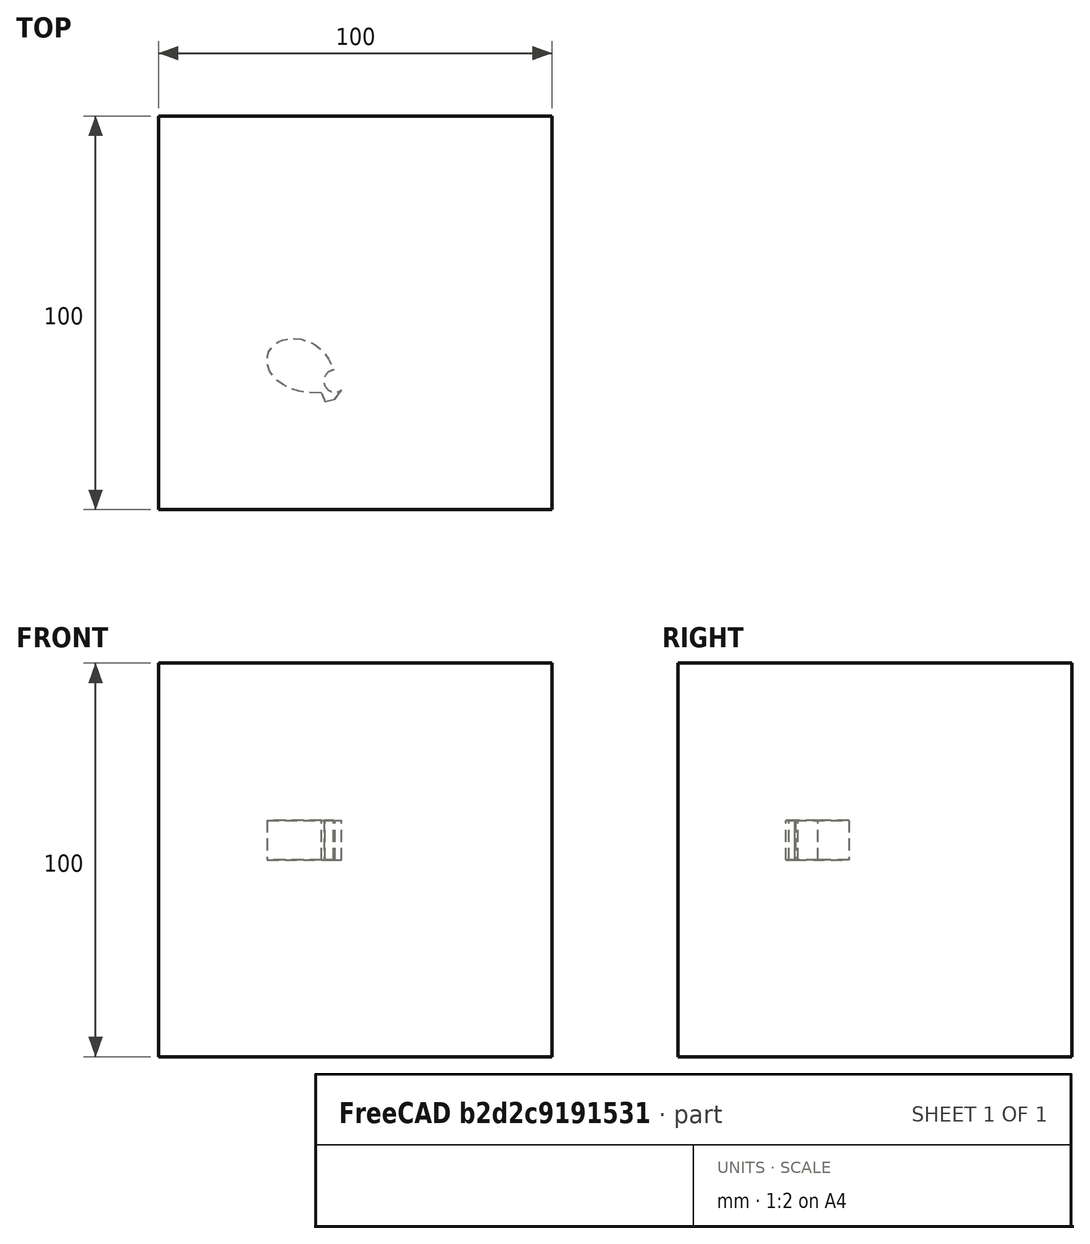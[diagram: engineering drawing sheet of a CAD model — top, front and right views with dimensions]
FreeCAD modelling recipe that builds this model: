
FCSTD DOCUMENT  (FreeCAD 0.19RUnknown)
Label: mirrorTest-2
License: All rights reserved
LicenseURL: http://en.wikipedia.org/wiki/All_rights_reserved
objects: App::DocumentObjectGroupPython×1248, Part::Mirroring×2, App::Part×2, Part::FeaturePython×1, Sketcher::SketchObject×1, Part::Extrusion×1
note: 5 computed .brp shape members not serialized (recipe doc carries the construction recipe); baked Part::Feature solids carry a one-line shape summary decoded from their .brp

FEATURE [App::DocumentObjectGroupPython] HALFPI  # scripted group (container) (typed FeaturePython)
  name = HALFPI
  value = pi/2.
FEATURE [App::DocumentObjectGroupPython] PI  # scripted group (container) (typed FeaturePython)
  name = PI
  value = 1.*pi
FEATURE [App::DocumentObjectGroupPython] TWOPI  # scripted group (container) (typed FeaturePython)
  name = TWOPI
  value = 2.*pi
FEATURE [App::DocumentObjectGroupPython] Constants  # scripted group (container) (typed FeaturePython)
  Group = -> [HALFPI,PI,TWOPI]
FEATURE [App::DocumentObjectGroupPython] Variables  # scripted group (container) (typed FeaturePython)
FEATURE [App::DocumentObjectGroupPython] Quantities  # scripted group (container) (typed FeaturePython)
FEATURE [App::DocumentObjectGroupPython] Isotopes  # scripted group (container) (typed FeaturePython)
FEATURE [App::DocumentObjectGroupPython] Elements  # scripted group (container) (typed FeaturePython)
FEATURE [App::DocumentObjectGroupPython] G4Isotopes  # scripted group (container) (typed FeaturePython)
FEATURE [App::DocumentObjectGroupPython] H_element  # scripted group (container) (typed FeaturePython)
  Z = 1
  atom_value = 1.008
  formula = H
  name = H_element
FEATURE [App::DocumentObjectGroupPython] He_element  # scripted group (container) (typed FeaturePython)
  Z = 2
  atom_value = 4.0026
  formula = He
  name = He_element
FEATURE [App::DocumentObjectGroupPython] Li_element  # scripted group (container) (typed FeaturePython)
  Z = 3
  atom_value = 6.94
  formula = Li
  name = Li_element
FEATURE [App::DocumentObjectGroupPython] Be_element  # scripted group (container) (typed FeaturePython)
  Z = 4
  atom_value = 9.01218
  formula = Be
  name = Be_element
FEATURE [App::DocumentObjectGroupPython] B_element  # scripted group (container) (typed FeaturePython)
  Z = 5
  atom_value = 10.81
  formula = B
  name = B_element
FEATURE [App::DocumentObjectGroupPython] C_element  # scripted group (container) (typed FeaturePython)
  Z = 6
  atom_value = 12.011
  formula = C
  name = C_element
FEATURE [App::DocumentObjectGroupPython] N_element  # scripted group (container) (typed FeaturePython)
  Z = 7
  atom_value = 14.007
  formula = N
  name = N_element
FEATURE [App::DocumentObjectGroupPython] O_element  # scripted group (container) (typed FeaturePython)
  Z = 8
  atom_value = 15.999
  formula = O
  name = O_element
FEATURE [App::DocumentObjectGroupPython] F_element  # scripted group (container) (typed FeaturePython)
  Z = 9
  atom_value = 18.9984
  formula = F
  name = F_element
FEATURE [App::DocumentObjectGroupPython] Ne_element  # scripted group (container) (typed FeaturePython)
  Z = 10
  atom_value = 20.1797
  formula = Ne
  name = Ne_element
FEATURE [App::DocumentObjectGroupPython] Na_element  # scripted group (container) (typed FeaturePython)
  Z = 11
  atom_value = 22.9898
  formula = Na
  name = Na_element
FEATURE [App::DocumentObjectGroupPython] Mg_element  # scripted group (container) (typed FeaturePython)
  Z = 12
  atom_value = 24.305
  formula = Mg
  name = Mg_element
FEATURE [App::DocumentObjectGroupPython] Al_element  # scripted group (container) (typed FeaturePython)
  Z = 13
  atom_value = 26.9815
  formula = Al
  name = Al_element
FEATURE [App::DocumentObjectGroupPython] Si_element  # scripted group (container) (typed FeaturePython)
  Z = 14
  atom_value = 28.085
  formula = Si
  name = Si_element
FEATURE [App::DocumentObjectGroupPython] P_element  # scripted group (container) (typed FeaturePython)
  Z = 15
  atom_value = 30.9738
  formula = P
  name = P_element
FEATURE [App::DocumentObjectGroupPython] S_element  # scripted group (container) (typed FeaturePython)
  Z = 16
  atom_value = 32.06
  formula = S
  name = S_element
FEATURE [App::DocumentObjectGroupPython] Cl_element  # scripted group (container) (typed FeaturePython)
  Z = 17
  atom_value = 35.45
  formula = Cl
  name = Cl_element
FEATURE [App::DocumentObjectGroupPython] Ar_element  # scripted group (container) (typed FeaturePython)
  Z = 18
  atom_value = 39.95
  formula = Ar
  name = Ar_element
FEATURE [App::DocumentObjectGroupPython] K_element  # scripted group (container) (typed FeaturePython)
  Z = 19
  atom_value = 39.0983
  formula = K
  name = K_element
FEATURE [App::DocumentObjectGroupPython] Ca_element  # scripted group (container) (typed FeaturePython)
  Z = 20
  atom_value = 40.078
  formula = Ca
  name = Ca_element
FEATURE [App::DocumentObjectGroupPython] Sc_element  # scripted group (container) (typed FeaturePython)
  Z = 21
  atom_value = 44.9559
  formula = Sc
  name = Sc_element
FEATURE [App::DocumentObjectGroupPython] Ti_element  # scripted group (container) (typed FeaturePython)
  Z = 22
  atom_value = 47.867
  formula = Ti
  name = Ti_element
FEATURE [App::DocumentObjectGroupPython] V_element  # scripted group (container) (typed FeaturePython)
  Z = 23
  atom_value = 50.9415
  formula = V
  name = V_element
FEATURE [App::DocumentObjectGroupPython] Cr_element  # scripted group (container) (typed FeaturePython)
  Z = 24
  atom_value = 51.9961
  formula = Cr
  name = Cr_element
FEATURE [App::DocumentObjectGroupPython] Mn_element  # scripted group (container) (typed FeaturePython)
  Z = 25
  atom_value = 54.938
  formula = Mn
  name = Mn_element
FEATURE [App::DocumentObjectGroupPython] Fe_element  # scripted group (container) (typed FeaturePython)
  Z = 26
  atom_value = 55.845
  formula = Fe
  name = Fe_element
FEATURE [App::DocumentObjectGroupPython] Co_element  # scripted group (container) (typed FeaturePython)
  Z = 27
  atom_value = 58.9332
  formula = Co
  name = Co_element
FEATURE [App::DocumentObjectGroupPython] Ni_element  # scripted group (container) (typed FeaturePython)
  Z = 28
  atom_value = 58.6934
  formula = Ni
  name = Ni_element
FEATURE [App::DocumentObjectGroupPython] Cu_element  # scripted group (container) (typed FeaturePython)
  Z = 29
  atom_value = 63.546
  formula = Cu
  name = Cu_element
FEATURE [App::DocumentObjectGroupPython] Zn_element  # scripted group (container) (typed FeaturePython)
  Z = 30
  atom_value = 65.38
  formula = Zn
  name = Zn_element
FEATURE [App::DocumentObjectGroupPython] Ga_element  # scripted group (container) (typed FeaturePython)
  Z = 31
  atom_value = 69.723
  formula = Ga
  name = Ga_element
FEATURE [App::DocumentObjectGroupPython] Ge_element  # scripted group (container) (typed FeaturePython)
  Z = 32
  atom_value = 72.63
  formula = Ge
  name = Ge_element
FEATURE [App::DocumentObjectGroupPython] As_element  # scripted group (container) (typed FeaturePython)
  Z = 33
  atom_value = 74.9216
  formula = As
  name = As_element
FEATURE [App::DocumentObjectGroupPython] Se_element  # scripted group (container) (typed FeaturePython)
  Z = 34
  atom_value = 78.971
  formula = Se
  name = Se_element
FEATURE [App::DocumentObjectGroupPython] Br_element  # scripted group (container) (typed FeaturePython)
  Z = 35
  atom_value = 79.904
  formula = Br
  name = Br_element
FEATURE [App::DocumentObjectGroupPython] Kr_element  # scripted group (container) (typed FeaturePython)
  Z = 36
  atom_value = 83.798
  formula = Kr
  name = Kr_element
FEATURE [App::DocumentObjectGroupPython] Rb_element  # scripted group (container) (typed FeaturePython)
  Z = 37
  atom_value = 85.4678
  formula = Rb
  name = Rb_element
FEATURE [App::DocumentObjectGroupPython] Sr_element  # scripted group (container) (typed FeaturePython)
  Z = 38
  atom_value = 87.62
  formula = Sr
  name = Sr_element
FEATURE [App::DocumentObjectGroupPython] Y_element  # scripted group (container) (typed FeaturePython)
  Z = 39
  atom_value = 88.9058
  formula = Y
  name = Y_element
FEATURE [App::DocumentObjectGroupPython] Zr_element  # scripted group (container) (typed FeaturePython)
  Z = 40
  atom_value = 91.224
  formula = Zr
  name = Zr_element
FEATURE [App::DocumentObjectGroupPython] Nb_element  # scripted group (container) (typed FeaturePython)
  Z = 41
  atom_value = 92.9064
  formula = Nb
  name = Nb_element
FEATURE [App::DocumentObjectGroupPython] Mo_element  # scripted group (container) (typed FeaturePython)
  Z = 42
  atom_value = 95.95
  formula = Mo
  name = Mo_element
FEATURE [App::DocumentObjectGroupPython] Tc_element  # scripted group (container) (typed FeaturePython)
  Z = 43
  atom_value = 97
  formula = Tc
  name = Tc_element
FEATURE [App::DocumentObjectGroupPython] Ru_element  # scripted group (container) (typed FeaturePython)
  Z = 44
  atom_value = 101.07
  formula = Ru
  name = Ru_element
FEATURE [App::DocumentObjectGroupPython] Rh_element  # scripted group (container) (typed FeaturePython)
  Z = 45
  atom_value = 102.905
  formula = Rh
  name = Rh_element
FEATURE [App::DocumentObjectGroupPython] Pd_element  # scripted group (container) (typed FeaturePython)
  Z = 46
  atom_value = 106.42
  formula = Pd
  name = Pd_element
FEATURE [App::DocumentObjectGroupPython] Ag_element  # scripted group (container) (typed FeaturePython)
  Z = 47
  atom_value = 107.868
  formula = Ag
  name = Ag_element
FEATURE [App::DocumentObjectGroupPython] Cd_element  # scripted group (container) (typed FeaturePython)
  Z = 48
  atom_value = 112.414
  formula = Cd
  name = Cd_element
FEATURE [App::DocumentObjectGroupPython] In_element  # scripted group (container) (typed FeaturePython)
  Z = 49
  atom_value = 114.818
  formula = In
  name = In_element
FEATURE [App::DocumentObjectGroupPython] Sn_element  # scripted group (container) (typed FeaturePython)
  Z = 50
  atom_value = 118.71
  formula = Sn
  name = Sn_element
FEATURE [App::DocumentObjectGroupPython] Sb_element  # scripted group (container) (typed FeaturePython)
  Z = 51
  atom_value = 121.76
  formula = Sb
  name = Sb_element
FEATURE [App::DocumentObjectGroupPython] Te_element  # scripted group (container) (typed FeaturePython)
  Z = 52
  atom_value = 127.6
  formula = Te
  name = Te_element
FEATURE [App::DocumentObjectGroupPython] I_element  # scripted group (container) (typed FeaturePython)
  Z = 53
  atom_value = 126.904
  formula = I
  name = I_element
FEATURE [App::DocumentObjectGroupPython] Xe_element  # scripted group (container) (typed FeaturePython)
  Z = 54
  atom_value = 131.293
  formula = Xe
  name = Xe_element
FEATURE [App::DocumentObjectGroupPython] Cs_element  # scripted group (container) (typed FeaturePython)
  Z = 55
  atom_value = 132.905
  formula = Cs
  name = Cs_element
FEATURE [App::DocumentObjectGroupPython] Ba_element  # scripted group (container) (typed FeaturePython)
  Z = 56
  atom_value = 137.327
  formula = Ba
  name = Ba_element
FEATURE [App::DocumentObjectGroupPython] La_element  # scripted group (container) (typed FeaturePython)
  Z = 57
  atom_value = 138.905
  formula = La
  name = La_element
FEATURE [App::DocumentObjectGroupPython] Ce_element  # scripted group (container) (typed FeaturePython)
  Z = 58
  atom_value = 140.116
  formula = Ce
  name = Ce_element
FEATURE [App::DocumentObjectGroupPython] Pr_element  # scripted group (container) (typed FeaturePython)
  Z = 59
  atom_value = 140.908
  formula = Pr
  name = Pr_element
FEATURE [App::DocumentObjectGroupPython] Nd_element  # scripted group (container) (typed FeaturePython)
  Z = 60
  atom_value = 144.242
  formula = Nd
  name = Nd_element
FEATURE [App::DocumentObjectGroupPython] Pm_element  # scripted group (container) (typed FeaturePython)
  Z = 61
  atom_value = 145
  formula = Pm
  name = Pm_element
FEATURE [App::DocumentObjectGroupPython] Sm_element  # scripted group (container) (typed FeaturePython)
  Z = 62
  atom_value = 150.36
  formula = Sm
  name = Sm_element
FEATURE [App::DocumentObjectGroupPython] Eu_element  # scripted group (container) (typed FeaturePython)
  Z = 63
  atom_value = 151.964
  formula = Eu
  name = Eu_element
FEATURE [App::DocumentObjectGroupPython] Gd_element  # scripted group (container) (typed FeaturePython)
  Z = 64
  atom_value = 157.25
  formula = Gd
  name = Gd_element
FEATURE [App::DocumentObjectGroupPython] Tb_element  # scripted group (container) (typed FeaturePython)
  Z = 65
  atom_value = 158.925
  formula = Tb
  name = Tb_element
FEATURE [App::DocumentObjectGroupPython] Dy_element  # scripted group (container) (typed FeaturePython)
  Z = 66
  atom_value = 162.5
  formula = Dy
  name = Dy_element
FEATURE [App::DocumentObjectGroupPython] Ho_element  # scripted group (container) (typed FeaturePython)
  Z = 67
  atom_value = 164.93
  formula = Ho
  name = Ho_element
FEATURE [App::DocumentObjectGroupPython] Er_element  # scripted group (container) (typed FeaturePython)
  Z = 68
  atom_value = 167.259
  formula = Er
  name = Er_element
FEATURE [App::DocumentObjectGroupPython] Tm_element  # scripted group (container) (typed FeaturePython)
  Z = 69
  atom_value = 168.934
  formula = Tm
  name = Tm_element
FEATURE [App::DocumentObjectGroupPython] Yb_element  # scripted group (container) (typed FeaturePython)
  Z = 70
  atom_value = 173.045
  formula = Yb
  name = Yb_element
FEATURE [App::DocumentObjectGroupPython] Lu_element  # scripted group (container) (typed FeaturePython)
  Z = 71
  atom_value = 174.967
  formula = Lu
  name = Lu_element
FEATURE [App::DocumentObjectGroupPython] Hf_element  # scripted group (container) (typed FeaturePython)
  Z = 72
  atom_value = 178.49
  formula = Hf
  name = Hf_element
FEATURE [App::DocumentObjectGroupPython] Ta_element  # scripted group (container) (typed FeaturePython)
  Z = 73
  atom_value = 180.948
  formula = Ta
  name = Ta_element
FEATURE [App::DocumentObjectGroupPython] W_element  # scripted group (container) (typed FeaturePython)
  Z = 74
  atom_value = 183.84
  formula = W
  name = W_element
FEATURE [App::DocumentObjectGroupPython] Re_element  # scripted group (container) (typed FeaturePython)
  Z = 75
  atom_value = 186.207
  formula = Re
  name = Re_element
FEATURE [App::DocumentObjectGroupPython] Os_element  # scripted group (container) (typed FeaturePython)
  Z = 76
  atom_value = 190.23
  formula = Os
  name = Os_element
FEATURE [App::DocumentObjectGroupPython] Ir_element  # scripted group (container) (typed FeaturePython)
  Z = 77
  atom_value = 192.217
  formula = Ir
  name = Ir_element
FEATURE [App::DocumentObjectGroupPython] Pt_element  # scripted group (container) (typed FeaturePython)
  Z = 78
  atom_value = 195.084
  formula = Pt
  name = Pt_element
FEATURE [App::DocumentObjectGroupPython] Au_element  # scripted group (container) (typed FeaturePython)
  Z = 79
  atom_value = 196.967
  formula = Au
  name = Au_element
FEATURE [App::DocumentObjectGroupPython] Hg_element  # scripted group (container) (typed FeaturePython)
  Z = 80
  atom_value = 200.592
  formula = Hg
  name = Hg_element
FEATURE [App::DocumentObjectGroupPython] Tl_element  # scripted group (container) (typed FeaturePython)
  Z = 81
  atom_value = 204.38
  formula = Tl
  name = Tl_element
FEATURE [App::DocumentObjectGroupPython] Pb_element  # scripted group (container) (typed FeaturePython)
  Z = 82
  atom_value = 207.2
  formula = Pb
  name = Pb_element
FEATURE [App::DocumentObjectGroupPython] Bi_element  # scripted group (container) (typed FeaturePython)
  Z = 83
  atom_value = 208.98
  formula = Bi
  name = Bi_element
FEATURE [App::DocumentObjectGroupPython] Po_element  # scripted group (container) (typed FeaturePython)
  Z = 84
  atom_value = 209
  formula = Po
  name = Po_element
FEATURE [App::DocumentObjectGroupPython] At_element  # scripted group (container) (typed FeaturePython)
  Z = 85
  atom_value = 210
  formula = At
  name = At_element
FEATURE [App::DocumentObjectGroupPython] Rn_element  # scripted group (container) (typed FeaturePython)
  Z = 86
  atom_value = 222
  formula = Rn
  name = Rn_element
FEATURE [App::DocumentObjectGroupPython] Fr_element  # scripted group (container) (typed FeaturePython)
  Z = 87
  atom_value = 223
  formula = Fr
  name = Fr_element
FEATURE [App::DocumentObjectGroupPython] Ra_element  # scripted group (container) (typed FeaturePython)
  Z = 88
  atom_value = 226
  formula = Ra
  name = Ra_element
FEATURE [App::DocumentObjectGroupPython] Ac_element  # scripted group (container) (typed FeaturePython)
  Z = 89
  atom_value = 227
  formula = Ac
  name = Ac_element
FEATURE [App::DocumentObjectGroupPython] Th_element  # scripted group (container) (typed FeaturePython)
  Z = 90
  atom_value = 232.038
  formula = Th
  name = Th_element
FEATURE [App::DocumentObjectGroupPython] Pa_element  # scripted group (container) (typed FeaturePython)
  Z = 91
  atom_value = 231.036
  formula = Pa
  name = Pa_element
FEATURE [App::DocumentObjectGroupPython] U_element  # scripted group (container) (typed FeaturePython)
  Z = 92
  atom_value = 238.029
  formula = U
  name = U_element
FEATURE [App::DocumentObjectGroupPython] Np_element  # scripted group (container) (typed FeaturePython)
  Z = 93
  atom_value = 237
  formula = Np
  name = Np_element
FEATURE [App::DocumentObjectGroupPython] Pu_element  # scripted group (container) (typed FeaturePython)
  Z = 94
  atom_value = 244
  formula = Pu
  name = Pu_element
FEATURE [App::DocumentObjectGroupPython] Am_element  # scripted group (container) (typed FeaturePython)
  Z = 95
  atom_value = 243
  formula = Am
  name = Am_element
FEATURE [App::DocumentObjectGroupPython] Cm_element  # scripted group (container) (typed FeaturePython)
  Z = 96
  atom_value = 247
  formula = Cm
  name = Cm_element
FEATURE [App::DocumentObjectGroupPython] Bk_element  # scripted group (container) (typed FeaturePython)
  Z = 97
  atom_value = 247
  formula = Bk
  name = Bk_element
FEATURE [App::DocumentObjectGroupPython] Cf_element  # scripted group (container) (typed FeaturePython)
  Z = 98
  atom_value = 251
  formula = Cf
  name = Cf_element
FEATURE [App::DocumentObjectGroupPython] G4Elements  # scripted group (container) (typed FeaturePython)
  Group = -> [H_element,He_element,Li_element,Be_element,B_element,C_element,N_element,O_element,F_element,Ne_element,Na_element,Mg_element,Al_element,Si_element,P_element,S_element,Cl_element,Ar_element,K_element,Ca_element,Sc_element,Ti_element,V_element,Cr_element,Mn_element,Fe_element,Co_element,Ni_element,Cu_element,Zn_element,Ga_element,Ge_element,As_element,Se_element,Br_element,Kr_element,Rb_element,+61 more]
FEATURE [App::DocumentObjectGroupPython] H_element001  label="H_element : 0.101"  # scripted group (container) (typed FeaturePython)
  n = 0.101327
FEATURE [App::DocumentObjectGroupPython] C_element001  label="C_element : 0.775"  # scripted group (container) (typed FeaturePython)
  n = 0.7755
FEATURE [App::DocumentObjectGroupPython] N_element001  label="N_element : 0.035"  # scripted group (container) (typed FeaturePython)
  n = 0.035057
FEATURE [App::DocumentObjectGroupPython] O_element001  label="O_element : 0.052"  # scripted group (container) (typed FeaturePython)
  n = 0.0523159
FEATURE [App::DocumentObjectGroupPython] F_element001  label="F_element : 0.017"  # scripted group (container) (typed FeaturePython)
  n = 0.017422
FEATURE [App::DocumentObjectGroupPython] Ca_element001  label="Ca_element : 0.018"  # scripted group (container) (typed FeaturePython)
  n = 0.018378
FEATURE [App::DocumentObjectGroupPython] G4_A_150_TISSUE  label="G4_A-150_TISSUE"  # scripted group (container) (typed FeaturePython)
  Dunit = g/cm3
  Dvalue = 1.127
  Group = -> [H_element001,C_element001,N_element001,O_element001,F_element001,Ca_element001]
  conduct = 2
  density = 1
  expand = 3
  formula = G4_A-150_TISSUE
  name = G4_A-150_TISSUE
  specific = 4
FEATURE [App::DocumentObjectGroupPython] C_element002  label="C_element : 3"  # scripted group (container) (typed FeaturePython)
  n = 3
  ref = C_element
FEATURE [App::DocumentObjectGroupPython] H_element002  label="H_element : 6"  # scripted group (container) (typed FeaturePython)
  n = 6
  ref = H_element
FEATURE [App::DocumentObjectGroupPython] O_element002  label="O_element : 1"  # scripted group (container) (typed FeaturePython)
  n = 1
  ref = O_element
FEATURE [App::DocumentObjectGroupPython] G4_ACETONE  # scripted group (container) (typed FeaturePython)
  Dunit = g/cm3
  Dvalue = 0.7899
  Group = -> [C_element002,H_element002,O_element002]
  conduct = 2
  density = 1
  expand = 3
  formula = G4_ACETONE
  name = G4_ACETONE
  specific = 4
FEATURE [App::DocumentObjectGroupPython] C_element003  label="C_element : 2"  # scripted group (container) (typed FeaturePython)
  n = 2
  ref = C_element
FEATURE [App::DocumentObjectGroupPython] H_element003  label="H_element : 2"  # scripted group (container) (typed FeaturePython)
  n = 2
  ref = H_element
FEATURE [App::DocumentObjectGroupPython] G4_ACETYLENE  # scripted group (container) (typed FeaturePython)
  Dunit = g/cm3
  Dvalue = 0.0010967
  Group = -> [C_element003,H_element003]
  conduct = 2
  density = 1
  expand = 3
  formula = G4_ACETYLENE
  name = G4_ACETYLENE
  specific = 4
FEATURE [App::DocumentObjectGroupPython] C_element004  label="C_element : 5"  # scripted group (container) (typed FeaturePython)
  n = 5
  ref = C_element
FEATURE [App::DocumentObjectGroupPython] H_element004  label="H_element : 5"  # scripted group (container) (typed FeaturePython)
  n = 5
  ref = H_element
FEATURE [App::DocumentObjectGroupPython] N_element002  label="N_element : 5"  # scripted group (container) (typed FeaturePython)
  n = 5
  ref = N_element
FEATURE [App::DocumentObjectGroupPython] G4_ADENINE  # scripted group (container) (typed FeaturePython)
  Dunit = g/cm3
  Dvalue = 1.6
  Group = -> [C_element004,H_element004,N_element002]
  conduct = 2
  density = 1
  expand = 3
  formula = G4_ADENINE
  name = G4_ADENINE
  specific = 4
FEATURE [App::DocumentObjectGroupPython] H_element005  label="H_element : 0.114"  # scripted group (container) (typed FeaturePython)
  n = 0.114
FEATURE [App::DocumentObjectGroupPython] C_element005  label="C_element : 0.598"  # scripted group (container) (typed FeaturePython)
  n = 0.598
FEATURE [App::DocumentObjectGroupPython] N_element003  label="N_element : 0.007"  # scripted group (container) (typed FeaturePython)
  n = 0.007
FEATURE [App::DocumentObjectGroupPython] O_element003  label="O_element : 0.278"  # scripted group (container) (typed FeaturePython)
  n = 0.278
FEATURE [App::DocumentObjectGroupPython] Na_element001  label="Na_element : 0.001"  # scripted group (container) (typed FeaturePython)
  n = 0.001
FEATURE [App::DocumentObjectGroupPython] S_element001  label="S_element : 0.001"  # scripted group (container) (typed FeaturePython)
  n = 0.001
FEATURE [App::DocumentObjectGroupPython] Cl_element001  label="Cl_element : 0.001"  # scripted group (container) (typed FeaturePython)
  n = 0.001
FEATURE [App::DocumentObjectGroupPython] G4_ADIPOSE_TISSUE_ICRP  # scripted group (container) (typed FeaturePython)
  Dunit = g/cm3
  Dvalue = 0.95
  Group = -> [H_element005,C_element005,N_element003,O_element003,Na_element001,S_element001,Cl_element001]
  conduct = 2
  density = 1
  expand = 3
  formula = G4_ADIPOSE_TISSUE_ICRP
  name = G4_ADIPOSE_TISSUE_ICRP
  specific = 4
FEATURE [App::DocumentObjectGroupPython] C_element006  label="C_element : 0.000"  # scripted group (container) (typed FeaturePython)
  n = 0.000124
FEATURE [App::DocumentObjectGroupPython] N_element004  label="N_element : 0.755"  # scripted group (container) (typed FeaturePython)
  n = 0.755268
FEATURE [App::DocumentObjectGroupPython] O_element004  label="O_element : 0.232"  # scripted group (container) (typed FeaturePython)
  n = 0.231781
FEATURE [App::DocumentObjectGroupPython] Ar_element001  label="Ar_element : 0.013"  # scripted group (container) (typed FeaturePython)
  n = 0.012827
FEATURE [App::DocumentObjectGroupPython] G4_AIR  # scripted group (container) (typed FeaturePython)
  Dunit = g/cm3
  Dvalue = 0.00120479
  Group = -> [C_element006,N_element004,O_element004,Ar_element001]
  conduct = 2
  density = 1
  expand = 3
  formula = G4_AIR
  name = G4_AIR
  specific = 4
FEATURE [App::DocumentObjectGroupPython] C_element007  label="C_element : 006"  # scripted group (container) (typed FeaturePython)
  n = 3
  ref = C_element
FEATURE [App::DocumentObjectGroupPython] H_element006  label="H_element : 7"  # scripted group (container) (typed FeaturePython)
  n = 7
  ref = H_element
FEATURE [App::DocumentObjectGroupPython] N_element005  label="N_element : 1"  # scripted group (container) (typed FeaturePython)
  n = 1
  ref = N_element
FEATURE [App::DocumentObjectGroupPython] O_element005  label="O_element : 2"  # scripted group (container) (typed FeaturePython)
  n = 2
  ref = O_element
FEATURE [App::DocumentObjectGroupPython] G4_ALANINE  # scripted group (container) (typed FeaturePython)
  Dunit = g/cm3
  Dvalue = 1.42
  Group = -> [C_element007,H_element006,N_element005,O_element005]
  conduct = 2
  density = 1
  expand = 3
  formula = G4_ALANINE
  name = G4_ALANINE
  specific = 4
FEATURE [App::DocumentObjectGroupPython] Al_element001  label="Al_element : 2"  # scripted group (container) (typed FeaturePython)
  n = 2
  ref = Al_element
FEATURE [App::DocumentObjectGroupPython] O_element006  label="O_element : 3"  # scripted group (container) (typed FeaturePython)
  n = 3
  ref = O_element
FEATURE [App::DocumentObjectGroupPython] G4_ALUMINUM_OXIDE  # scripted group (container) (typed FeaturePython)
  Dunit = g/cm3
  Dvalue = 3.97
  Group = -> [Al_element001,O_element006]
  conduct = 2
  density = 1
  expand = 3
  formula = G4_ALUMINUM_OXIDE
  name = G4_ALUMINUM_OXIDE
  specific = 4
FEATURE [App::DocumentObjectGroupPython] H_element007  label="H_element : 0.106"  # scripted group (container) (typed FeaturePython)
  n = 0.10593
FEATURE [App::DocumentObjectGroupPython] C_element008  label="C_element : 0.789"  # scripted group (container) (typed FeaturePython)
  n = 0.788974
FEATURE [App::DocumentObjectGroupPython] O_element007  label="O_element : 0.105"  # scripted group (container) (typed FeaturePython)
  n = 0.105096
FEATURE [App::DocumentObjectGroupPython] G4_AMBER  # scripted group (container) (typed FeaturePython)
  Dunit = g/cm3
  Dvalue = 1.1
  Group = -> [H_element007,C_element008,O_element007]
  conduct = 2
  density = 1
  expand = 3
  formula = G4_AMBER
  name = G4_AMBER
  specific = 4
FEATURE [App::DocumentObjectGroupPython] N_element006  label="N_element : 006"  # scripted group (container) (typed FeaturePython)
  n = 1
  ref = N_element
FEATURE [App::DocumentObjectGroupPython] H_element008  label="H_element : 3"  # scripted group (container) (typed FeaturePython)
  n = 3
  ref = H_element
FEATURE [App::DocumentObjectGroupPython] G4_AMMONIA  # scripted group (container) (typed FeaturePython)
  Dunit = g/cm3
  Dvalue = 0.000826019
  Group = -> [N_element006,H_element008]
  conduct = 2
  density = 1
  expand = 3
  formula = G4_AMMONIA
  name = G4_AMMONIA
  specific = 4
FEATURE [App::DocumentObjectGroupPython] C_element009  label="C_element : 6"  # scripted group (container) (typed FeaturePython)
  n = 6
  ref = C_element
FEATURE [App::DocumentObjectGroupPython] H_element009  label="H_element : 008"  # scripted group (container) (typed FeaturePython)
  n = 7
  ref = H_element
FEATURE [App::DocumentObjectGroupPython] N_element007  label="N_element : 007"  # scripted group (container) (typed FeaturePython)
  n = 1
  ref = N_element
FEATURE [App::DocumentObjectGroupPython] G4_ANILINE  # scripted group (container) (typed FeaturePython)
  Dunit = g/cm3
  Dvalue = 1.0235
  Group = -> [C_element009,H_element009,N_element007]
  conduct = 2
  density = 1
  expand = 3
  formula = G4_ANILINE
  name = G4_ANILINE
  specific = 4
FEATURE [App::DocumentObjectGroupPython] C_element010  label="C_element : 14"  # scripted group (container) (typed FeaturePython)
  n = 14
  ref = C_element
FEATURE [App::DocumentObjectGroupPython] H_element010  label="H_element : 10"  # scripted group (container) (typed FeaturePython)
  n = 10
  ref = H_element
FEATURE [App::DocumentObjectGroupPython] G4_ANTHRACENE  # scripted group (container) (typed FeaturePython)
  Dunit = g/cm3
  Dvalue = 1.283
  Group = -> [C_element010,H_element010]
  conduct = 2
  density = 1
  expand = 3
  formula = G4_ANTHRACENE
  name = G4_ANTHRACENE
  specific = 4
FEATURE [App::DocumentObjectGroupPython] H_element011  label="H_element : 0.065"  # scripted group (container) (typed FeaturePython)
  n = 0.0654709
FEATURE [App::DocumentObjectGroupPython] C_element011  label="C_element : 0.537"  # scripted group (container) (typed FeaturePython)
  n = 0.536944
FEATURE [App::DocumentObjectGroupPython] N_element008  label="N_element : 0.021"  # scripted group (container) (typed FeaturePython)
  n = 0.0215
FEATURE [App::DocumentObjectGroupPython] O_element008  label="O_element : 0.032"  # scripted group (container) (typed FeaturePython)
  n = 0.032085
FEATURE [App::DocumentObjectGroupPython] F_element002  label="F_element : 0.167"  # scripted group (container) (typed FeaturePython)
  n = 0.167411
FEATURE [App::DocumentObjectGroupPython] Ca_element002  label="Ca_element : 0.177"  # scripted group (container) (typed FeaturePython)
  n = 0.176589
FEATURE [App::DocumentObjectGroupPython] G4_B_100_BONE  label="G4_B-100_BONE"  # scripted group (container) (typed FeaturePython)
  Dunit = g/cm3
  Dvalue = 1.45
  Group = -> [H_element011,C_element011,N_element008,O_element008,F_element002,Ca_element002]
  conduct = 2
  density = 1
  expand = 3
  formula = G4_B-100_BONE
  name = G4_B-100_BONE
  specific = 4
FEATURE [App::DocumentObjectGroupPython] H_element012  label="H_element : 0.057"  # scripted group (container) (typed FeaturePython)
  n = 0.057441
FEATURE [App::DocumentObjectGroupPython] C_element012  label="C_element : 0.790"  # scripted group (container) (typed FeaturePython)
  n = 0.774591
FEATURE [App::DocumentObjectGroupPython] O_element009  label="O_element : 0.168"  # scripted group (container) (typed FeaturePython)
  n = 0.167968
FEATURE [App::DocumentObjectGroupPython] G4_BAKELITE  # scripted group (container) (typed FeaturePython)
  Dunit = g/cm3
  Dvalue = 1.25
  Group = -> [H_element012,C_element012,O_element009]
  conduct = 2
  density = 1
  expand = 3
  formula = G4_BAKELITE
  name = G4_BAKELITE
  specific = 4
FEATURE [App::DocumentObjectGroupPython] Ba_element001  label="Ba_element : 1"  # scripted group (container) (typed FeaturePython)
  n = 1
  ref = Ba_element
FEATURE [App::DocumentObjectGroupPython] F_element003  label="F_element : 2"  # scripted group (container) (typed FeaturePython)
  n = 2
  ref = F_element
FEATURE [App::DocumentObjectGroupPython] G4_BARIUM_FLUORIDE  # scripted group (container) (typed FeaturePython)
  Dunit = g/cm3
  Dvalue = 4.89
  Group = -> [Ba_element001,F_element003]
  conduct = 2
  density = 1
  expand = 3
  formula = G4_BARIUM_FLUORIDE
  name = G4_BARIUM_FLUORIDE
  specific = 4
FEATURE [App::DocumentObjectGroupPython] Ba_element002  label="Ba_element : 002"  # scripted group (container) (typed FeaturePython)
  n = 1
  ref = Ba_element
FEATURE [App::DocumentObjectGroupPython] S_element002  label="S_element : 1"  # scripted group (container) (typed FeaturePython)
  n = 1
  ref = S_element
FEATURE [App::DocumentObjectGroupPython] O_element010  label="O_element : 4"  # scripted group (container) (typed FeaturePython)
  n = 4
  ref = O_element
FEATURE [App::DocumentObjectGroupPython] G4_BARIUM_SULFATE  # scripted group (container) (typed FeaturePython)
  Dunit = g/cm3
  Dvalue = 4.5
  Group = -> [Ba_element002,S_element002,O_element010]
  conduct = 2
  density = 1
  expand = 3
  formula = G4_BARIUM_SULFATE
  name = G4_BARIUM_SULFATE
  specific = 4
FEATURE [App::DocumentObjectGroupPython] C_element013  label="C_element : 007"  # scripted group (container) (typed FeaturePython)
  n = 6
  ref = C_element
FEATURE [App::DocumentObjectGroupPython] H_element013  label="H_element : 009"  # scripted group (container) (typed FeaturePython)
  n = 6
  ref = H_element
FEATURE [App::DocumentObjectGroupPython] G4_BENZENE  # scripted group (container) (typed FeaturePython)
  Dunit = g/cm3
  Dvalue = 0.87865
  Group = -> [C_element013,H_element013]
  conduct = 2
  density = 1
  expand = 3
  formula = G4_BENZENE
  name = G4_BENZENE
  specific = 4
FEATURE [App::DocumentObjectGroupPython] Be_element001  label="Be_element : 1"  # scripted group (container) (typed FeaturePython)
  n = 1
  ref = Be_element
FEATURE [App::DocumentObjectGroupPython] O_element011  label="O_element : 005"  # scripted group (container) (typed FeaturePython)
  n = 1
  ref = O_element
FEATURE [App::DocumentObjectGroupPython] G4_BERYLLIUM_OXIDE  # scripted group (container) (typed FeaturePython)
  Dunit = g/cm3
  Dvalue = 3.01
  Group = -> [Be_element001,O_element011]
  conduct = 2
  density = 1
  expand = 3
  formula = G4_BERYLLIUM_OXIDE
  name = G4_BERYLLIUM_OXIDE
  specific = 4
FEATURE [App::DocumentObjectGroupPython] Bi_element001  label="Bi_element : 4"  # scripted group (container) (typed FeaturePython)
  n = 4
  ref = Bi_element
FEATURE [App::DocumentObjectGroupPython] Ge_element001  label="Ge_element : 3"  # scripted group (container) (typed FeaturePython)
  n = 3
  ref = Ge_element
FEATURE [App::DocumentObjectGroupPython] O_element012  label="O_element : 12"  # scripted group (container) (typed FeaturePython)
  n = 12
  ref = O_element
FEATURE [App::DocumentObjectGroupPython] G4_BGO  # scripted group (container) (typed FeaturePython)
  Dunit = g/cm3
  Dvalue = 7.13
  Group = -> [Bi_element001,Ge_element001,O_element012]
  conduct = 2
  density = 1
  expand = 3
  formula = G4_BGO
  name = G4_BGO
  specific = 4
FEATURE [App::DocumentObjectGroupPython] H_element014  label="H_element : 0.102"  # scripted group (container) (typed FeaturePython)
  n = 0.102
FEATURE [App::DocumentObjectGroupPython] C_element014  label="C_element : 0.110"  # scripted group (container) (typed FeaturePython)
  n = 0.11
FEATURE [App::DocumentObjectGroupPython] N_element009  label="N_element : 0.033"  # scripted group (container) (typed FeaturePython)
  n = 0.033
FEATURE [App::DocumentObjectGroupPython] O_element013  label="O_element : 0.745"  # scripted group (container) (typed FeaturePython)
  n = 0.745
FEATURE [App::DocumentObjectGroupPython] Na_element002  label="Na_element : 0.002"  # scripted group (container) (typed FeaturePython)
  n = 0.001
FEATURE [App::DocumentObjectGroupPython] P_element001  label="P_element : 0.001"  # scripted group (container) (typed FeaturePython)
  n = 0.001
FEATURE [App::DocumentObjectGroupPython] S_element003  label="S_element : 0.002"  # scripted group (container) (typed FeaturePython)
  n = 0.002
FEATURE [App::DocumentObjectGroupPython] Cl_element002  label="Cl_element : 0.003"  # scripted group (container) (typed FeaturePython)
  n = 0.003
FEATURE [App::DocumentObjectGroupPython] K_element001  label="K_element : 0.002"  # scripted group (container) (typed FeaturePython)
  n = 0.002
FEATURE [App::DocumentObjectGroupPython] Fe_element001  label="Fe_element : 0.001"  # scripted group (container) (typed FeaturePython)
  n = 0.001
FEATURE [App::DocumentObjectGroupPython] G4_BLOOD_ICRP  # scripted group (container) (typed FeaturePython)
  Dunit = g/cm3
  Dvalue = 1.06
  Group = -> [H_element014,C_element014,N_element009,O_element013,Na_element002,P_element001,S_element003,Cl_element002,K_element001,Fe_element001]
  conduct = 2
  density = 1
  expand = 3
  formula = G4_BLOOD_ICRP
  name = G4_BLOOD_ICRP
  specific = 4
FEATURE [App::DocumentObjectGroupPython] H_element015  label="H_element : 0.064"  # scripted group (container) (typed FeaturePython)
  n = 0.064
FEATURE [App::DocumentObjectGroupPython] C_element015  label="C_element : 0.278"  # scripted group (container) (typed FeaturePython)
  n = 0.278
FEATURE [App::DocumentObjectGroupPython] N_element010  label="N_element : 0.027"  # scripted group (container) (typed FeaturePython)
  n = 0.027
FEATURE [App::DocumentObjectGroupPython] O_element014  label="O_element : 0.410"  # scripted group (container) (typed FeaturePython)
  n = 0.41
FEATURE [App::DocumentObjectGroupPython] Mg_element001  label="Mg_element : 0.002"  # scripted group (container) (typed FeaturePython)
  n = 0.002
FEATURE [App::DocumentObjectGroupPython] P_element002  label="P_element : 0.070"  # scripted group (container) (typed FeaturePython)
  n = 0.07
FEATURE [App::DocumentObjectGroupPython] S_element004  label="S_element : 0.003"  # scripted group (container) (typed FeaturePython)
  n = 0.002
FEATURE [App::DocumentObjectGroupPython] Ca_element003  label="Ca_element : 0.147"  # scripted group (container) (typed FeaturePython)
  n = 0.147
FEATURE [App::DocumentObjectGroupPython] G4_BONE_COMPACT_ICRU  # scripted group (container) (typed FeaturePython)
  Dunit = g/cm3
  Dvalue = 1.85
  Group = -> [H_element015,C_element015,N_element010,O_element014,Mg_element001,P_element002,S_element004,Ca_element003]
  conduct = 2
  density = 1
  expand = 3
  formula = G4_BONE_COMPACT_ICRU
  name = G4_BONE_COMPACT_ICRU
  specific = 4
FEATURE [App::DocumentObjectGroupPython] H_element016  label="H_element : 0.034"  # scripted group (container) (typed FeaturePython)
  n = 0.034
FEATURE [App::DocumentObjectGroupPython] C_element016  label="C_element : 0.155"  # scripted group (container) (typed FeaturePython)
  n = 0.155
FEATURE [App::DocumentObjectGroupPython] N_element011  label="N_element : 0.042"  # scripted group (container) (typed FeaturePython)
  n = 0.042
FEATURE [App::DocumentObjectGroupPython] O_element015  label="O_element : 0.435"  # scripted group (container) (typed FeaturePython)
  n = 0.435
FEATURE [App::DocumentObjectGroupPython] Na_element003  label="Na_element : 0.003"  # scripted group (container) (typed FeaturePython)
  n = 0.001
FEATURE [App::DocumentObjectGroupPython] Mg_element002  label="Mg_element : 0.003"  # scripted group (container) (typed FeaturePython)
  n = 0.002
FEATURE [App::DocumentObjectGroupPython] P_element003  label="P_element : 0.103"  # scripted group (container) (typed FeaturePython)
  n = 0.103
FEATURE [App::DocumentObjectGroupPython] S_element005  label="S_element : 0.004"  # scripted group (container) (typed FeaturePython)
  n = 0.003
FEATURE [App::DocumentObjectGroupPython] Ca_element004  label="Ca_element : 0.225"  # scripted group (container) (typed FeaturePython)
  n = 0.225
FEATURE [App::DocumentObjectGroupPython] G4_BONE_CORTICAL_ICRP  # scripted group (container) (typed FeaturePython)
  Dunit = g/cm3
  Dvalue = 1.92
  Group = -> [H_element016,C_element016,N_element011,O_element015,Na_element003,Mg_element002,P_element003,S_element005,Ca_element004]
  conduct = 2
  density = 1
  expand = 3
  formula = G4_BONE_CORTICAL_ICRP
  name = G4_BONE_CORTICAL_ICRP
  specific = 4
FEATURE [App::DocumentObjectGroupPython] B_element001  label="B_element : 4"  # scripted group (container) (typed FeaturePython)
  n = 4
  ref = B_element
FEATURE [App::DocumentObjectGroupPython] C_element017  label="C_element : 1"  # scripted group (container) (typed FeaturePython)
  n = 1
  ref = C_element
FEATURE [App::DocumentObjectGroupPython] G4_BORON_CARBIDE  # scripted group (container) (typed FeaturePython)
  Dunit = g/cm3
  Dvalue = 2.52
  Group = -> [B_element001,C_element017]
  conduct = 2
  density = 1
  expand = 3
  formula = G4_BORON_CARBIDE
  name = G4_BORON_CARBIDE
  specific = 4
FEATURE [App::DocumentObjectGroupPython] B_element002  label="B_element : 2"  # scripted group (container) (typed FeaturePython)
  n = 2
  ref = B_element
FEATURE [App::DocumentObjectGroupPython] O_element016  label="O_element : 006"  # scripted group (container) (typed FeaturePython)
  n = 3
  ref = O_element
FEATURE [App::DocumentObjectGroupPython] G4_BORON_OXIDE  # scripted group (container) (typed FeaturePython)
  Dunit = g/cm3
  Dvalue = 1.812
  Group = -> [B_element002,O_element016]
  conduct = 2
  density = 1
  expand = 3
  formula = G4_BORON_OXIDE
  name = G4_BORON_OXIDE
  specific = 4
FEATURE [App::DocumentObjectGroupPython] H_element017  label="H_element : 0.107"  # scripted group (container) (typed FeaturePython)
  n = 0.107
FEATURE [App::DocumentObjectGroupPython] C_element018  label="C_element : 0.145"  # scripted group (container) (typed FeaturePython)
  n = 0.145
FEATURE [App::DocumentObjectGroupPython] N_element012  label="N_element : 0.022"  # scripted group (container) (typed FeaturePython)
  n = 0.022
FEATURE [App::DocumentObjectGroupPython] O_element017  label="O_element : 0.712"  # scripted group (container) (typed FeaturePython)
  n = 0.712
FEATURE [App::DocumentObjectGroupPython] Na_element004  label="Na_element : 0.004"  # scripted group (container) (typed FeaturePython)
  n = 0.002
FEATURE [App::DocumentObjectGroupPython] P_element004  label="P_element : 0.004"  # scripted group (container) (typed FeaturePython)
  n = 0.004
FEATURE [App::DocumentObjectGroupPython] S_element006  label="S_element : 0.005"  # scripted group (container) (typed FeaturePython)
  n = 0.002
FEATURE [App::DocumentObjectGroupPython] Cl_element003  label="Cl_element : 0.004"  # scripted group (container) (typed FeaturePython)
  n = 0.003
FEATURE [App::DocumentObjectGroupPython] K_element002  label="K_element : 0.003"  # scripted group (container) (typed FeaturePython)
  n = 0.003
FEATURE [App::DocumentObjectGroupPython] G4_BRAIN_ICRP  # scripted group (container) (typed FeaturePython)
  Dunit = g/cm3
  Dvalue = 1.04
  Group = -> [H_element017,C_element018,N_element012,O_element017,Na_element004,P_element004,S_element006,Cl_element003,K_element002]
  conduct = 2
  density = 1
  expand = 3
  formula = G4_BRAIN_ICRP
  name = G4_BRAIN_ICRP
  specific = 4
FEATURE [App::DocumentObjectGroupPython] C_element019  label="C_element : 4"  # scripted group (container) (typed FeaturePython)
  n = 4
  ref = C_element
FEATURE [App::DocumentObjectGroupPython] H_element018  label="H_element : 010"  # scripted group (container) (typed FeaturePython)
  n = 10
  ref = H_element
FEATURE [App::DocumentObjectGroupPython] G4_BUTANE  # scripted group (container) (typed FeaturePython)
  Dunit = g/cm3
  Dvalue = 0.00249343
  Group = -> [C_element019,H_element018]
  conduct = 2
  density = 1
  expand = 3
  formula = G4_BUTANE
  name = G4_BUTANE
  specific = 4
FEATURE [App::DocumentObjectGroupPython] C_element020  label="C_element : 008"  # scripted group (container) (typed FeaturePython)
  n = 4
  ref = C_element
FEATURE [App::DocumentObjectGroupPython] H_element019  label="H_element : 011"  # scripted group (container) (typed FeaturePython)
  n = 10
  ref = H_element
FEATURE [App::DocumentObjectGroupPython] O_element018  label="O_element : 007"  # scripted group (container) (typed FeaturePython)
  n = 1
  ref = O_element
FEATURE [App::DocumentObjectGroupPython] G4_N_BUTYL_ALCOHOL  label="G4_N-BUTYL_ALCOHOL"  # scripted group (container) (typed FeaturePython)
  Dunit = g/cm3
  Dvalue = 0.8098
  Group = -> [C_element020,H_element019,O_element018]
  conduct = 2
  density = 1
  expand = 3
  formula = G4_N-BUTYL_ALCOHOL
  name = G4_N-BUTYL_ALCOHOL
  specific = 4
FEATURE [App::DocumentObjectGroupPython] H_element020  label="H_element : 0.025"  # scripted group (container) (typed FeaturePython)
  n = 0.02468
FEATURE [App::DocumentObjectGroupPython] C_element021  label="C_element : 0.502"  # scripted group (container) (typed FeaturePython)
  n = 0.501611
FEATURE [App::DocumentObjectGroupPython] O_element019  label="O_element : 0.005"  # scripted group (container) (typed FeaturePython)
  n = 0.004527
FEATURE [App::DocumentObjectGroupPython] F_element004  label="F_element : 0.465"  # scripted group (container) (typed FeaturePython)
  n = 0.465209
FEATURE [App::DocumentObjectGroupPython] Si_element001  label="Si_element : 0.004"  # scripted group (container) (typed FeaturePython)
  n = 0.003973
FEATURE [App::DocumentObjectGroupPython] G4_C_552  label="G4_C-552"  # scripted group (container) (typed FeaturePython)
  Dunit = g/cm3
  Dvalue = 1.76
  Group = -> [H_element020,C_element021,O_element019,F_element004,Si_element001]
  conduct = 2
  density = 1
  expand = 3
  formula = G4_C-552
  name = G4_C-552
  specific = 4
FEATURE [App::DocumentObjectGroupPython] Cd_element001  label="Cd_element : 1"  # scripted group (container) (typed FeaturePython)
  n = 1
  ref = Cd_element
FEATURE [App::DocumentObjectGroupPython] Te_element001  label="Te_element : 1"  # scripted group (container) (typed FeaturePython)
  n = 1
  ref = Te_element
FEATURE [App::DocumentObjectGroupPython] G4_CADMIUM_TELLURIDE  # scripted group (container) (typed FeaturePython)
  Dunit = g/cm3
  Dvalue = 6.2
  Group = -> [Cd_element001,Te_element001]
  conduct = 2
  density = 1
  expand = 3
  formula = G4_CADMIUM_TELLURIDE
  name = G4_CADMIUM_TELLURIDE
  specific = 4
FEATURE [App::DocumentObjectGroupPython] Cd_element002  label="Cd_element : 002"  # scripted group (container) (typed FeaturePython)
  n = 1
  ref = Cd_element
FEATURE [App::DocumentObjectGroupPython] W_element001  label="W_element : 1"  # scripted group (container) (typed FeaturePython)
  n = 1
  ref = W_element
FEATURE [App::DocumentObjectGroupPython] O_element020  label="O_element : 008"  # scripted group (container) (typed FeaturePython)
  n = 4
  ref = O_element
FEATURE [App::DocumentObjectGroupPython] G4_CADMIUM_TUNGSTATE  # scripted group (container) (typed FeaturePython)
  Dunit = g/cm3
  Dvalue = 7.9
  Group = -> [Cd_element002,W_element001,O_element020]
  conduct = 2
  density = 1
  expand = 3
  formula = G4_CADMIUM_TUNGSTATE
  name = G4_CADMIUM_TUNGSTATE
  specific = 4
FEATURE [App::DocumentObjectGroupPython] Ca_element005  label="Ca_element : 1"  # scripted group (container) (typed FeaturePython)
  n = 1
  ref = Ca_element
FEATURE [App::DocumentObjectGroupPython] C_element022  label="C_element : 009"  # scripted group (container) (typed FeaturePython)
  n = 1
  ref = C_element
FEATURE [App::DocumentObjectGroupPython] O_element021  label="O_element : 009"  # scripted group (container) (typed FeaturePython)
  n = 3
  ref = O_element
FEATURE [App::DocumentObjectGroupPython] G4_CALCIUM_CARBONATE  # scripted group (container) (typed FeaturePython)
  Dunit = g/cm3
  Dvalue = 2.8
  Group = -> [Ca_element005,C_element022,O_element021]
  conduct = 2
  density = 1
  expand = 3
  formula = G4_CALCIUM_CARBONATE
  name = G4_CALCIUM_CARBONATE
  specific = 4
FEATURE [App::DocumentObjectGroupPython] Ca_element006  label="Ca_element : 002"  # scripted group (container) (typed FeaturePython)
  n = 1
  ref = Ca_element
FEATURE [App::DocumentObjectGroupPython] F_element005  label="F_element : 003"  # scripted group (container) (typed FeaturePython)
  n = 2
  ref = F_element
FEATURE [App::DocumentObjectGroupPython] G4_CALCIUM_FLUORIDE  # scripted group (container) (typed FeaturePython)
  Dunit = g/cm3
  Dvalue = 3.18
  Group = -> [Ca_element006,F_element005]
  conduct = 2
  density = 1
  expand = 3
  formula = G4_CALCIUM_FLUORIDE
  name = G4_CALCIUM_FLUORIDE
  specific = 4
FEATURE [App::DocumentObjectGroupPython] Ca_element007  label="Ca_element : 003"  # scripted group (container) (typed FeaturePython)
  n = 1
  ref = Ca_element
FEATURE [App::DocumentObjectGroupPython] O_element022  label="O_element : 010"  # scripted group (container) (typed FeaturePython)
  n = 1
  ref = O_element
FEATURE [App::DocumentObjectGroupPython] G4_CALCIUM_OXIDE  # scripted group (container) (typed FeaturePython)
  Dunit = g/cm3
  Dvalue = 3.3
  Group = -> [Ca_element007,O_element022]
  conduct = 2
  density = 1
  expand = 3
  formula = G4_CALCIUM_OXIDE
  name = G4_CALCIUM_OXIDE
  specific = 4
FEATURE [App::DocumentObjectGroupPython] Ca_element008  label="Ca_element : 004"  # scripted group (container) (typed FeaturePython)
  n = 1
  ref = Ca_element
FEATURE [App::DocumentObjectGroupPython] S_element007  label="S_element : 002"  # scripted group (container) (typed FeaturePython)
  n = 1
  ref = S_element
FEATURE [App::DocumentObjectGroupPython] O_element023  label="O_element : 011"  # scripted group (container) (typed FeaturePython)
  n = 4
  ref = O_element
FEATURE [App::DocumentObjectGroupPython] G4_CALCIUM_SULFATE  # scripted group (container) (typed FeaturePython)
  Dunit = g/cm3
  Dvalue = 2.96
  Group = -> [Ca_element008,S_element007,O_element023]
  conduct = 2
  density = 1
  expand = 3
  formula = G4_CALCIUM_SULFATE
  name = G4_CALCIUM_SULFATE
  specific = 4
FEATURE [App::DocumentObjectGroupPython] Ca_element009  label="Ca_element : 005"  # scripted group (container) (typed FeaturePython)
  n = 1
  ref = Ca_element
FEATURE [App::DocumentObjectGroupPython] W_element002  label="W_element : 002"  # scripted group (container) (typed FeaturePython)
  n = 1
  ref = W_element
FEATURE [App::DocumentObjectGroupPython] O_element024  label="O_element : 012"  # scripted group (container) (typed FeaturePython)
  n = 4
  ref = O_element
FEATURE [App::DocumentObjectGroupPython] G4_CALCIUM_TUNGSTATE  # scripted group (container) (typed FeaturePython)
  Dunit = g/cm3
  Dvalue = 6.062
  Group = -> [Ca_element009,W_element002,O_element024]
  conduct = 2
  density = 1
  expand = 3
  formula = G4_CALCIUM_TUNGSTATE
  name = G4_CALCIUM_TUNGSTATE
  specific = 4
FEATURE [App::DocumentObjectGroupPython] C_element023  label="C_element : 010"  # scripted group (container) (typed FeaturePython)
  n = 1
  ref = C_element
FEATURE [App::DocumentObjectGroupPython] O_element025  label="O_element : 013"  # scripted group (container) (typed FeaturePython)
  n = 2
  ref = O_element
FEATURE [App::DocumentObjectGroupPython] G4_CARBON_DIOXIDE  # scripted group (container) (typed FeaturePython)
  Dunit = g/cm3
  Dvalue = 0.00184212
  Group = -> [C_element023,O_element025]
  conduct = 2
  density = 1
  expand = 3
  formula = G4_CARBON_DIOXIDE
  name = G4_CARBON_DIOXIDE
  specific = 4
FEATURE [App::DocumentObjectGroupPython] C_element024  label="C_element : 011"  # scripted group (container) (typed FeaturePython)
  n = 1
  ref = C_element
FEATURE [App::DocumentObjectGroupPython] Cl_element004  label="Cl_element : 4"  # scripted group (container) (typed FeaturePython)
  n = 4
  ref = Cl_element
FEATURE [App::DocumentObjectGroupPython] G4_CARBON_TETRACHLORIDE  # scripted group (container) (typed FeaturePython)
  Dunit = g/cm3
  Dvalue = 1.594
  Group = -> [C_element024,Cl_element004]
  conduct = 2
  density = 1
  expand = 3
  formula = G4_CARBON_TETRACHLORIDE
  name = G4_CARBON_TETRACHLORIDE
  specific = 4
FEATURE [App::DocumentObjectGroupPython] C_element025  label="C_element : 012"  # scripted group (container) (typed FeaturePython)
  n = 6
  ref = C_element
FEATURE [App::DocumentObjectGroupPython] H_element021  label="H_element : 012"  # scripted group (container) (typed FeaturePython)
  n = 10
  ref = H_element
FEATURE [App::DocumentObjectGroupPython] O_element026  label="O_element : 5"  # scripted group (container) (typed FeaturePython)
  n = 5
  ref = O_element
FEATURE [App::DocumentObjectGroupPython] G4_CELLULOSE_CELLOPHANE  # scripted group (container) (typed FeaturePython)
  Dunit = g/cm3
  Dvalue = 1.42
  Group = -> [C_element025,H_element021,O_element026]
  conduct = 2
  density = 1
  expand = 3
  formula = G4_CELLULOSE_CELLOPHANE
  name = G4_CELLULOSE_CELLOPHANE
  specific = 4
FEATURE [App::DocumentObjectGroupPython] H_element022  label="H_element : 0.067"  # scripted group (container) (typed FeaturePython)
  n = 0.067125
FEATURE [App::DocumentObjectGroupPython] C_element026  label="C_element : 0.545"  # scripted group (container) (typed FeaturePython)
  n = 0.545403
FEATURE [App::DocumentObjectGroupPython] O_element027  label="O_element : 0.387"  # scripted group (container) (typed FeaturePython)
  n = 0.387472
FEATURE [App::DocumentObjectGroupPython] G4_CELLULOSE_BUTYRATE  # scripted group (container) (typed FeaturePython)
  Dunit = g/cm3
  Dvalue = 1.2
  Group = -> [H_element022,C_element026,O_element027]
  conduct = 2
  density = 1
  expand = 3
  formula = G4_CELLULOSE_BUTYRATE
  name = G4_CELLULOSE_BUTYRATE
  specific = 4
FEATURE [App::DocumentObjectGroupPython] H_element023  label="H_element : 0.029"  # scripted group (container) (typed FeaturePython)
  n = 0.029216
FEATURE [App::DocumentObjectGroupPython] C_element027  label="C_element : 0.271"  # scripted group (container) (typed FeaturePython)
  n = 0.271296
FEATURE [App::DocumentObjectGroupPython] N_element013  label="N_element : 0.121"  # scripted group (container) (typed FeaturePython)
  n = 0.121276
FEATURE [App::DocumentObjectGroupPython] O_element028  label="O_element : 0.578"  # scripted group (container) (typed FeaturePython)
  n = 0.578212
FEATURE [App::DocumentObjectGroupPython] G4_CELLULOSE_NITRATE  # scripted group (container) (typed FeaturePython)
  Dunit = g/cm3
  Dvalue = 1.49
  Group = -> [H_element023,C_element027,N_element013,O_element028]
  conduct = 2
  density = 1
  expand = 3
  formula = G4_CELLULOSE_NITRATE
  name = G4_CELLULOSE_NITRATE
  specific = 4
FEATURE [App::DocumentObjectGroupPython] H_element024  label="H_element : 0.108"  # scripted group (container) (typed FeaturePython)
  n = 0.107596
FEATURE [App::DocumentObjectGroupPython] N_element014  label="N_element : 0.001"  # scripted group (container) (typed FeaturePython)
  n = 0.0008
FEATURE [App::DocumentObjectGroupPython] O_element029  label="O_element : 0.875"  # scripted group (container) (typed FeaturePython)
  n = 0.874976
FEATURE [App::DocumentObjectGroupPython] S_element008  label="S_element : 0.015"  # scripted group (container) (typed FeaturePython)
  n = 0.014627
FEATURE [App::DocumentObjectGroupPython] Ce_element001  label="Ce_element : 0.002"  # scripted group (container) (typed FeaturePython)
  n = 0.002001
FEATURE [App::DocumentObjectGroupPython] G4_CERIC_SULFATE  # scripted group (container) (typed FeaturePython)
  Dunit = g/cm3
  Dvalue = 1.03
  Group = -> [H_element024,N_element014,O_element029,S_element008,Ce_element001]
  conduct = 2
  density = 1
  expand = 3
  formula = G4_CERIC_SULFATE
  name = G4_CERIC_SULFATE
  specific = 4
FEATURE [App::DocumentObjectGroupPython] Cs_element001  label="Cs_element : 1"  # scripted group (container) (typed FeaturePython)
  n = 1
  ref = Cs_element
FEATURE [App::DocumentObjectGroupPython] F_element006  label="F_element : 1"  # scripted group (container) (typed FeaturePython)
  n = 1
  ref = F_element
FEATURE [App::DocumentObjectGroupPython] G4_CESIUM_FLUORIDE  # scripted group (container) (typed FeaturePython)
  Dunit = g/cm3
  Dvalue = 4.115
  Group = -> [Cs_element001,F_element006]
  conduct = 2
  density = 1
  expand = 3
  formula = G4_CESIUM_FLUORIDE
  name = G4_CESIUM_FLUORIDE
  specific = 4
FEATURE [App::DocumentObjectGroupPython] Cs_element002  label="Cs_element : 002"  # scripted group (container) (typed FeaturePython)
  n = 1
  ref = Cs_element
FEATURE [App::DocumentObjectGroupPython] I_element001  label="I_element : 1"  # scripted group (container) (typed FeaturePython)
  n = 1
  ref = I_element
FEATURE [App::DocumentObjectGroupPython] G4_CESIUM_IODIDE  # scripted group (container) (typed FeaturePython)
  Dunit = g/cm3
  Dvalue = 4.51
  Group = -> [Cs_element002,I_element001]
  conduct = 2
  density = 1
  expand = 3
  formula = G4_CESIUM_IODIDE
  name = G4_CESIUM_IODIDE
  specific = 4
FEATURE [App::DocumentObjectGroupPython] C_element028  label="C_element : 013"  # scripted group (container) (typed FeaturePython)
  n = 6
  ref = C_element
FEATURE [App::DocumentObjectGroupPython] H_element025  label="H_element : 013"  # scripted group (container) (typed FeaturePython)
  n = 5
  ref = H_element
FEATURE [App::DocumentObjectGroupPython] Cl_element005  label="Cl_element : 1"  # scripted group (container) (typed FeaturePython)
  n = 1
  ref = Cl_element
FEATURE [App::DocumentObjectGroupPython] G4_CHLOROBENZENE  # scripted group (container) (typed FeaturePython)
  Dunit = g/cm3
  Dvalue = 1.1058
  Group = -> [C_element028,H_element025,Cl_element005]
  conduct = 2
  density = 1
  expand = 3
  formula = G4_CHLOROBENZENE
  name = G4_CHLOROBENZENE
  specific = 4
FEATURE [App::DocumentObjectGroupPython] C_element029  label="C_element : 014"  # scripted group (container) (typed FeaturePython)
  n = 1
  ref = C_element
FEATURE [App::DocumentObjectGroupPython] H_element026  label="H_element : 1"  # scripted group (container) (typed FeaturePython)
  n = 1
  ref = H_element
FEATURE [App::DocumentObjectGroupPython] Cl_element006  label="Cl_element : 3"  # scripted group (container) (typed FeaturePython)
  n = 3
  ref = Cl_element
FEATURE [App::DocumentObjectGroupPython] G4_CHLOROFORM  # scripted group (container) (typed FeaturePython)
  Dunit = g/cm3
  Dvalue = 1.4832
  Group = -> [C_element029,H_element026,Cl_element006]
  conduct = 2
  density = 1
  expand = 3
  formula = G4_CHLOROFORM
  name = G4_CHLOROFORM
  specific = 4
FEATURE [App::DocumentObjectGroupPython] H_element027  label="H_element : 0.010"  # scripted group (container) (typed FeaturePython)
  n = 0.01
FEATURE [App::DocumentObjectGroupPython] C_element030  label="C_element : 0.001"  # scripted group (container) (typed FeaturePython)
  n = 0.001
FEATURE [App::DocumentObjectGroupPython] O_element030  label="O_element : 0.529"  # scripted group (container) (typed FeaturePython)
  n = 0.529107
FEATURE [App::DocumentObjectGroupPython] Na_element005  label="Na_element : 0.016"  # scripted group (container) (typed FeaturePython)
  n = 0.016
FEATURE [App::DocumentObjectGroupPython] Mg_element003  label="Mg_element : 0.004"  # scripted group (container) (typed FeaturePython)
  n = 0.002
FEATURE [App::DocumentObjectGroupPython] Al_element002  label="Al_element : 0.034"  # scripted group (container) (typed FeaturePython)
  n = 0.033872
FEATURE [App::DocumentObjectGroupPython] Si_element002  label="Si_element : 0.337"  # scripted group (container) (typed FeaturePython)
  n = 0.337021
FEATURE [App::DocumentObjectGroupPython] K_element003  label="K_element : 0.013"  # scripted group (container) (typed FeaturePython)
  n = 0.013
FEATURE [App::DocumentObjectGroupPython] Ca_element010  label="Ca_element : 0.044"  # scripted group (container) (typed FeaturePython)
  n = 0.044
FEATURE [App::DocumentObjectGroupPython] Fe_element002  label="Fe_element : 0.014"  # scripted group (container) (typed FeaturePython)
  n = 0.014
FEATURE [App::DocumentObjectGroupPython] G4_CONCRETE  # scripted group (container) (typed FeaturePython)
  Dunit = g/cm3
  Dvalue = 2.3
  Group = -> [H_element027,C_element030,O_element030,Na_element005,Mg_element003,Al_element002,Si_element002,K_element003,Ca_element010,Fe_element002]
  conduct = 2
  density = 1
  expand = 3
  formula = G4_CONCRETE
  name = G4_CONCRETE
  specific = 4
FEATURE [App::DocumentObjectGroupPython] C_element031  label="C_element : 015"  # scripted group (container) (typed FeaturePython)
  n = 6
  ref = C_element
FEATURE [App::DocumentObjectGroupPython] H_element028  label="H_element : 12"  # scripted group (container) (typed FeaturePython)
  n = 12
  ref = H_element
FEATURE [App::DocumentObjectGroupPython] G4_CYCLOHEXANE  # scripted group (container) (typed FeaturePython)
  Dunit = g/cm3
  Dvalue = 0.779
  Group = -> [C_element031,H_element028]
  conduct = 2
  density = 1
  expand = 3
  formula = G4_CYCLOHEXANE
  name = G4_CYCLOHEXANE
  specific = 4
FEATURE [App::DocumentObjectGroupPython] C_element032  label="C_element : 016"  # scripted group (container) (typed FeaturePython)
  n = 6
  ref = C_element
FEATURE [App::DocumentObjectGroupPython] H_element029  label="H_element : 4"  # scripted group (container) (typed FeaturePython)
  n = 4
  ref = H_element
FEATURE [App::DocumentObjectGroupPython] Cl_element007  label="Cl_element : 2"  # scripted group (container) (typed FeaturePython)
  n = 2
  ref = Cl_element
FEATURE [App::DocumentObjectGroupPython] G4_1_2_DICHLOROBENZENE  label="G4_1.2-DICHLOROBENZENE"  # scripted group (container) (typed FeaturePython)
  Dunit = g/cm3
  Dvalue = 1.3048
  Group = -> [C_element032,H_element029,Cl_element007]
  conduct = 2
  density = 1
  expand = 3
  formula = G4_1.2-DICHLOROBENZENE
  name = G4_1.2-DICHLOROBENZENE
  specific = 4
FEATURE [App::DocumentObjectGroupPython] C_element033  label="C_element : 017"  # scripted group (container) (typed FeaturePython)
  n = 4
  ref = C_element
FEATURE [App::DocumentObjectGroupPython] H_element030  label="H_element : 8"  # scripted group (container) (typed FeaturePython)
  n = 8
  ref = H_element
FEATURE [App::DocumentObjectGroupPython] O_element031  label="O_element : 014"  # scripted group (container) (typed FeaturePython)
  n = 1
  ref = O_element
FEATURE [App::DocumentObjectGroupPython] Cl_element008  label="Cl_element : 005"  # scripted group (container) (typed FeaturePython)
  n = 2
  ref = Cl_element
FEATURE [App::DocumentObjectGroupPython] G4_DICHLORODIETHYL_ETHER  # scripted group (container) (typed FeaturePython)
  Dunit = g/cm3
  Dvalue = 1.2199
  Group = -> [C_element033,H_element030,O_element031,Cl_element008]
  conduct = 2
  density = 1
  expand = 3
  formula = G4_DICHLORODIETHYL_ETHER
  name = G4_DICHLORODIETHYL_ETHER
  specific = 4
FEATURE [App::DocumentObjectGroupPython] C_element034  label="C_element : 018"  # scripted group (container) (typed FeaturePython)
  n = 2
  ref = C_element
FEATURE [App::DocumentObjectGroupPython] H_element031  label="H_element : 014"  # scripted group (container) (typed FeaturePython)
  n = 4
  ref = H_element
FEATURE [App::DocumentObjectGroupPython] Cl_element009  label="Cl_element : 006"  # scripted group (container) (typed FeaturePython)
  n = 2
  ref = Cl_element
FEATURE [App::DocumentObjectGroupPython] G4_1_2_DICHLOROETHANE  label="G4_1.2-DICHLOROETHANE"  # scripted group (container) (typed FeaturePython)
  Dunit = g/cm3
  Dvalue = 1.2351
  Group = -> [C_element034,H_element031,Cl_element009]
  conduct = 2
  density = 1
  expand = 3
  formula = G4_1.2-DICHLOROETHANE
  name = G4_1.2-DICHLOROETHANE
  specific = 4
FEATURE [App::DocumentObjectGroupPython] C_element035  label="C_element : 019"  # scripted group (container) (typed FeaturePython)
  n = 4
  ref = C_element
FEATURE [App::DocumentObjectGroupPython] H_element032  label="H_element : 015"  # scripted group (container) (typed FeaturePython)
  n = 10
  ref = H_element
FEATURE [App::DocumentObjectGroupPython] O_element032  label="O_element : 015"  # scripted group (container) (typed FeaturePython)
  n = 1
  ref = O_element
FEATURE [App::DocumentObjectGroupPython] G4_DIETHYL_ETHER  # scripted group (container) (typed FeaturePython)
  Dunit = g/cm3
  Dvalue = 0.71378
  Group = -> [C_element035,H_element032,O_element032]
  conduct = 2
  density = 1
  expand = 3
  formula = G4_DIETHYL_ETHER
  name = G4_DIETHYL_ETHER
  specific = 4
FEATURE [App::DocumentObjectGroupPython] C_element036  label="C_element : 020"  # scripted group (container) (typed FeaturePython)
  n = 3
  ref = C_element
FEATURE [App::DocumentObjectGroupPython] H_element033  label="H_element : 016"  # scripted group (container) (typed FeaturePython)
  n = 7
  ref = H_element
FEATURE [App::DocumentObjectGroupPython] N_element015  label="N_element : 008"  # scripted group (container) (typed FeaturePython)
  n = 1
  ref = N_element
FEATURE [App::DocumentObjectGroupPython] O_element033  label="O_element : 016"  # scripted group (container) (typed FeaturePython)
  n = 1
  ref = O_element
FEATURE [App::DocumentObjectGroupPython] G4_N_N_DIMETHYL_FORMAMIDE  label="G4_N.N-DIMETHYL_FORMAMIDE"  # scripted group (container) (typed FeaturePython)
  Dunit = g/cm3
  Dvalue = 0.9487
  Group = -> [C_element036,H_element033,N_element015,O_element033]
  conduct = 2
  density = 1
  expand = 3
  formula = G4_N.N-DIMETHYL_FORMAMIDE
  name = G4_N.N-DIMETHYL_FORMAMIDE
  specific = 4
FEATURE [App::DocumentObjectGroupPython] C_element037  label="C_element : 021"  # scripted group (container) (typed FeaturePython)
  n = 2
  ref = C_element
FEATURE [App::DocumentObjectGroupPython] H_element034  label="H_element : 017"  # scripted group (container) (typed FeaturePython)
  n = 6
  ref = H_element
FEATURE [App::DocumentObjectGroupPython] O_element034  label="O_element : 017"  # scripted group (container) (typed FeaturePython)
  n = 1
  ref = O_element
FEATURE [App::DocumentObjectGroupPython] S_element009  label="S_element : 003"  # scripted group (container) (typed FeaturePython)
  n = 1
  ref = S_element
FEATURE [App::DocumentObjectGroupPython] G4_DIMETHYL_SULFOXIDE  # scripted group (container) (typed FeaturePython)
  Dunit = g/cm3
  Dvalue = 1.1014
  Group = -> [C_element037,H_element034,O_element034,S_element009]
  conduct = 2
  density = 1
  expand = 3
  formula = G4_DIMETHYL_SULFOXIDE
  name = G4_DIMETHYL_SULFOXIDE
  specific = 4
FEATURE [App::DocumentObjectGroupPython] C_element038  label="C_element : 022"  # scripted group (container) (typed FeaturePython)
  n = 2
  ref = C_element
FEATURE [App::DocumentObjectGroupPython] H_element035  label="H_element : 018"  # scripted group (container) (typed FeaturePython)
  n = 6
  ref = H_element
FEATURE [App::DocumentObjectGroupPython] G4_ETHANE  # scripted group (container) (typed FeaturePython)
  Dunit = g/cm3
  Dvalue = 0.00125324
  Group = -> [C_element038,H_element035]
  conduct = 2
  density = 1
  expand = 3
  formula = G4_ETHANE
  name = G4_ETHANE
  specific = 4
FEATURE [App::DocumentObjectGroupPython] C_element039  label="C_element : 023"  # scripted group (container) (typed FeaturePython)
  n = 2
  ref = C_element
FEATURE [App::DocumentObjectGroupPython] H_element036  label="H_element : 019"  # scripted group (container) (typed FeaturePython)
  n = 6
  ref = H_element
FEATURE [App::DocumentObjectGroupPython] O_element035  label="O_element : 018"  # scripted group (container) (typed FeaturePython)
  n = 1
  ref = O_element
FEATURE [App::DocumentObjectGroupPython] G4_ETHYL_ALCOHOL  # scripted group (container) (typed FeaturePython)
  Dunit = g/cm3
  Dvalue = 0.7893
  Group = -> [C_element039,H_element036,O_element035]
  conduct = 2
  density = 1
  expand = 3
  formula = G4_ETHYL_ALCOHOL
  name = G4_ETHYL_ALCOHOL
  specific = 4
FEATURE [App::DocumentObjectGroupPython] H_element037  label="H_element : 0.090"  # scripted group (container) (typed FeaturePython)
  n = 0.090027
FEATURE [App::DocumentObjectGroupPython] C_element040  label="C_element : 0.585"  # scripted group (container) (typed FeaturePython)
  n = 0.585182
FEATURE [App::DocumentObjectGroupPython] O_element036  label="O_element : 0.325"  # scripted group (container) (typed FeaturePython)
  n = 0.324791
FEATURE [App::DocumentObjectGroupPython] G4_ETHYL_CELLULOSE  # scripted group (container) (typed FeaturePython)
  Dunit = g/cm3
  Dvalue = 1.13
  Group = -> [H_element037,C_element040,O_element036]
  conduct = 2
  density = 1
  expand = 3
  formula = G4_ETHYL_CELLULOSE
  name = G4_ETHYL_CELLULOSE
  specific = 4
FEATURE [App::DocumentObjectGroupPython] C_element041  label="C_element : 024"  # scripted group (container) (typed FeaturePython)
  n = 2
  ref = C_element
FEATURE [App::DocumentObjectGroupPython] H_element038  label="H_element : 020"  # scripted group (container) (typed FeaturePython)
  n = 4
  ref = H_element
FEATURE [App::DocumentObjectGroupPython] G4_ETHYLENE  # scripted group (container) (typed FeaturePython)
  Dunit = g/cm3
  Dvalue = 0.00117497
  Group = -> [C_element041,H_element038]
  conduct = 2
  density = 1
  expand = 3
  formula = G4_ETHYLENE
  name = G4_ETHYLENE
  specific = 4
FEATURE [App::DocumentObjectGroupPython] H_element039  label="H_element : 0.096"  # scripted group (container) (typed FeaturePython)
  n = 0.096
FEATURE [App::DocumentObjectGroupPython] C_element042  label="C_element : 0.195"  # scripted group (container) (typed FeaturePython)
  n = 0.195
FEATURE [App::DocumentObjectGroupPython] N_element016  label="N_element : 0.057"  # scripted group (container) (typed FeaturePython)
  n = 0.057
FEATURE [App::DocumentObjectGroupPython] O_element037  label="O_element : 0.646"  # scripted group (container) (typed FeaturePython)
  n = 0.646
FEATURE [App::DocumentObjectGroupPython] Na_element006  label="Na_element : 0.017"  # scripted group (container) (typed FeaturePython)
  n = 0.001
FEATURE [App::DocumentObjectGroupPython] P_element005  label="P_element : 0.104"  # scripted group (container) (typed FeaturePython)
  n = 0.001
FEATURE [App::DocumentObjectGroupPython] S_element010  label="S_element : 0.016"  # scripted group (container) (typed FeaturePython)
  n = 0.003
FEATURE [App::DocumentObjectGroupPython] Cl_element010  label="Cl_element : 0.005"  # scripted group (container) (typed FeaturePython)
  n = 0.001
FEATURE [App::DocumentObjectGroupPython] G4_EYE_LENS_ICRP  # scripted group (container) (typed FeaturePython)
  Dunit = g/cm3
  Dvalue = 1.07
  Group = -> [H_element039,C_element042,N_element016,O_element037,Na_element006,P_element005,S_element010,Cl_element010]
  conduct = 2
  density = 1
  expand = 3
  formula = G4_EYE_LENS_ICRP
  name = G4_EYE_LENS_ICRP
  specific = 4
FEATURE [App::DocumentObjectGroupPython] Fe_element003  label="Fe_element : 2"  # scripted group (container) (typed FeaturePython)
  n = 2
  ref = Fe_element
FEATURE [App::DocumentObjectGroupPython] O_element038  label="O_element : 019"  # scripted group (container) (typed FeaturePython)
  n = 3
  ref = O_element
FEATURE [App::DocumentObjectGroupPython] G4_FERRIC_OXIDE  # scripted group (container) (typed FeaturePython)
  Dunit = g/cm3
  Dvalue = 5.2
  Group = -> [Fe_element003,O_element038]
  conduct = 2
  density = 1
  expand = 3
  formula = G4_FERRIC_OXIDE
  name = G4_FERRIC_OXIDE
  specific = 4
FEATURE [App::DocumentObjectGroupPython] Fe_element004  label="Fe_element : 1"  # scripted group (container) (typed FeaturePython)
  n = 1
  ref = Fe_element
FEATURE [App::DocumentObjectGroupPython] B_element003  label="B_element : 1"  # scripted group (container) (typed FeaturePython)
  n = 1
  ref = B_element
FEATURE [App::DocumentObjectGroupPython] G4_FERROBORIDE  # scripted group (container) (typed FeaturePython)
  Dunit = g/cm3
  Dvalue = 7.15
  Group = -> [Fe_element004,B_element003]
  conduct = 2
  density = 1
  expand = 3
  formula = G4_FERROBORIDE
  name = G4_FERROBORIDE
  specific = 4
FEATURE [App::DocumentObjectGroupPython] Fe_element005  label="Fe_element : 003"  # scripted group (container) (typed FeaturePython)
  n = 1
  ref = Fe_element
FEATURE [App::DocumentObjectGroupPython] O_element039  label="O_element : 020"  # scripted group (container) (typed FeaturePython)
  n = 1
  ref = O_element
FEATURE [App::DocumentObjectGroupPython] G4_FERROUS_OXIDE  # scripted group (container) (typed FeaturePython)
  Dunit = g/cm3
  Dvalue = 5.7
  Group = -> [Fe_element005,O_element039]
  conduct = 2
  density = 1
  expand = 3
  formula = G4_FERROUS_OXIDE
  name = G4_FERROUS_OXIDE
  specific = 4
FEATURE [App::DocumentObjectGroupPython] H_element040  label="H_element : 0.115"  # scripted group (container) (typed FeaturePython)
  n = 0.108259
FEATURE [App::DocumentObjectGroupPython] N_element017  label="N_element : 0.000"  # scripted group (container) (typed FeaturePython)
  n = 2.7e-05
FEATURE [App::DocumentObjectGroupPython] O_element040  label="O_element : 0.879"  # scripted group (container) (typed FeaturePython)
  n = 0.878636
FEATURE [App::DocumentObjectGroupPython] Na_element007  label="Na_element : 0.000"  # scripted group (container) (typed FeaturePython)
  n = 2.2e-05
FEATURE [App::DocumentObjectGroupPython] S_element011  label="S_element : 0.013"  # scripted group (container) (typed FeaturePython)
  n = 0.012968
FEATURE [App::DocumentObjectGroupPython] Cl_element011  label="Cl_element : 0.000"  # scripted group (container) (typed FeaturePython)
  n = 3.4e-05
FEATURE [App::DocumentObjectGroupPython] Fe_element006  label="Fe_element : 0.000"  # scripted group (container) (typed FeaturePython)
  n = 5.4e-05
FEATURE [App::DocumentObjectGroupPython] G4_FERROUS_SULFATE  # scripted group (container) (typed FeaturePython)
  Dunit = g/cm3
  Dvalue = 1.024
  Group = -> [H_element040,N_element017,O_element040,Na_element007,S_element011,Cl_element011,Fe_element006]
  conduct = 2
  density = 1
  expand = 3
  formula = G4_FERROUS_SULFATE
  name = G4_FERROUS_SULFATE
  specific = 4
FEATURE [App::DocumentObjectGroupPython] C_element043  label="C_element : 0.099"  # scripted group (container) (typed FeaturePython)
  n = 0.099335
FEATURE [App::DocumentObjectGroupPython] F_element007  label="F_element : 0.314"  # scripted group (container) (typed FeaturePython)
  n = 0.314247
FEATURE [App::DocumentObjectGroupPython] Cl_element012  label="Cl_element : 0.586"  # scripted group (container) (typed FeaturePython)
  n = 0.586418
FEATURE [App::DocumentObjectGroupPython] G4_FREON_12  label="G4_FREON-12"  # scripted group (container) (typed FeaturePython)
  Dunit = g/cm3
  Dvalue = 1.12
  Group = -> [C_element043,F_element007,Cl_element012]
  conduct = 2
  density = 1
  expand = 3
  formula = G4_FREON-12
  name = G4_FREON-12
  specific = 4
FEATURE [App::DocumentObjectGroupPython] C_element044  label="C_element : 0.057"  # scripted group (container) (typed FeaturePython)
  n = 0.057245
FEATURE [App::DocumentObjectGroupPython] F_element008  label="F_element : 0.181"  # scripted group (container) (typed FeaturePython)
  n = 0.181096
FEATURE [App::DocumentObjectGroupPython] Br_element001  label="Br_element : 0.762"  # scripted group (container) (typed FeaturePython)
  n = 0.761659
FEATURE [App::DocumentObjectGroupPython] G4_FREON_12B2  label="G4_FREON-12B2"  # scripted group (container) (typed FeaturePython)
  Dunit = g/cm3
  Dvalue = 1.8
  Group = -> [C_element044,F_element008,Br_element001]
  conduct = 2
  density = 1
  expand = 3
  formula = G4_FREON-12B2
  name = G4_FREON-12B2
  specific = 4
FEATURE [App::DocumentObjectGroupPython] C_element045  label="C_element : 0.115"  # scripted group (container) (typed FeaturePython)
  n = 0.114983
FEATURE [App::DocumentObjectGroupPython] F_element009  label="F_element : 0.546"  # scripted group (container) (typed FeaturePython)
  n = 0.545621
FEATURE [App::DocumentObjectGroupPython] Cl_element013  label="Cl_element : 0.339"  # scripted group (container) (typed FeaturePython)
  n = 0.339396
FEATURE [App::DocumentObjectGroupPython] G4_FREON_13  label="G4_FREON-13"  # scripted group (container) (typed FeaturePython)
  Dunit = g/cm3
  Dvalue = 0.95
  Group = -> [C_element045,F_element009,Cl_element013]
  conduct = 2
  density = 1
  expand = 3
  formula = G4_FREON-13
  name = G4_FREON-13
  specific = 4
FEATURE [App::DocumentObjectGroupPython] C_element046  label="C_element : 025"  # scripted group (container) (typed FeaturePython)
  n = 1
  ref = C_element
FEATURE [App::DocumentObjectGroupPython] F_element010  label="F_element : 3"  # scripted group (container) (typed FeaturePython)
  n = 3
  ref = F_element
FEATURE [App::DocumentObjectGroupPython] Br_element002  label="Br_element : 1"  # scripted group (container) (typed FeaturePython)
  n = 1
  ref = Br_element
FEATURE [App::DocumentObjectGroupPython] G4_FREON_13B1  label="G4_FREON-13B1"  # scripted group (container) (typed FeaturePython)
  Dunit = g/cm3
  Dvalue = 1.5
  Group = -> [C_element046,F_element010,Br_element002]
  conduct = 2
  density = 1
  expand = 3
  formula = G4_FREON-13B1
  name = G4_FREON-13B1
  specific = 4
FEATURE [App::DocumentObjectGroupPython] C_element047  label="C_element : 0.061"  # scripted group (container) (typed FeaturePython)
  n = 0.061309
FEATURE [App::DocumentObjectGroupPython] F_element011  label="F_element : 0.291"  # scripted group (container) (typed FeaturePython)
  n = 0.290924
FEATURE [App::DocumentObjectGroupPython] I_element002  label="I_element : 0.648"  # scripted group (container) (typed FeaturePython)
  n = 0.647767
FEATURE [App::DocumentObjectGroupPython] G4_FREON_13I1  label="G4_FREON-13I1"  # scripted group (container) (typed FeaturePython)
  Dunit = g/cm3
  Dvalue = 1.8
  Group = -> [C_element047,F_element011,I_element002]
  conduct = 2
  density = 1
  expand = 3
  formula = G4_FREON-13I1
  name = G4_FREON-13I1
  specific = 4
FEATURE [App::DocumentObjectGroupPython] Gd_element001  label="Gd_element : 2"  # scripted group (container) (typed FeaturePython)
  n = 2
  ref = Gd_element
FEATURE [App::DocumentObjectGroupPython] O_element041  label="O_element : 021"  # scripted group (container) (typed FeaturePython)
  n = 2
  ref = O_element
FEATURE [App::DocumentObjectGroupPython] S_element012  label="S_element : 004"  # scripted group (container) (typed FeaturePython)
  n = 1
  ref = S_element
FEATURE [App::DocumentObjectGroupPython] G4_GADOLINIUM_OXYSULFIDE  # scripted group (container) (typed FeaturePython)
  Dunit = g/cm3
  Dvalue = 7.44
  Group = -> [Gd_element001,O_element041,S_element012]
  conduct = 2
  density = 1
  expand = 3
  formula = G4_GADOLINIUM_OXYSULFIDE
  name = G4_GADOLINIUM_OXYSULFIDE
  specific = 4
FEATURE [App::DocumentObjectGroupPython] Ga_element001  label="Ga_element : 1"  # scripted group (container) (typed FeaturePython)
  n = 1
  ref = Ga_element
FEATURE [App::DocumentObjectGroupPython] As_element001  label="As_element : 1"  # scripted group (container) (typed FeaturePython)
  n = 1
  ref = As_element
FEATURE [App::DocumentObjectGroupPython] G4_GALLIUM_ARSENIDE  # scripted group (container) (typed FeaturePython)
  Dunit = g/cm3
  Dvalue = 5.31
  Group = -> [Ga_element001,As_element001]
  conduct = 2
  density = 1
  expand = 3
  formula = G4_GALLIUM_ARSENIDE
  name = G4_GALLIUM_ARSENIDE
  specific = 4
FEATURE [App::DocumentObjectGroupPython] H_element041  label="H_element : 0.081"  # scripted group (container) (typed FeaturePython)
  n = 0.08118
FEATURE [App::DocumentObjectGroupPython] C_element048  label="C_element : 0.416"  # scripted group (container) (typed FeaturePython)
  n = 0.41606
FEATURE [App::DocumentObjectGroupPython] N_element018  label="N_element : 0.111"  # scripted group (container) (typed FeaturePython)
  n = 0.11124
FEATURE [App::DocumentObjectGroupPython] O_element042  label="O_element : 0.381"  # scripted group (container) (typed FeaturePython)
  n = 0.38064
FEATURE [App::DocumentObjectGroupPython] S_element013  label="S_element : 0.011"  # scripted group (container) (typed FeaturePython)
  n = 0.01088
FEATURE [App::DocumentObjectGroupPython] G4_GEL_PHOTO_EMULSION  # scripted group (container) (typed FeaturePython)
  Dunit = g/cm3
  Dvalue = 1.2914
  Group = -> [H_element041,C_element048,N_element018,O_element042,S_element013]
  conduct = 2
  density = 1
  expand = 3
  formula = G4_GEL_PHOTO_EMULSION
  name = G4_GEL_PHOTO_EMULSION
  specific = 4
FEATURE [App::DocumentObjectGroupPython] B_element004  label="B_element : 0.040"  # scripted group (container) (typed FeaturePython)
  n = 0.0400639
FEATURE [App::DocumentObjectGroupPython] O_element043  label="O_element : 0.540"  # scripted group (container) (typed FeaturePython)
  n = 0.539561
FEATURE [App::DocumentObjectGroupPython] Na_element008  label="Na_element : 0.028"  # scripted group (container) (typed FeaturePython)
  n = 0.0281909
FEATURE [App::DocumentObjectGroupPython] Al_element003  label="Al_element : 0.012"  # scripted group (container) (typed FeaturePython)
  n = 0.011644
FEATURE [App::DocumentObjectGroupPython] Si_element003  label="Si_element : 0.377"  # scripted group (container) (typed FeaturePython)
  n = 0.377219
FEATURE [App::DocumentObjectGroupPython] K_element004  label="K_element : 0.014"  # scripted group (container) (typed FeaturePython)
  n = 0.00332099
FEATURE [App::DocumentObjectGroupPython] G4_Pyrex_Glass  # scripted group (container) (typed FeaturePython)
  Dunit = g/cm3
  Dvalue = 2.23
  Group = -> [B_element004,O_element043,Na_element008,Al_element003,Si_element003,K_element004]
  conduct = 2
  density = 1
  expand = 3
  formula = G4_Pyrex_Glass
  name = G4_Pyrex_Glass
  specific = 4
FEATURE [App::DocumentObjectGroupPython] O_element044  label="O_element : 0.156"  # scripted group (container) (typed FeaturePython)
  n = 0.156453
FEATURE [App::DocumentObjectGroupPython] Si_element004  label="Si_element : 0.081"  # scripted group (container) (typed FeaturePython)
  n = 0.080866
FEATURE [App::DocumentObjectGroupPython] Ti_element001  label="Ti_element : 0.008"  # scripted group (container) (typed FeaturePython)
  n = 0.008092
FEATURE [App::DocumentObjectGroupPython] As_element002  label="As_element : 0.003"  # scripted group (container) (typed FeaturePython)
  n = 0.002651
FEATURE [App::DocumentObjectGroupPython] Pb_element001  label="Pb_element : 0.752"  # scripted group (container) (typed FeaturePython)
  n = 0.751938
FEATURE [App::DocumentObjectGroupPython] G4_GLASS_LEAD  # scripted group (container) (typed FeaturePython)
  Dunit = g/cm3
  Dvalue = 6.22
  Group = -> [O_element044,Si_element004,Ti_element001,As_element002,Pb_element001]
  conduct = 2
  density = 1
  expand = 3
  formula = G4_GLASS_LEAD
  name = G4_GLASS_LEAD
  specific = 4
FEATURE [App::DocumentObjectGroupPython] O_element045  label="O_element : 0.460"  # scripted group (container) (typed FeaturePython)
  n = 0.4598
FEATURE [App::DocumentObjectGroupPython] Na_element009  label="Na_element : 0.096"  # scripted group (container) (typed FeaturePython)
  n = 0.0964411
FEATURE [App::DocumentObjectGroupPython] Si_element005  label="Si_element : 0.378"  # scripted group (container) (typed FeaturePython)
  n = 0.336553
FEATURE [App::DocumentObjectGroupPython] Ca_element011  label="Ca_element : 0.107"  # scripted group (container) (typed FeaturePython)
  n = 0.107205
FEATURE [App::DocumentObjectGroupPython] G4_GLASS_PLATE  # scripted group (container) (typed FeaturePython)
  Dunit = g/cm3
  Dvalue = 2.4
  Group = -> [O_element045,Na_element009,Si_element005,Ca_element011]
  conduct = 2
  density = 1
  expand = 3
  formula = G4_GLASS_PLATE
  name = G4_GLASS_PLATE
  specific = 4
FEATURE [App::DocumentObjectGroupPython] C_element049  label="C_element : 026"  # scripted group (container) (typed FeaturePython)
  n = 5
  ref = C_element
FEATURE [App::DocumentObjectGroupPython] H_element042  label="H_element : 021"  # scripted group (container) (typed FeaturePython)
  n = 10
  ref = H_element
FEATURE [App::DocumentObjectGroupPython] N_element019  label="N_element : 2"  # scripted group (container) (typed FeaturePython)
  n = 2
  ref = N_element
FEATURE [App::DocumentObjectGroupPython] O_element046  label="O_element : 022"  # scripted group (container) (typed FeaturePython)
  n = 3
  ref = O_element
FEATURE [App::DocumentObjectGroupPython] G4_GLUTAMINE  # scripted group (container) (typed FeaturePython)
  Dunit = g/cm3
  Dvalue = 1.46
  Group = -> [C_element049,H_element042,N_element019,O_element046]
  conduct = 2
  density = 1
  expand = 3
  formula = G4_GLUTAMINE
  name = G4_GLUTAMINE
  specific = 4
FEATURE [App::DocumentObjectGroupPython] C_element050  label="C_element : 027"  # scripted group (container) (typed FeaturePython)
  n = 3
  ref = C_element
FEATURE [App::DocumentObjectGroupPython] H_element043  label="H_element : 022"  # scripted group (container) (typed FeaturePython)
  n = 8
  ref = H_element
FEATURE [App::DocumentObjectGroupPython] O_element047  label="O_element : 023"  # scripted group (container) (typed FeaturePython)
  n = 3
  ref = O_element
FEATURE [App::DocumentObjectGroupPython] G4_GLYCEROL  # scripted group (container) (typed FeaturePython)
  Dunit = g/cm3
  Dvalue = 1.2613
  Group = -> [C_element050,H_element043,O_element047]
  conduct = 2
  density = 1
  expand = 3
  formula = G4_GLYCEROL
  name = G4_GLYCEROL
  specific = 4
FEATURE [App::DocumentObjectGroupPython] C_element051  label="C_element : 028"  # scripted group (container) (typed FeaturePython)
  n = 5
  ref = C_element
FEATURE [App::DocumentObjectGroupPython] H_element044  label="H_element : 023"  # scripted group (container) (typed FeaturePython)
  n = 5
  ref = H_element
FEATURE [App::DocumentObjectGroupPython] N_element020  label="N_element : 009"  # scripted group (container) (typed FeaturePython)
  n = 5
  ref = N_element
FEATURE [App::DocumentObjectGroupPython] O_element048  label="O_element : 024"  # scripted group (container) (typed FeaturePython)
  n = 1
  ref = O_element
FEATURE [App::DocumentObjectGroupPython] G4_GUANINE  # scripted group (container) (typed FeaturePython)
  Dunit = g/cm3
  Dvalue = 2.2
  Group = -> [C_element051,H_element044,N_element020,O_element048]
  conduct = 2
  density = 1
  expand = 3
  formula = G4_GUANINE
  name = G4_GUANINE
  specific = 4
FEATURE [App::DocumentObjectGroupPython] Ca_element012  label="Ca_element : 006"  # scripted group (container) (typed FeaturePython)
  n = 1
  ref = Ca_element
FEATURE [App::DocumentObjectGroupPython] S_element014  label="S_element : 005"  # scripted group (container) (typed FeaturePython)
  n = 1
  ref = S_element
FEATURE [App::DocumentObjectGroupPython] O_element049  label="O_element : 6"  # scripted group (container) (typed FeaturePython)
  n = 6
  ref = O_element
FEATURE [App::DocumentObjectGroupPython] H_element045  label="H_element : 024"  # scripted group (container) (typed FeaturePython)
  n = 4
  ref = H_element
FEATURE [App::DocumentObjectGroupPython] G4_GYPSUM  # scripted group (container) (typed FeaturePython)
  Dunit = g/cm3
  Dvalue = 2.32
  Group = -> [Ca_element012,S_element014,O_element049,H_element045]
  conduct = 2
  density = 1
  expand = 3
  formula = G4_GYPSUM
  name = G4_GYPSUM
  specific = 4
FEATURE [App::DocumentObjectGroupPython] C_element052  label="C_element : 7"  # scripted group (container) (typed FeaturePython)
  n = 7
  ref = C_element
FEATURE [App::DocumentObjectGroupPython] H_element046  label="H_element : 16"  # scripted group (container) (typed FeaturePython)
  n = 16
  ref = H_element
FEATURE [App::DocumentObjectGroupPython] G4_N_HEPTANE  label="G4_N-HEPTANE"  # scripted group (container) (typed FeaturePython)
  Dunit = g/cm3
  Dvalue = 0.68376
  Group = -> [C_element052,H_element046]
  conduct = 2
  density = 1
  expand = 3
  formula = G4_N-HEPTANE
  name = G4_N-HEPTANE
  specific = 4
FEATURE [App::DocumentObjectGroupPython] C_element053  label="C_element : 029"  # scripted group (container) (typed FeaturePython)
  n = 6
  ref = C_element
FEATURE [App::DocumentObjectGroupPython] H_element047  label="H_element : 14"  # scripted group (container) (typed FeaturePython)
  n = 14
  ref = H_element
FEATURE [App::DocumentObjectGroupPython] G4_N_HEXANE  label="G4_N-HEXANE"  # scripted group (container) (typed FeaturePython)
  Dunit = g/cm3
  Dvalue = 0.6603
  Group = -> [C_element053,H_element047]
  conduct = 2
  density = 1
  expand = 3
  formula = G4_N-HEXANE
  name = G4_N-HEXANE
  specific = 4
FEATURE [App::DocumentObjectGroupPython] C_element054  label="C_element : 22"  # scripted group (container) (typed FeaturePython)
  n = 22
  ref = C_element
FEATURE [App::DocumentObjectGroupPython] H_element048  label="H_element : 025"  # scripted group (container) (typed FeaturePython)
  n = 10
  ref = H_element
FEATURE [App::DocumentObjectGroupPython] N_element021  label="N_element : 010"  # scripted group (container) (typed FeaturePython)
  n = 2
  ref = N_element
FEATURE [App::DocumentObjectGroupPython] O_element050  label="O_element : 025"  # scripted group (container) (typed FeaturePython)
  n = 5
  ref = O_element
FEATURE [App::DocumentObjectGroupPython] G4_KAPTON  # scripted group (container) (typed FeaturePython)
  Dunit = g/cm3
  Dvalue = 1.42
  Group = -> [C_element054,H_element048,N_element021,O_element050]
  conduct = 2
  density = 1
  expand = 3
  formula = G4_KAPTON
  name = G4_KAPTON
  specific = 4
FEATURE [App::DocumentObjectGroupPython] La_element001  label="La_element : 1"  # scripted group (container) (typed FeaturePython)
  n = 1
  ref = La_element
FEATURE [App::DocumentObjectGroupPython] Br_element003  label="Br_element : 002"  # scripted group (container) (typed FeaturePython)
  n = 1
  ref = Br_element
FEATURE [App::DocumentObjectGroupPython] O_element051  label="O_element : 026"  # scripted group (container) (typed FeaturePython)
  n = 1
  ref = O_element
FEATURE [App::DocumentObjectGroupPython] G4_LANTHANUM_OXYBROMIDE  # scripted group (container) (typed FeaturePython)
  Dunit = g/cm3
  Dvalue = 6.28
  Group = -> [La_element001,Br_element003,O_element051]
  conduct = 2
  density = 1
  expand = 3
  formula = G4_LANTHANUM_OXYBROMIDE
  name = G4_LANTHANUM_OXYBROMIDE
  specific = 4
FEATURE [App::DocumentObjectGroupPython] La_element002  label="La_element : 2"  # scripted group (container) (typed FeaturePython)
  n = 2
  ref = La_element
FEATURE [App::DocumentObjectGroupPython] O_element052  label="O_element : 027"  # scripted group (container) (typed FeaturePython)
  n = 2
  ref = O_element
FEATURE [App::DocumentObjectGroupPython] S_element015  label="S_element : 006"  # scripted group (container) (typed FeaturePython)
  n = 1
  ref = S_element
FEATURE [App::DocumentObjectGroupPython] G4_LANTHANUM_OXYSULFIDE  # scripted group (container) (typed FeaturePython)
  Dunit = g/cm3
  Dvalue = 5.86
  Group = -> [La_element002,O_element052,S_element015]
  conduct = 2
  density = 1
  expand = 3
  formula = G4_LANTHANUM_OXYSULFIDE
  name = G4_LANTHANUM_OXYSULFIDE
  specific = 4
FEATURE [App::DocumentObjectGroupPython] O_element053  label="O_element : 0.072"  # scripted group (container) (typed FeaturePython)
  n = 0.071682
FEATURE [App::DocumentObjectGroupPython] Pb_element002  label="Pb_element : 0.928"  # scripted group (container) (typed FeaturePython)
  n = 0.928318
FEATURE [App::DocumentObjectGroupPython] G4_LEAD_OXIDE  # scripted group (container) (typed FeaturePython)
  Dunit = g/cm3
  Dvalue = 9.53
  Group = -> [O_element053,Pb_element002]
  conduct = 2
  density = 1
  expand = 3
  formula = G4_LEAD_OXIDE
  name = G4_LEAD_OXIDE
  specific = 4
FEATURE [App::DocumentObjectGroupPython] Li_element001  label="Li_element : 1"  # scripted group (container) (typed FeaturePython)
  n = 1
  ref = Li_element
FEATURE [App::DocumentObjectGroupPython] N_element022  label="N_element : 011"  # scripted group (container) (typed FeaturePython)
  n = 1
  ref = N_element
FEATURE [App::DocumentObjectGroupPython] H_element049  label="H_element : 026"  # scripted group (container) (typed FeaturePython)
  n = 2
  ref = H_element
FEATURE [App::DocumentObjectGroupPython] G4_LITHIUM_AMIDE  # scripted group (container) (typed FeaturePython)
  Dunit = g/cm3
  Dvalue = 1.178
  Group = -> [Li_element001,N_element022,H_element049]
  conduct = 2
  density = 1
  expand = 3
  formula = G4_LITHIUM_AMIDE
  name = G4_LITHIUM_AMIDE
  specific = 4
FEATURE [App::DocumentObjectGroupPython] Li_element002  label="Li_element : 2"  # scripted group (container) (typed FeaturePython)
  n = 2
  ref = Li_element
FEATURE [App::DocumentObjectGroupPython] C_element055  label="C_element : 030"  # scripted group (container) (typed FeaturePython)
  n = 1
  ref = C_element
FEATURE [App::DocumentObjectGroupPython] O_element054  label="O_element : 028"  # scripted group (container) (typed FeaturePython)
  n = 3
  ref = O_element
FEATURE [App::DocumentObjectGroupPython] G4_LITHIUM_CARBONATE  # scripted group (container) (typed FeaturePython)
  Dunit = g/cm3
  Dvalue = 2.11
  Group = -> [Li_element002,C_element055,O_element054]
  conduct = 2
  density = 1
  expand = 3
  formula = G4_LITHIUM_CARBONATE
  name = G4_LITHIUM_CARBONATE
  specific = 4
FEATURE [App::DocumentObjectGroupPython] Li_element003  label="Li_element : 003"  # scripted group (container) (typed FeaturePython)
  n = 1
  ref = Li_element
FEATURE [App::DocumentObjectGroupPython] F_element012  label="F_element : 004"  # scripted group (container) (typed FeaturePython)
  n = 1
  ref = F_element
FEATURE [App::DocumentObjectGroupPython] G4_LITHIUM_FLUORIDE  # scripted group (container) (typed FeaturePython)
  Dunit = g/cm3
  Dvalue = 2.635
  Group = -> [Li_element003,F_element012]
  conduct = 2
  density = 1
  expand = 3
  formula = G4_LITHIUM_FLUORIDE
  name = G4_LITHIUM_FLUORIDE
  specific = 4
FEATURE [App::DocumentObjectGroupPython] Li_element004  label="Li_element : 004"  # scripted group (container) (typed FeaturePython)
  n = 1
  ref = Li_element
FEATURE [App::DocumentObjectGroupPython] H_element050  label="H_element : 027"  # scripted group (container) (typed FeaturePython)
  n = 1
  ref = H_element
FEATURE [App::DocumentObjectGroupPython] G4_LITHIUM_HYDRIDE  # scripted group (container) (typed FeaturePython)
  Dunit = g/cm3
  Dvalue = 0.82
  Group = -> [Li_element004,H_element050]
  conduct = 2
  density = 1
  expand = 3
  formula = G4_LITHIUM_HYDRIDE
  name = G4_LITHIUM_HYDRIDE
  specific = 4
FEATURE [App::DocumentObjectGroupPython] Li_element005  label="Li_element : 005"  # scripted group (container) (typed FeaturePython)
  n = 1
  ref = Li_element
FEATURE [App::DocumentObjectGroupPython] I_element003  label="I_element : 002"  # scripted group (container) (typed FeaturePython)
  n = 1
  ref = I_element
FEATURE [App::DocumentObjectGroupPython] G4_LITHIUM_IODIDE  # scripted group (container) (typed FeaturePython)
  Dunit = g/cm3
  Dvalue = 3.494
  Group = -> [Li_element005,I_element003]
  conduct = 2
  density = 1
  expand = 3
  formula = G4_LITHIUM_IODIDE
  name = G4_LITHIUM_IODIDE
  specific = 4
FEATURE [App::DocumentObjectGroupPython] Li_element006  label="Li_element : 006"  # scripted group (container) (typed FeaturePython)
  n = 2
  ref = Li_element
FEATURE [App::DocumentObjectGroupPython] O_element055  label="O_element : 029"  # scripted group (container) (typed FeaturePython)
  n = 1
  ref = O_element
FEATURE [App::DocumentObjectGroupPython] G4_LITHIUM_OXIDE  # scripted group (container) (typed FeaturePython)
  Dunit = g/cm3
  Dvalue = 2.013
  Group = -> [Li_element006,O_element055]
  conduct = 2
  density = 1
  expand = 3
  formula = G4_LITHIUM_OXIDE
  name = G4_LITHIUM_OXIDE
  specific = 4
FEATURE [App::DocumentObjectGroupPython] Li_element007  label="Li_element : 007"  # scripted group (container) (typed FeaturePython)
  n = 2
  ref = Li_element
FEATURE [App::DocumentObjectGroupPython] B_element005  label="B_element : 005"  # scripted group (container) (typed FeaturePython)
  n = 4
  ref = B_element
FEATURE [App::DocumentObjectGroupPython] O_element056  label="O_element : 7"  # scripted group (container) (typed FeaturePython)
  n = 7
  ref = O_element
FEATURE [App::DocumentObjectGroupPython] G4_LITHIUM_TETRABORATE  # scripted group (container) (typed FeaturePython)
  Dunit = g/cm3
  Dvalue = 2.44
  Group = -> [Li_element007,B_element005,O_element056]
  conduct = 2
  density = 1
  expand = 3
  formula = G4_LITHIUM_TETRABORATE
  name = G4_LITHIUM_TETRABORATE
  specific = 4
FEATURE [App::DocumentObjectGroupPython] H_element051  label="H_element : 0.105"  # scripted group (container) (typed FeaturePython)
  n = 0.105
FEATURE [App::DocumentObjectGroupPython] C_element056  label="C_element : 0.083"  # scripted group (container) (typed FeaturePython)
  n = 0.083
FEATURE [App::DocumentObjectGroupPython] N_element023  label="N_element : 0.023"  # scripted group (container) (typed FeaturePython)
  n = 0.023
FEATURE [App::DocumentObjectGroupPython] O_element057  label="O_element : 0.779"  # scripted group (container) (typed FeaturePython)
  n = 0.779
FEATURE [App::DocumentObjectGroupPython] Na_element010  label="Na_element : 0.097"  # scripted group (container) (typed FeaturePython)
  n = 0.002
FEATURE [App::DocumentObjectGroupPython] P_element006  label="P_element : 0.105"  # scripted group (container) (typed FeaturePython)
  n = 0.001
FEATURE [App::DocumentObjectGroupPython] S_element016  label="S_element : 0.017"  # scripted group (container) (typed FeaturePython)
  n = 0.002
FEATURE [App::DocumentObjectGroupPython] Cl_element014  label="Cl_element : 0.587"  # scripted group (container) (typed FeaturePython)
  n = 0.003
FEATURE [App::DocumentObjectGroupPython] K_element005  label="K_element : 0.015"  # scripted group (container) (typed FeaturePython)
  n = 0.002
FEATURE [App::DocumentObjectGroupPython] G4_LUNG_ICRP  # scripted group (container) (typed FeaturePython)
  Dunit = g/cm3
  Dvalue = 1.04
  Group = -> [H_element051,C_element056,N_element023,O_element057,Na_element010,P_element006,S_element016,Cl_element014,K_element005]
  conduct = 2
  density = 1
  expand = 3
  formula = G4_LUNG_ICRP
  name = G4_LUNG_ICRP
  specific = 4
FEATURE [App::DocumentObjectGroupPython] H_element052  label="H_element : 0.116"  # scripted group (container) (typed FeaturePython)
  n = 0.114318
FEATURE [App::DocumentObjectGroupPython] C_element057  label="C_element : 0.656"  # scripted group (container) (typed FeaturePython)
  n = 0.655824
FEATURE [App::DocumentObjectGroupPython] O_element058  label="O_element : 0.092"  # scripted group (container) (typed FeaturePython)
  n = 0.0921831
FEATURE [App::DocumentObjectGroupPython] Mg_element004  label="Mg_element : 0.135"  # scripted group (container) (typed FeaturePython)
  n = 0.134792
FEATURE [App::DocumentObjectGroupPython] Ca_element013  label="Ca_element : 0.003"  # scripted group (container) (typed FeaturePython)
  n = 0.002883
FEATURE [App::DocumentObjectGroupPython] G4_M3_WAX  # scripted group (container) (typed FeaturePython)
  Dunit = g/cm3
  Dvalue = 1.05
  Group = -> [H_element052,C_element057,O_element058,Mg_element004,Ca_element013]
  conduct = 2
  density = 1
  expand = 3
  formula = G4_M3_WAX
  name = G4_M3_WAX
  specific = 4
FEATURE [App::DocumentObjectGroupPython] Mg_element005  label="Mg_element : 1"  # scripted group (container) (typed FeaturePython)
  n = 1
  ref = Mg_element
FEATURE [App::DocumentObjectGroupPython] C_element058  label="C_element : 031"  # scripted group (container) (typed FeaturePython)
  n = 1
  ref = C_element
FEATURE [App::DocumentObjectGroupPython] O_element059  label="O_element : 030"  # scripted group (container) (typed FeaturePython)
  n = 3
  ref = O_element
FEATURE [App::DocumentObjectGroupPython] G4_MAGNESIUM_CARBONATE  # scripted group (container) (typed FeaturePython)
  Dunit = g/cm3
  Dvalue = 2.958
  Group = -> [Mg_element005,C_element058,O_element059]
  conduct = 2
  density = 1
  expand = 3
  formula = G4_MAGNESIUM_CARBONATE
  name = G4_MAGNESIUM_CARBONATE
  specific = 4
FEATURE [App::DocumentObjectGroupPython] Mg_element006  label="Mg_element : 002"  # scripted group (container) (typed FeaturePython)
  n = 1
  ref = Mg_element
FEATURE [App::DocumentObjectGroupPython] F_element013  label="F_element : 005"  # scripted group (container) (typed FeaturePython)
  n = 2
  ref = F_element
FEATURE [App::DocumentObjectGroupPython] G4_MAGNESIUM_FLUORIDE  # scripted group (container) (typed FeaturePython)
  Dunit = g/cm3
  Dvalue = 3
  Group = -> [Mg_element006,F_element013]
  conduct = 2
  density = 1
  expand = 3
  formula = G4_MAGNESIUM_FLUORIDE
  name = G4_MAGNESIUM_FLUORIDE
  specific = 4
FEATURE [App::DocumentObjectGroupPython] Mg_element007  label="Mg_element : 003"  # scripted group (container) (typed FeaturePython)
  n = 1
  ref = Mg_element
FEATURE [App::DocumentObjectGroupPython] O_element060  label="O_element : 031"  # scripted group (container) (typed FeaturePython)
  n = 1
  ref = O_element
FEATURE [App::DocumentObjectGroupPython] G4_MAGNESIUM_OXIDE  # scripted group (container) (typed FeaturePython)
  Dunit = g/cm3
  Dvalue = 3.58
  Group = -> [Mg_element007,O_element060]
  conduct = 2
  density = 1
  expand = 3
  formula = G4_MAGNESIUM_OXIDE
  name = G4_MAGNESIUM_OXIDE
  specific = 4
FEATURE [App::DocumentObjectGroupPython] Mg_element008  label="Mg_element : 004"  # scripted group (container) (typed FeaturePython)
  n = 1
  ref = Mg_element
FEATURE [App::DocumentObjectGroupPython] B_element006  label="B_element : 006"  # scripted group (container) (typed FeaturePython)
  n = 4
  ref = B_element
FEATURE [App::DocumentObjectGroupPython] O_element061  label="O_element : 032"  # scripted group (container) (typed FeaturePython)
  n = 7
  ref = O_element
FEATURE [App::DocumentObjectGroupPython] G4_MAGNESIUM_TETRABORATE  # scripted group (container) (typed FeaturePython)
  Dunit = g/cm3
  Dvalue = 2.53
  Group = -> [Mg_element008,B_element006,O_element061]
  conduct = 2
  density = 1
  expand = 3
  formula = G4_MAGNESIUM_TETRABORATE
  name = G4_MAGNESIUM_TETRABORATE
  specific = 4
FEATURE [App::DocumentObjectGroupPython] Hg_element001  label="Hg_element : 1"  # scripted group (container) (typed FeaturePython)
  n = 1
  ref = Hg_element
FEATURE [App::DocumentObjectGroupPython] I_element004  label="I_element : 2"  # scripted group (container) (typed FeaturePython)
  n = 2
  ref = I_element
FEATURE [App::DocumentObjectGroupPython] G4_MERCURIC_IODIDE  # scripted group (container) (typed FeaturePython)
  Dunit = g/cm3
  Dvalue = 6.36
  Group = -> [Hg_element001,I_element004]
  conduct = 2
  density = 1
  expand = 3
  formula = G4_MERCURIC_IODIDE
  name = G4_MERCURIC_IODIDE
  specific = 4
FEATURE [App::DocumentObjectGroupPython] C_element059  label="C_element : 032"  # scripted group (container) (typed FeaturePython)
  n = 1
  ref = C_element
FEATURE [App::DocumentObjectGroupPython] H_element053  label="H_element : 028"  # scripted group (container) (typed FeaturePython)
  n = 4
  ref = H_element
FEATURE [App::DocumentObjectGroupPython] G4_METHANE  # scripted group (container) (typed FeaturePython)
  Dunit = g/cm3
  Dvalue = 0.000667151
  Group = -> [C_element059,H_element053]
  conduct = 2
  density = 1
  expand = 3
  formula = G4_METHANE
  name = G4_METHANE
  specific = 4
FEATURE [App::DocumentObjectGroupPython] C_element060  label="C_element : 033"  # scripted group (container) (typed FeaturePython)
  n = 1
  ref = C_element
FEATURE [App::DocumentObjectGroupPython] H_element054  label="H_element : 029"  # scripted group (container) (typed FeaturePython)
  n = 4
  ref = H_element
FEATURE [App::DocumentObjectGroupPython] O_element062  label="O_element : 033"  # scripted group (container) (typed FeaturePython)
  n = 1
  ref = O_element
FEATURE [App::DocumentObjectGroupPython] G4_METHANOL  # scripted group (container) (typed FeaturePython)
  Dunit = g/cm3
  Dvalue = 0.7914
  Group = -> [C_element060,H_element054,O_element062]
  conduct = 2
  density = 1
  expand = 3
  formula = G4_METHANOL
  name = G4_METHANOL
  specific = 4
FEATURE [App::DocumentObjectGroupPython] H_element055  label="H_element : 0.134"  # scripted group (container) (typed FeaturePython)
  n = 0.13404
FEATURE [App::DocumentObjectGroupPython] C_element061  label="C_element : 0.778"  # scripted group (container) (typed FeaturePython)
  n = 0.77796
FEATURE [App::DocumentObjectGroupPython] O_element063  label="O_element : 0.035"  # scripted group (container) (typed FeaturePython)
  n = 0.03502
FEATURE [App::DocumentObjectGroupPython] Mg_element009  label="Mg_element : 0.039"  # scripted group (container) (typed FeaturePython)
  n = 0.038594
FEATURE [App::DocumentObjectGroupPython] Ti_element002  label="Ti_element : 0.014"  # scripted group (container) (typed FeaturePython)
  n = 0.014386
FEATURE [App::DocumentObjectGroupPython] G4_MIX_D_WAX  # scripted group (container) (typed FeaturePython)
  Dunit = g/cm3
  Dvalue = 0.99
  Group = -> [H_element055,C_element061,O_element063,Mg_element009,Ti_element002]
  conduct = 2
  density = 1
  expand = 3
  formula = G4_MIX_D_WAX
  name = G4_MIX_D_WAX
  specific = 4
FEATURE [App::DocumentObjectGroupPython] H_element056  label="H_element : 0.135"  # scripted group (container) (typed FeaturePython)
  n = 0.081192
FEATURE [App::DocumentObjectGroupPython] C_element062  label="C_element : 0.583"  # scripted group (container) (typed FeaturePython)
  n = 0.583442
FEATURE [App::DocumentObjectGroupPython] N_element024  label="N_element : 0.018"  # scripted group (container) (typed FeaturePython)
  n = 0.017798
FEATURE [App::DocumentObjectGroupPython] O_element064  label="O_element : 0.186"  # scripted group (container) (typed FeaturePython)
  n = 0.186381
FEATURE [App::DocumentObjectGroupPython] Mg_element010  label="Mg_element : 0.130"  # scripted group (container) (typed FeaturePython)
  n = 0.130287
FEATURE [App::DocumentObjectGroupPython] Cl_element015  label="Cl_element : 0.588"  # scripted group (container) (typed FeaturePython)
  n = 0.0009
FEATURE [App::DocumentObjectGroupPython] G4_MS20_TISSUE  # scripted group (container) (typed FeaturePython)
  Dunit = g/cm3
  Dvalue = 1
  Group = -> [H_element056,C_element062,N_element024,O_element064,Mg_element010,Cl_element015]
  conduct = 2
  density = 1
  expand = 3
  formula = G4_MS20_TISSUE
  name = G4_MS20_TISSUE
  specific = 4
FEATURE [App::DocumentObjectGroupPython] H_element057  label="H_element : 0.136"  # scripted group (container) (typed FeaturePython)
  n = 0.102
FEATURE [App::DocumentObjectGroupPython] C_element063  label="C_element : 0.143"  # scripted group (container) (typed FeaturePython)
  n = 0.143
FEATURE [App::DocumentObjectGroupPython] N_element025  label="N_element : 0.034"  # scripted group (container) (typed FeaturePython)
  n = 0.034
FEATURE [App::DocumentObjectGroupPython] O_element065  label="O_element : 0.710"  # scripted group (container) (typed FeaturePython)
  n = 0.71
FEATURE [App::DocumentObjectGroupPython] Na_element011  label="Na_element : 0.098"  # scripted group (container) (typed FeaturePython)
  n = 0.001
FEATURE [App::DocumentObjectGroupPython] P_element007  label="P_element : 0.002"  # scripted group (container) (typed FeaturePython)
  n = 0.002
FEATURE [App::DocumentObjectGroupPython] S_element017  label="S_element : 0.018"  # scripted group (container) (typed FeaturePython)
  n = 0.003
FEATURE [App::DocumentObjectGroupPython] Cl_element016  label="Cl_element : 0.589"  # scripted group (container) (typed FeaturePython)
  n = 0.001
FEATURE [App::DocumentObjectGroupPython] K_element006  label="K_element : 0.004"  # scripted group (container) (typed FeaturePython)
  n = 0.004
FEATURE [App::DocumentObjectGroupPython] G4_MUSCLE_SKELETAL_ICRP  # scripted group (container) (typed FeaturePython)
  Dunit = g/cm3
  Dvalue = 1.05
  Group = -> [H_element057,C_element063,N_element025,O_element065,Na_element011,P_element007,S_element017,Cl_element016,K_element006]
  conduct = 2
  density = 1
  expand = 3
  formula = G4_MUSCLE_SKELETAL_ICRP
  name = G4_MUSCLE_SKELETAL_ICRP
  specific = 4
FEATURE [App::DocumentObjectGroupPython] H_element058  label="H_element : 0.137"  # scripted group (container) (typed FeaturePython)
  n = 0.102102
FEATURE [App::DocumentObjectGroupPython] C_element064  label="C_element : 0.123"  # scripted group (container) (typed FeaturePython)
  n = 0.123123
FEATURE [App::DocumentObjectGroupPython] N_element026  label="N_element : 0.756"  # scripted group (container) (typed FeaturePython)
  n = 0.035035
FEATURE [App::DocumentObjectGroupPython] O_element066  label="O_element : 0.730"  # scripted group (container) (typed FeaturePython)
  n = 0.72973
FEATURE [App::DocumentObjectGroupPython] Na_element012  label="Na_element : 0.099"  # scripted group (container) (typed FeaturePython)
  n = 0.001001
FEATURE [App::DocumentObjectGroupPython] P_element008  label="P_element : 0.106"  # scripted group (container) (typed FeaturePython)
  n = 0.002002
FEATURE [App::DocumentObjectGroupPython] S_element018  label="S_element : 0.019"  # scripted group (container) (typed FeaturePython)
  n = 0.004004
FEATURE [App::DocumentObjectGroupPython] K_element007  label="K_element : 0.016"  # scripted group (container) (typed FeaturePython)
  n = 0.003003
FEATURE [App::DocumentObjectGroupPython] G4_MUSCLE_STRIATED_ICRU  # scripted group (container) (typed FeaturePython)
  Dunit = g/cm3
  Dvalue = 1.04
  Group = -> [H_element058,C_element064,N_element026,O_element066,Na_element012,P_element008,S_element018,K_element007]
  conduct = 2
  density = 1
  expand = 3
  formula = G4_MUSCLE_STRIATED_ICRU
  name = G4_MUSCLE_STRIATED_ICRU
  specific = 4
FEATURE [App::DocumentObjectGroupPython] H_element059  label="H_element : 0.098"  # scripted group (container) (typed FeaturePython)
  n = 0.0982341
FEATURE [App::DocumentObjectGroupPython] C_element065  label="C_element : 0.156"  # scripted group (container) (typed FeaturePython)
  n = 0.156214
FEATURE [App::DocumentObjectGroupPython] N_element027  label="N_element : 0.757"  # scripted group (container) (typed FeaturePython)
  n = 0.035451
FEATURE [App::DocumentObjectGroupPython] O_element067  label="O_element : 0.880"  # scripted group (container) (typed FeaturePython)
  n = 0.710101
FEATURE [App::DocumentObjectGroupPython] G4_MUSCLE_WITH_SUCROSE  # scripted group (container) (typed FeaturePython)
  Dunit = g/cm3
  Dvalue = 1.11
  Group = -> [H_element059,C_element065,N_element027,O_element067]
  conduct = 2
  density = 1
  expand = 3
  formula = G4_MUSCLE_WITH_SUCROSE
  name = G4_MUSCLE_WITH_SUCROSE
  specific = 4
FEATURE [App::DocumentObjectGroupPython] H_element060  label="H_element : 0.138"  # scripted group (container) (typed FeaturePython)
  n = 0.101969
FEATURE [App::DocumentObjectGroupPython] C_element066  label="C_element : 0.120"  # scripted group (container) (typed FeaturePython)
  n = 0.120058
FEATURE [App::DocumentObjectGroupPython] N_element028  label="N_element : 0.758"  # scripted group (container) (typed FeaturePython)
  n = 0.035451
FEATURE [App::DocumentObjectGroupPython] O_element068  label="O_element : 0.743"  # scripted group (container) (typed FeaturePython)
  n = 0.742522
FEATURE [App::DocumentObjectGroupPython] G4_MUSCLE_WITHOUT_SUCROSE  # scripted group (container) (typed FeaturePython)
  Dunit = g/cm3
  Dvalue = 1.07
  Group = -> [H_element060,C_element066,N_element028,O_element068]
  conduct = 2
  density = 1
  expand = 3
  formula = G4_MUSCLE_WITHOUT_SUCROSE
  name = G4_MUSCLE_WITHOUT_SUCROSE
  specific = 4
FEATURE [App::DocumentObjectGroupPython] C_element067  label="C_element : 10"  # scripted group (container) (typed FeaturePython)
  n = 10
  ref = C_element
FEATURE [App::DocumentObjectGroupPython] H_element061  label="H_element : 030"  # scripted group (container) (typed FeaturePython)
  n = 8
  ref = H_element
FEATURE [App::DocumentObjectGroupPython] G4_NAPHTHALENE  # scripted group (container) (typed FeaturePython)
  Dunit = g/cm3
  Dvalue = 1.145
  Group = -> [C_element067,H_element061]
  conduct = 2
  density = 1
  expand = 3
  formula = G4_NAPHTHALENE
  name = G4_NAPHTHALENE
  specific = 4
FEATURE [App::DocumentObjectGroupPython] C_element068  label="C_element : 034"  # scripted group (container) (typed FeaturePython)
  n = 6
  ref = C_element
FEATURE [App::DocumentObjectGroupPython] H_element062  label="H_element : 031"  # scripted group (container) (typed FeaturePython)
  n = 5
  ref = H_element
FEATURE [App::DocumentObjectGroupPython] N_element029  label="N_element : 012"  # scripted group (container) (typed FeaturePython)
  n = 1
  ref = N_element
FEATURE [App::DocumentObjectGroupPython] O_element069  label="O_element : 034"  # scripted group (container) (typed FeaturePython)
  n = 2
  ref = O_element
FEATURE [App::DocumentObjectGroupPython] G4_NITROBENZENE  # scripted group (container) (typed FeaturePython)
  Dunit = g/cm3
  Dvalue = 1.19867
  Group = -> [C_element068,H_element062,N_element029,O_element069]
  conduct = 2
  density = 1
  expand = 3
  formula = G4_NITROBENZENE
  name = G4_NITROBENZENE
  specific = 4
FEATURE [App::DocumentObjectGroupPython] N_element030  label="N_element : 013"  # scripted group (container) (typed FeaturePython)
  n = 2
  ref = N_element
FEATURE [App::DocumentObjectGroupPython] O_element070  label="O_element : 035"  # scripted group (container) (typed FeaturePython)
  n = 1
  ref = O_element
FEATURE [App::DocumentObjectGroupPython] G4_NITROUS_OXIDE  # scripted group (container) (typed FeaturePython)
  Dunit = g/cm3
  Dvalue = 0.00183094
  Group = -> [N_element030,O_element070]
  conduct = 2
  density = 1
  expand = 3
  formula = G4_NITROUS_OXIDE
  name = G4_NITROUS_OXIDE
  specific = 4
FEATURE [App::DocumentObjectGroupPython] H_element063  label="H_element : 0.104"  # scripted group (container) (typed FeaturePython)
  n = 0.103509
FEATURE [App::DocumentObjectGroupPython] C_element069  label="C_element : 0.648"  # scripted group (container) (typed FeaturePython)
  n = 0.648416
FEATURE [App::DocumentObjectGroupPython] N_element031  label="N_element : 0.100"  # scripted group (container) (typed FeaturePython)
  n = 0.0995361
FEATURE [App::DocumentObjectGroupPython] O_element071  label="O_element : 0.149"  # scripted group (container) (typed FeaturePython)
  n = 0.148539
FEATURE [App::DocumentObjectGroupPython] G4_NYLON_8062  label="G4_NYLON-8062"  # scripted group (container) (typed FeaturePython)
  Dunit = g/cm3
  Dvalue = 1.08
  Group = -> [H_element063,C_element069,N_element031,O_element071]
  conduct = 2
  density = 1
  expand = 3
  formula = G4_NYLON-8062
  name = G4_NYLON-8062
  specific = 4
FEATURE [App::DocumentObjectGroupPython] C_element070  label="C_element : 035"  # scripted group (container) (typed FeaturePython)
  n = 6
  ref = C_element
FEATURE [App::DocumentObjectGroupPython] H_element064  label="H_element : 11"  # scripted group (container) (typed FeaturePython)
  n = 11
  ref = H_element
FEATURE [App::DocumentObjectGroupPython] N_element032  label="N_element : 014"  # scripted group (container) (typed FeaturePython)
  n = 1
  ref = N_element
FEATURE [App::DocumentObjectGroupPython] O_element072  label="O_element : 036"  # scripted group (container) (typed FeaturePython)
  n = 1
  ref = O_element
FEATURE [App::DocumentObjectGroupPython] G4_NYLON_6_6  label="G4_NYLON-6-6"  # scripted group (container) (typed FeaturePython)
  Dunit = g/cm3
  Dvalue = 1.14
  Group = -> [C_element070,H_element064,N_element032,O_element072]
  conduct = 2
  density = 1
  expand = 3
  formula = G4_NYLON-6-6
  name = G4_NYLON-6-6
  specific = 4
FEATURE [App::DocumentObjectGroupPython] H_element065  label="H_element : 0.139"  # scripted group (container) (typed FeaturePython)
  n = 0.107062
FEATURE [App::DocumentObjectGroupPython] C_element071  label="C_element : 0.680"  # scripted group (container) (typed FeaturePython)
  n = 0.680449
FEATURE [App::DocumentObjectGroupPython] N_element033  label="N_element : 0.099"  # scripted group (container) (typed FeaturePython)
  n = 0.099189
FEATURE [App::DocumentObjectGroupPython] O_element073  label="O_element : 0.113"  # scripted group (container) (typed FeaturePython)
  n = 0.1133
FEATURE [App::DocumentObjectGroupPython] G4_NYLON_6_10  label="G4_NYLON-6-10"  # scripted group (container) (typed FeaturePython)
  Dunit = g/cm3
  Dvalue = 1.14
  Group = -> [H_element065,C_element071,N_element033,O_element073]
  conduct = 2
  density = 1
  expand = 3
  formula = G4_NYLON-6-10
  name = G4_NYLON-6-10
  specific = 4
FEATURE [App::DocumentObjectGroupPython] H_element066  label="H_element : 0.140"  # scripted group (container) (typed FeaturePython)
  n = 0.115476
FEATURE [App::DocumentObjectGroupPython] C_element072  label="C_element : 0.721"  # scripted group (container) (typed FeaturePython)
  n = 0.720818
FEATURE [App::DocumentObjectGroupPython] N_element034  label="N_element : 0.076"  # scripted group (container) (typed FeaturePython)
  n = 0.0764169
FEATURE [App::DocumentObjectGroupPython] O_element074  label="O_element : 0.087"  # scripted group (container) (typed FeaturePython)
  n = 0.0872889
FEATURE [App::DocumentObjectGroupPython] G4_NYLON_11_RILSAN  label="G4_NYLON-11_RILSAN"  # scripted group (container) (typed FeaturePython)
  Dunit = g/cm3
  Dvalue = 1.425
  Group = -> [H_element066,C_element072,N_element034,O_element074]
  conduct = 2
  density = 1
  expand = 3
  formula = G4_NYLON-11_RILSAN
  name = G4_NYLON-11_RILSAN
  specific = 4
FEATURE [App::DocumentObjectGroupPython] C_element073  label="C_element : 8"  # scripted group (container) (typed FeaturePython)
  n = 8
  ref = C_element
FEATURE [App::DocumentObjectGroupPython] H_element067  label="H_element : 18"  # scripted group (container) (typed FeaturePython)
  n = 18
  ref = H_element
FEATURE [App::DocumentObjectGroupPython] G4_OCTANE  # scripted group (container) (typed FeaturePython)
  Dunit = g/cm3
  Dvalue = 0.7026
  Group = -> [C_element073,H_element067]
  conduct = 2
  density = 1
  expand = 3
  formula = G4_OCTANE
  name = G4_OCTANE
  specific = 4
FEATURE [App::DocumentObjectGroupPython] C_element074  label="C_element : 25"  # scripted group (container) (typed FeaturePython)
  n = 25
  ref = C_element
FEATURE [App::DocumentObjectGroupPython] H_element068  label="H_element : 52"  # scripted group (container) (typed FeaturePython)
  n = 52
  ref = H_element
FEATURE [App::DocumentObjectGroupPython] G4_PARAFFIN  # scripted group (container) (typed FeaturePython)
  Dunit = g/cm3
  Dvalue = 0.93
  Group = -> [C_element074,H_element068]
  conduct = 2
  density = 1
  expand = 3
  formula = G4_PARAFFIN
  name = G4_PARAFFIN
  specific = 4
FEATURE [App::DocumentObjectGroupPython] C_element075  label="C_element : 036"  # scripted group (container) (typed FeaturePython)
  n = 5
  ref = C_element
FEATURE [App::DocumentObjectGroupPython] H_element069  label="H_element : 032"  # scripted group (container) (typed FeaturePython)
  n = 12
  ref = H_element
FEATURE [App::DocumentObjectGroupPython] G4_N_PENTANE  label="G4_N-PENTANE"  # scripted group (container) (typed FeaturePython)
  Dunit = g/cm3
  Dvalue = 0.6262
  Group = -> [C_element075,H_element069]
  conduct = 2
  density = 1
  expand = 3
  formula = G4_N-PENTANE
  name = G4_N-PENTANE
  specific = 4
FEATURE [App::DocumentObjectGroupPython] H_element070  label="H_element : 0.014"  # scripted group (container) (typed FeaturePython)
  n = 0.0141
FEATURE [App::DocumentObjectGroupPython] C_element076  label="C_element : 0.072"  # scripted group (container) (typed FeaturePython)
  n = 0.072261
FEATURE [App::DocumentObjectGroupPython] N_element035  label="N_element : 0.019"  # scripted group (container) (typed FeaturePython)
  n = 0.01932
FEATURE [App::DocumentObjectGroupPython] O_element075  label="O_element : 0.066"  # scripted group (container) (typed FeaturePython)
  n = 0.066101
FEATURE [App::DocumentObjectGroupPython] S_element019  label="S_element : 0.020"  # scripted group (container) (typed FeaturePython)
  n = 0.00189
FEATURE [App::DocumentObjectGroupPython] Br_element004  label="Br_element : 0.349"  # scripted group (container) (typed FeaturePython)
  n = 0.349103
FEATURE [App::DocumentObjectGroupPython] Ag_element001  label="Ag_element : 0.474"  # scripted group (container) (typed FeaturePython)
  n = 0.474105
FEATURE [App::DocumentObjectGroupPython] I_element005  label="I_element : 0.003"  # scripted group (container) (typed FeaturePython)
  n = 0.00312
FEATURE [App::DocumentObjectGroupPython] G4_PHOTO_EMULSION  # scripted group (container) (typed FeaturePython)
  Dunit = g/cm3
  Dvalue = 3.815
  Group = -> [H_element070,C_element076,N_element035,O_element075,S_element019,Br_element004,Ag_element001,I_element005]
  conduct = 2
  density = 1
  expand = 3
  formula = G4_PHOTO_EMULSION
  name = G4_PHOTO_EMULSION
  specific = 4
FEATURE [App::DocumentObjectGroupPython] C_element077  label="C_element : 9"  # scripted group (container) (typed FeaturePython)
  n = 9
  ref = C_element
FEATURE [App::DocumentObjectGroupPython] H_element071  label="H_element : 033"  # scripted group (container) (typed FeaturePython)
  n = 10
  ref = H_element
FEATURE [App::DocumentObjectGroupPython] G4_PLASTIC_SC_VINYLTOLUENE  # scripted group (container) (typed FeaturePython)
  Dunit = g/cm3
  Dvalue = 1.032
  Group = -> [C_element077,H_element071]
  conduct = 2
  density = 1
  expand = 3
  formula = G4_PLASTIC_SC_VINYLTOLUENE
  name = G4_PLASTIC_SC_VINYLTOLUENE
  specific = 4
FEATURE [App::DocumentObjectGroupPython] Pu_element001  label="Pu_element : 1"  # scripted group (container) (typed FeaturePython)
  n = 1
  ref = Pu_element
FEATURE [App::DocumentObjectGroupPython] O_element076  label="O_element : 037"  # scripted group (container) (typed FeaturePython)
  n = 2
  ref = O_element
FEATURE [App::DocumentObjectGroupPython] G4_PLUTONIUM_DIOXIDE  # scripted group (container) (typed FeaturePython)
  Dunit = g/cm3
  Dvalue = 11.46
  Group = -> [Pu_element001,O_element076]
  conduct = 2
  density = 1
  expand = 3
  formula = G4_PLUTONIUM_DIOXIDE
  name = G4_PLUTONIUM_DIOXIDE
  specific = 4
FEATURE [App::DocumentObjectGroupPython] C_element078  label="C_element : 037"  # scripted group (container) (typed FeaturePython)
  n = 3
  ref = C_element
FEATURE [App::DocumentObjectGroupPython] H_element072  label="H_element : 034"  # scripted group (container) (typed FeaturePython)
  n = 3
  ref = H_element
FEATURE [App::DocumentObjectGroupPython] N_element036  label="N_element : 015"  # scripted group (container) (typed FeaturePython)
  n = 1
  ref = N_element
FEATURE [App::DocumentObjectGroupPython] G4_POLYACRYLONITRILE  # scripted group (container) (typed FeaturePython)
  Dunit = g/cm3
  Dvalue = 1.17
  Group = -> [C_element078,H_element072,N_element036]
  conduct = 2
  density = 1
  expand = 3
  formula = G4_POLYACRYLONITRILE
  name = G4_POLYACRYLONITRILE
  specific = 4
FEATURE [App::DocumentObjectGroupPython] C_element079  label="C_element : 16"  # scripted group (container) (typed FeaturePython)
  n = 16
  ref = C_element
FEATURE [App::DocumentObjectGroupPython] H_element073  label="H_element : 035"  # scripted group (container) (typed FeaturePython)
  n = 14
  ref = H_element
FEATURE [App::DocumentObjectGroupPython] O_element077  label="O_element : 038"  # scripted group (container) (typed FeaturePython)
  n = 3
  ref = O_element
FEATURE [App::DocumentObjectGroupPython] G4_POLYCARBONATE  # scripted group (container) (typed FeaturePython)
  Dunit = g/cm3
  Dvalue = 1.2
  Group = -> [C_element079,H_element073,O_element077]
  conduct = 2
  density = 1
  expand = 3
  formula = G4_POLYCARBONATE
  name = G4_POLYCARBONATE
  specific = 4
FEATURE [App::DocumentObjectGroupPython] C_element080  label="C_element : 038"  # scripted group (container) (typed FeaturePython)
  n = 8
  ref = C_element
FEATURE [App::DocumentObjectGroupPython] H_element074  label="H_element : 036"  # scripted group (container) (typed FeaturePython)
  n = 7
  ref = H_element
FEATURE [App::DocumentObjectGroupPython] Cl_element017  label="Cl_element : 007"  # scripted group (container) (typed FeaturePython)
  n = 1
  ref = Cl_element
FEATURE [App::DocumentObjectGroupPython] G4_POLYCHLOROSTYRENE  # scripted group (container) (typed FeaturePython)
  Dunit = g/cm3
  Dvalue = 1.3
  Group = -> [C_element080,H_element074,Cl_element017]
  conduct = 2
  density = 1
  expand = 3
  formula = G4_POLYCHLOROSTYRENE
  name = G4_POLYCHLOROSTYRENE
  specific = 4
FEATURE [App::DocumentObjectGroupPython] C_element081  label="C_element : 039"  # scripted group (container) (typed FeaturePython)
  n = 1
  ref = C_element
FEATURE [App::DocumentObjectGroupPython] H_element075  label="H_element : 037"  # scripted group (container) (typed FeaturePython)
  n = 2
  ref = H_element
FEATURE [App::DocumentObjectGroupPython] G4_POLYETHYLENE  # scripted group (container) (typed FeaturePython)
  Dunit = g/cm3
  Dvalue = 0.94
  Group = -> [C_element081,H_element075]
  conduct = 2
  density = 1
  expand = 3
  formula = G4_POLYETHYLENE
  name = G4_POLYETHYLENE
  specific = 4
FEATURE [App::DocumentObjectGroupPython] C_element082  label="C_element : 040"  # scripted group (container) (typed FeaturePython)
  n = 10
  ref = C_element
FEATURE [App::DocumentObjectGroupPython] H_element076  label="H_element : 038"  # scripted group (container) (typed FeaturePython)
  n = 8
  ref = H_element
FEATURE [App::DocumentObjectGroupPython] O_element078  label="O_element : 039"  # scripted group (container) (typed FeaturePython)
  n = 4
  ref = O_element
FEATURE [App::DocumentObjectGroupPython] G4_MYLAR  # scripted group (container) (typed FeaturePython)
  Dunit = g/cm3
  Dvalue = 1.4
  Group = -> [C_element082,H_element076,O_element078]
  conduct = 2
  density = 1
  expand = 3
  formula = G4_MYLAR
  name = G4_MYLAR
  specific = 4
FEATURE [App::DocumentObjectGroupPython] C_element083  label="C_element : 041"  # scripted group (container) (typed FeaturePython)
  n = 5
  ref = C_element
FEATURE [App::DocumentObjectGroupPython] H_element077  label="H_element : 039"  # scripted group (container) (typed FeaturePython)
  n = 8
  ref = H_element
FEATURE [App::DocumentObjectGroupPython] O_element079  label="O_element : 040"  # scripted group (container) (typed FeaturePython)
  n = 2
  ref = O_element
FEATURE [App::DocumentObjectGroupPython] G4_PLEXIGLASS  # scripted group (container) (typed FeaturePython)
  Dunit = g/cm3
  Dvalue = 1.19
  Group = -> [C_element083,H_element077,O_element079]
  conduct = 2
  density = 1
  expand = 3
  formula = G4_PLEXIGLASS
  name = G4_PLEXIGLASS
  specific = 4
FEATURE [App::DocumentObjectGroupPython] C_element084  label="C_element : 042"  # scripted group (container) (typed FeaturePython)
  n = 1
  ref = C_element
FEATURE [App::DocumentObjectGroupPython] H_element078  label="H_element : 040"  # scripted group (container) (typed FeaturePython)
  n = 2
  ref = H_element
FEATURE [App::DocumentObjectGroupPython] O_element080  label="O_element : 041"  # scripted group (container) (typed FeaturePython)
  n = 1
  ref = O_element
FEATURE [App::DocumentObjectGroupPython] G4_POLYOXYMETHYLENE  # scripted group (container) (typed FeaturePython)
  Dunit = g/cm3
  Dvalue = 1.425
  Group = -> [C_element084,H_element078,O_element080]
  conduct = 2
  density = 1
  expand = 3
  formula = G4_POLYOXYMETHYLENE
  name = G4_POLYOXYMETHYLENE
  specific = 4
FEATURE [App::DocumentObjectGroupPython] C_element085  label="C_element : 043"  # scripted group (container) (typed FeaturePython)
  n = 2
  ref = C_element
FEATURE [App::DocumentObjectGroupPython] H_element079  label="H_element : 041"  # scripted group (container) (typed FeaturePython)
  n = 4
  ref = H_element
FEATURE [App::DocumentObjectGroupPython] G4_POLYPROPYLENE  # scripted group (container) (typed FeaturePython)
  Dunit = g/cm3
  Dvalue = 0.9
  Group = -> [C_element085,H_element079]
  conduct = 2
  density = 1
  expand = 3
  formula = G4_POLYPROPYLENE
  name = G4_POLYPROPYLENE
  specific = 4
FEATURE [App::DocumentObjectGroupPython] C_element086  label="C_element : 044"  # scripted group (container) (typed FeaturePython)
  n = 8
  ref = C_element
FEATURE [App::DocumentObjectGroupPython] H_element080  label="H_element : 042"  # scripted group (container) (typed FeaturePython)
  n = 8
  ref = H_element
FEATURE [App::DocumentObjectGroupPython] G4_POLYSTYRENE  # scripted group (container) (typed FeaturePython)
  Dunit = g/cm3
  Dvalue = 1.06
  Group = -> [C_element086,H_element080]
  conduct = 2
  density = 1
  expand = 3
  formula = G4_POLYSTYRENE
  name = G4_POLYSTYRENE
  specific = 4
FEATURE [App::DocumentObjectGroupPython] C_element087  label="C_element : 045"  # scripted group (container) (typed FeaturePython)
  n = 2
  ref = C_element
FEATURE [App::DocumentObjectGroupPython] F_element014  label="F_element : 4"  # scripted group (container) (typed FeaturePython)
  n = 4
  ref = F_element
FEATURE [App::DocumentObjectGroupPython] G4_TEFLON  # scripted group (container) (typed FeaturePython)
  Dunit = g/cm3
  Dvalue = 2.2
  Group = -> [C_element087,F_element014]
  conduct = 2
  density = 1
  expand = 3
  formula = G4_TEFLON
  name = G4_TEFLON
  specific = 4
FEATURE [App::DocumentObjectGroupPython] C_element088  label="C_element : 046"  # scripted group (container) (typed FeaturePython)
  n = 2
  ref = C_element
FEATURE [App::DocumentObjectGroupPython] F_element015  label="F_element : 006"  # scripted group (container) (typed FeaturePython)
  n = 3
  ref = F_element
FEATURE [App::DocumentObjectGroupPython] Cl_element018  label="Cl_element : 008"  # scripted group (container) (typed FeaturePython)
  n = 1
  ref = Cl_element
FEATURE [App::DocumentObjectGroupPython] G4_POLYTRIFLUOROCHLOROETHYLENE  # scripted group (container) (typed FeaturePython)
  Dunit = g/cm3
  Dvalue = 2.1
  Group = -> [C_element088,F_element015,Cl_element018]
  conduct = 2
  density = 1
  expand = 3
  formula = G4_POLYTRIFLUOROCHLOROETHYLENE
  name = G4_POLYTRIFLUOROCHLOROETHYLENE
  specific = 4
FEATURE [App::DocumentObjectGroupPython] C_element089  label="C_element : 047"  # scripted group (container) (typed FeaturePython)
  n = 4
  ref = C_element
FEATURE [App::DocumentObjectGroupPython] H_element081  label="H_element : 043"  # scripted group (container) (typed FeaturePython)
  n = 6
  ref = H_element
FEATURE [App::DocumentObjectGroupPython] O_element081  label="O_element : 042"  # scripted group (container) (typed FeaturePython)
  n = 2
  ref = O_element
FEATURE [App::DocumentObjectGroupPython] G4_POLYVINYL_ACETATE  # scripted group (container) (typed FeaturePython)
  Dunit = g/cm3
  Dvalue = 1.19
  Group = -> [C_element089,H_element081,O_element081]
  conduct = 2
  density = 1
  expand = 3
  formula = G4_POLYVINYL_ACETATE
  name = G4_POLYVINYL_ACETATE
  specific = 4
FEATURE [App::DocumentObjectGroupPython] C_element090  label="C_element : 048"  # scripted group (container) (typed FeaturePython)
  n = 2
  ref = C_element
FEATURE [App::DocumentObjectGroupPython] H_element082  label="H_element : 044"  # scripted group (container) (typed FeaturePython)
  n = 4
  ref = H_element
FEATURE [App::DocumentObjectGroupPython] O_element082  label="O_element : 043"  # scripted group (container) (typed FeaturePython)
  n = 1
  ref = O_element
FEATURE [App::DocumentObjectGroupPython] G4_POLYVINYL_ALCOHOL  # scripted group (container) (typed FeaturePython)
  Dunit = g/cm3
  Dvalue = 1.3
  Group = -> [C_element090,H_element082,O_element082]
  conduct = 2
  density = 1
  expand = 3
  formula = G4_POLYVINYL_ALCOHOL
  name = G4_POLYVINYL_ALCOHOL
  specific = 4
FEATURE [App::DocumentObjectGroupPython] C_element091  label="C_element : 049"  # scripted group (container) (typed FeaturePython)
  n = 8
  ref = C_element
FEATURE [App::DocumentObjectGroupPython] H_element083  label="H_element : 045"  # scripted group (container) (typed FeaturePython)
  n = 14
  ref = H_element
FEATURE [App::DocumentObjectGroupPython] O_element083  label="O_element : 044"  # scripted group (container) (typed FeaturePython)
  n = 2
  ref = O_element
FEATURE [App::DocumentObjectGroupPython] G4_POLYVINYL_BUTYRAL  # scripted group (container) (typed FeaturePython)
  Dunit = g/cm3
  Dvalue = 1.12
  Group = -> [C_element091,H_element083,O_element083]
  conduct = 2
  density = 1
  expand = 3
  formula = G4_POLYVINYL_BUTYRAL
  name = G4_POLYVINYL_BUTYRAL
  specific = 4
FEATURE [App::DocumentObjectGroupPython] C_element092  label="C_element : 050"  # scripted group (container) (typed FeaturePython)
  n = 2
  ref = C_element
FEATURE [App::DocumentObjectGroupPython] H_element084  label="H_element : 046"  # scripted group (container) (typed FeaturePython)
  n = 3
  ref = H_element
FEATURE [App::DocumentObjectGroupPython] Cl_element019  label="Cl_element : 009"  # scripted group (container) (typed FeaturePython)
  n = 1
  ref = Cl_element
FEATURE [App::DocumentObjectGroupPython] G4_POLYVINYL_CHLORIDE  # scripted group (container) (typed FeaturePython)
  Dunit = g/cm3
  Dvalue = 1.3
  Group = -> [C_element092,H_element084,Cl_element019]
  conduct = 2
  density = 1
  expand = 3
  formula = G4_POLYVINYL_CHLORIDE
  name = G4_POLYVINYL_CHLORIDE
  specific = 4
FEATURE [App::DocumentObjectGroupPython] C_element093  label="C_element : 051"  # scripted group (container) (typed FeaturePython)
  n = 2
  ref = C_element
FEATURE [App::DocumentObjectGroupPython] H_element085  label="H_element : 047"  # scripted group (container) (typed FeaturePython)
  n = 2
  ref = H_element
FEATURE [App::DocumentObjectGroupPython] Cl_element020  label="Cl_element : 010"  # scripted group (container) (typed FeaturePython)
  n = 2
  ref = Cl_element
FEATURE [App::DocumentObjectGroupPython] G4_POLYVINYLIDENE_CHLORIDE  # scripted group (container) (typed FeaturePython)
  Dunit = g/cm3
  Dvalue = 1.7
  Group = -> [C_element093,H_element085,Cl_element020]
  conduct = 2
  density = 1
  expand = 3
  formula = G4_POLYVINYLIDENE_CHLORIDE
  name = G4_POLYVINYLIDENE_CHLORIDE
  specific = 4
FEATURE [App::DocumentObjectGroupPython] C_element094  label="C_element : 052"  # scripted group (container) (typed FeaturePython)
  n = 2
  ref = C_element
FEATURE [App::DocumentObjectGroupPython] H_element086  label="H_element : 048"  # scripted group (container) (typed FeaturePython)
  n = 2
  ref = H_element
FEATURE [App::DocumentObjectGroupPython] F_element016  label="F_element : 007"  # scripted group (container) (typed FeaturePython)
  n = 2
  ref = F_element
FEATURE [App::DocumentObjectGroupPython] G4_POLYVINYLIDENE_FLUORIDE  # scripted group (container) (typed FeaturePython)
  Dunit = g/cm3
  Dvalue = 1.76
  Group = -> [C_element094,H_element086,F_element016]
  conduct = 2
  density = 1
  expand = 3
  formula = G4_POLYVINYLIDENE_FLUORIDE
  name = G4_POLYVINYLIDENE_FLUORIDE
  specific = 4
FEATURE [App::DocumentObjectGroupPython] C_element095  label="C_element : 053"  # scripted group (container) (typed FeaturePython)
  n = 6
  ref = C_element
FEATURE [App::DocumentObjectGroupPython] H_element087  label="H_element : 9"  # scripted group (container) (typed FeaturePython)
  n = 9
  ref = H_element
FEATURE [App::DocumentObjectGroupPython] N_element037  label="N_element : 016"  # scripted group (container) (typed FeaturePython)
  n = 1
  ref = N_element
FEATURE [App::DocumentObjectGroupPython] O_element084  label="O_element : 045"  # scripted group (container) (typed FeaturePython)
  n = 1
  ref = O_element
FEATURE [App::DocumentObjectGroupPython] G4_POLYVINYL_PYRROLIDONE  # scripted group (container) (typed FeaturePython)
  Dunit = g/cm3
  Dvalue = 1.25
  Group = -> [C_element095,H_element087,N_element037,O_element084]
  conduct = 2
  density = 1
  expand = 3
  formula = G4_POLYVINYL_PYRROLIDONE
  name = G4_POLYVINYL_PYRROLIDONE
  specific = 4
FEATURE [App::DocumentObjectGroupPython] K_element008  label="K_element : 1"  # scripted group (container) (typed FeaturePython)
  n = 1
  ref = K_element
FEATURE [App::DocumentObjectGroupPython] I_element006  label="I_element : 003"  # scripted group (container) (typed FeaturePython)
  n = 1
  ref = I_element
FEATURE [App::DocumentObjectGroupPython] G4_POTASSIUM_IODIDE  # scripted group (container) (typed FeaturePython)
  Dunit = g/cm3
  Dvalue = 3.13
  Group = -> [K_element008,I_element006]
  conduct = 2
  density = 1
  expand = 3
  formula = G4_POTASSIUM_IODIDE
  name = G4_POTASSIUM_IODIDE
  specific = 4
FEATURE [App::DocumentObjectGroupPython] K_element009  label="K_element : 2"  # scripted group (container) (typed FeaturePython)
  n = 2
  ref = K_element
FEATURE [App::DocumentObjectGroupPython] O_element085  label="O_element : 046"  # scripted group (container) (typed FeaturePython)
  n = 1
  ref = O_element
FEATURE [App::DocumentObjectGroupPython] G4_POTASSIUM_OXIDE  # scripted group (container) (typed FeaturePython)
  Dunit = g/cm3
  Dvalue = 2.32
  Group = -> [K_element009,O_element085]
  conduct = 2
  density = 1
  expand = 3
  formula = G4_POTASSIUM_OXIDE
  name = G4_POTASSIUM_OXIDE
  specific = 4
FEATURE [App::DocumentObjectGroupPython] C_element096  label="C_element : 054"  # scripted group (container) (typed FeaturePython)
  n = 3
  ref = C_element
FEATURE [App::DocumentObjectGroupPython] H_element088  label="H_element : 049"  # scripted group (container) (typed FeaturePython)
  n = 8
  ref = H_element
FEATURE [App::DocumentObjectGroupPython] G4_PROPANE  # scripted group (container) (typed FeaturePython)
  Dunit = g/cm3
  Dvalue = 0.00187939
  Group = -> [C_element096,H_element088]
  conduct = 2
  density = 1
  expand = 3
  formula = G4_PROPANE
  name = G4_PROPANE
  specific = 4
FEATURE [App::DocumentObjectGroupPython] C_element097  label="C_element : 055"  # scripted group (container) (typed FeaturePython)
  n = 3
  ref = C_element
FEATURE [App::DocumentObjectGroupPython] H_element089  label="H_element : 050"  # scripted group (container) (typed FeaturePython)
  n = 8
  ref = H_element
FEATURE [App::DocumentObjectGroupPython] G4_lPROPANE  # scripted group (container) (typed FeaturePython)
  Dunit = g/cm3
  Dvalue = 0.43
  Group = -> [C_element097,H_element089]
  conduct = 2
  density = 1
  expand = 3
  formula = G4_lPROPANE
  name = G4_lPROPANE
  specific = 4
FEATURE [App::DocumentObjectGroupPython] C_element098  label="C_element : 056"  # scripted group (container) (typed FeaturePython)
  n = 3
  ref = C_element
FEATURE [App::DocumentObjectGroupPython] H_element090  label="H_element : 051"  # scripted group (container) (typed FeaturePython)
  n = 8
  ref = H_element
FEATURE [App::DocumentObjectGroupPython] O_element086  label="O_element : 047"  # scripted group (container) (typed FeaturePython)
  n = 1
  ref = O_element
FEATURE [App::DocumentObjectGroupPython] G4_N_PROPYL_ALCOHOL  label="G4_N-PROPYL_ALCOHOL"  # scripted group (container) (typed FeaturePython)
  Dunit = g/cm3
  Dvalue = 0.8035
  Group = -> [C_element098,H_element090,O_element086]
  conduct = 2
  density = 1
  expand = 3
  formula = G4_N-PROPYL_ALCOHOL
  name = G4_N-PROPYL_ALCOHOL
  specific = 4
FEATURE [App::DocumentObjectGroupPython] C_element099  label="C_element : 057"  # scripted group (container) (typed FeaturePython)
  n = 5
  ref = C_element
FEATURE [App::DocumentObjectGroupPython] H_element091  label="H_element : 052"  # scripted group (container) (typed FeaturePython)
  n = 5
  ref = H_element
FEATURE [App::DocumentObjectGroupPython] N_element038  label="N_element : 017"  # scripted group (container) (typed FeaturePython)
  n = 1
  ref = N_element
FEATURE [App::DocumentObjectGroupPython] G4_PYRIDINE  # scripted group (container) (typed FeaturePython)
  Dunit = g/cm3
  Dvalue = 0.9819
  Group = -> [C_element099,H_element091,N_element038]
  conduct = 2
  density = 1
  expand = 3
  formula = G4_PYRIDINE
  name = G4_PYRIDINE
  specific = 4
FEATURE [App::DocumentObjectGroupPython] H_element092  label="H_element : 0.144"  # scripted group (container) (typed FeaturePython)
  n = 0.143711
FEATURE [App::DocumentObjectGroupPython] C_element100  label="C_element : 0.856"  # scripted group (container) (typed FeaturePython)
  n = 0.856289
FEATURE [App::DocumentObjectGroupPython] G4_RUBBER_BUTYL  # scripted group (container) (typed FeaturePython)
  Dunit = g/cm3
  Dvalue = 0.92
  Group = -> [H_element092,C_element100]
  conduct = 2
  density = 1
  expand = 3
  formula = G4_RUBBER_BUTYL
  name = G4_RUBBER_BUTYL
  specific = 4
FEATURE [App::DocumentObjectGroupPython] H_element093  label="H_element : 0.118"  # scripted group (container) (typed FeaturePython)
  n = 0.118371
FEATURE [App::DocumentObjectGroupPython] C_element101  label="C_element : 0.882"  # scripted group (container) (typed FeaturePython)
  n = 0.881629
FEATURE [App::DocumentObjectGroupPython] G4_RUBBER_NATURAL  # scripted group (container) (typed FeaturePython)
  Dunit = g/cm3
  Dvalue = 0.92
  Group = -> [H_element093,C_element101]
  conduct = 2
  density = 1
  expand = 3
  formula = G4_RUBBER_NATURAL
  name = G4_RUBBER_NATURAL
  specific = 4
FEATURE [App::DocumentObjectGroupPython] H_element094  label="H_element : 0.145"  # scripted group (container) (typed FeaturePython)
  n = 0.05692
FEATURE [App::DocumentObjectGroupPython] C_element102  label="C_element : 0.543"  # scripted group (container) (typed FeaturePython)
  n = 0.542646
FEATURE [App::DocumentObjectGroupPython] Cl_element021  label="Cl_element : 0.400"  # scripted group (container) (typed FeaturePython)
  n = 0.400434
FEATURE [App::DocumentObjectGroupPython] G4_RUBBER_NEOPRENE  # scripted group (container) (typed FeaturePython)
  Dunit = g/cm3
  Dvalue = 1.23
  Group = -> [H_element094,C_element102,Cl_element021]
  conduct = 2
  density = 1
  expand = 3
  formula = G4_RUBBER_NEOPRENE
  name = G4_RUBBER_NEOPRENE
  specific = 4
FEATURE [App::DocumentObjectGroupPython] Si_element006  label="Si_element : 1"  # scripted group (container) (typed FeaturePython)
  n = 1
  ref = Si_element
FEATURE [App::DocumentObjectGroupPython] O_element087  label="O_element : 048"  # scripted group (container) (typed FeaturePython)
  n = 2
  ref = O_element
FEATURE [App::DocumentObjectGroupPython] G4_SILICON_DIOXIDE  # scripted group (container) (typed FeaturePython)
  Dunit = g/cm3
  Dvalue = 2.32
  Group = -> [Si_element006,O_element087]
  conduct = 2
  density = 1
  expand = 3
  formula = G4_SILICON_DIOXIDE
  name = G4_SILICON_DIOXIDE
  specific = 4
FEATURE [App::DocumentObjectGroupPython] Ag_element002  label="Ag_element : 1"  # scripted group (container) (typed FeaturePython)
  n = 1
  ref = Ag_element
FEATURE [App::DocumentObjectGroupPython] Br_element005  label="Br_element : 003"  # scripted group (container) (typed FeaturePython)
  n = 1
  ref = Br_element
FEATURE [App::DocumentObjectGroupPython] G4_SILVER_BROMIDE  # scripted group (container) (typed FeaturePython)
  Dunit = g/cm3
  Dvalue = 6.473
  Group = -> [Ag_element002,Br_element005]
  conduct = 2
  density = 1
  expand = 3
  formula = G4_SILVER_BROMIDE
  name = G4_SILVER_BROMIDE
  specific = 4
FEATURE [App::DocumentObjectGroupPython] Ag_element003  label="Ag_element : 002"  # scripted group (container) (typed FeaturePython)
  n = 1
  ref = Ag_element
FEATURE [App::DocumentObjectGroupPython] Cl_element022  label="Cl_element : 011"  # scripted group (container) (typed FeaturePython)
  n = 1
  ref = Cl_element
FEATURE [App::DocumentObjectGroupPython] G4_SILVER_CHLORIDE  # scripted group (container) (typed FeaturePython)
  Dunit = g/cm3
  Dvalue = 5.56
  Group = -> [Ag_element003,Cl_element022]
  conduct = 2
  density = 1
  expand = 3
  formula = G4_SILVER_CHLORIDE
  name = G4_SILVER_CHLORIDE
  specific = 4
FEATURE [App::DocumentObjectGroupPython] Br_element006  label="Br_element : 0.423"  # scripted group (container) (typed FeaturePython)
  n = 0.422895
FEATURE [App::DocumentObjectGroupPython] Ag_element004  label="Ag_element : 0.574"  # scripted group (container) (typed FeaturePython)
  n = 0.573748
FEATURE [App::DocumentObjectGroupPython] I_element007  label="I_element : 0.649"  # scripted group (container) (typed FeaturePython)
  n = 0.003357
FEATURE [App::DocumentObjectGroupPython] G4_SILVER_HALIDES  # scripted group (container) (typed FeaturePython)
  Dunit = g/cm3
  Dvalue = 6.47
  Group = -> [Br_element006,Ag_element004,I_element007]
  conduct = 2
  density = 1
  expand = 3
  formula = G4_SILVER_HALIDES
  name = G4_SILVER_HALIDES
  specific = 4
FEATURE [App::DocumentObjectGroupPython] Ag_element005  label="Ag_element : 003"  # scripted group (container) (typed FeaturePython)
  n = 1
  ref = Ag_element
FEATURE [App::DocumentObjectGroupPython] I_element008  label="I_element : 004"  # scripted group (container) (typed FeaturePython)
  n = 1
  ref = I_element
FEATURE [App::DocumentObjectGroupPython] G4_SILVER_IODIDE  # scripted group (container) (typed FeaturePython)
  Dunit = g/cm3
  Dvalue = 6.01
  Group = -> [Ag_element005,I_element008]
  conduct = 2
  density = 1
  expand = 3
  formula = G4_SILVER_IODIDE
  name = G4_SILVER_IODIDE
  specific = 4
FEATURE [App::DocumentObjectGroupPython] H_element095  label="H_element : 0.100"  # scripted group (container) (typed FeaturePython)
  n = 0.1
FEATURE [App::DocumentObjectGroupPython] C_element103  label="C_element : 0.204"  # scripted group (container) (typed FeaturePython)
  n = 0.204
FEATURE [App::DocumentObjectGroupPython] N_element039  label="N_element : 0.759"  # scripted group (container) (typed FeaturePython)
  n = 0.042
FEATURE [App::DocumentObjectGroupPython] O_element088  label="O_element : 0.645"  # scripted group (container) (typed FeaturePython)
  n = 0.645
FEATURE [App::DocumentObjectGroupPython] Na_element013  label="Na_element : 0.100"  # scripted group (container) (typed FeaturePython)
  n = 0.002
FEATURE [App::DocumentObjectGroupPython] P_element009  label="P_element : 0.107"  # scripted group (container) (typed FeaturePython)
  n = 0.001
FEATURE [App::DocumentObjectGroupPython] S_element020  label="S_element : 0.021"  # scripted group (container) (typed FeaturePython)
  n = 0.002
FEATURE [App::DocumentObjectGroupPython] Cl_element023  label="Cl_element : 0.590"  # scripted group (container) (typed FeaturePython)
  n = 0.003
FEATURE [App::DocumentObjectGroupPython] K_element010  label="K_element : 0.001"  # scripted group (container) (typed FeaturePython)
  n = 0.001
FEATURE [App::DocumentObjectGroupPython] G4_SKIN_ICRP  # scripted group (container) (typed FeaturePython)
  Dunit = g/cm3
  Dvalue = 1.09
  Group = -> [H_element095,C_element103,N_element039,O_element088,Na_element013,P_element009,S_element020,Cl_element023,K_element010]
  conduct = 2
  density = 1
  expand = 3
  formula = G4_SKIN_ICRP
  name = G4_SKIN_ICRP
  specific = 4
FEATURE [App::DocumentObjectGroupPython] Na_element014  label="Na_element : 2"  # scripted group (container) (typed FeaturePython)
  n = 2
  ref = Na_element
FEATURE [App::DocumentObjectGroupPython] C_element104  label="C_element : 058"  # scripted group (container) (typed FeaturePython)
  n = 1
  ref = C_element
FEATURE [App::DocumentObjectGroupPython] O_element089  label="O_element : 049"  # scripted group (container) (typed FeaturePython)
  n = 3
  ref = O_element
FEATURE [App::DocumentObjectGroupPython] G4_SODIUM_CARBONATE  # scripted group (container) (typed FeaturePython)
  Dunit = g/cm3
  Dvalue = 2.532
  Group = -> [Na_element014,C_element104,O_element089]
  conduct = 2
  density = 1
  expand = 3
  formula = G4_SODIUM_CARBONATE
  name = G4_SODIUM_CARBONATE
  specific = 4
FEATURE [App::DocumentObjectGroupPython] Na_element015  label="Na_element : 1"  # scripted group (container) (typed FeaturePython)
  n = 1
  ref = Na_element
FEATURE [App::DocumentObjectGroupPython] I_element009  label="I_element : 005"  # scripted group (container) (typed FeaturePython)
  n = 1
  ref = I_element
FEATURE [App::DocumentObjectGroupPython] G4_SODIUM_IODIDE  # scripted group (container) (typed FeaturePython)
  Dunit = g/cm3
  Dvalue = 3.667
  Group = -> [Na_element015,I_element009]
  conduct = 2
  density = 1
  expand = 3
  formula = G4_SODIUM_IODIDE
  name = G4_SODIUM_IODIDE
  specific = 4
FEATURE [App::DocumentObjectGroupPython] Na_element016  label="Na_element : 003"  # scripted group (container) (typed FeaturePython)
  n = 2
  ref = Na_element
FEATURE [App::DocumentObjectGroupPython] O_element090  label="O_element : 050"  # scripted group (container) (typed FeaturePython)
  n = 1
  ref = O_element
FEATURE [App::DocumentObjectGroupPython] G4_SODIUM_MONOXIDE  # scripted group (container) (typed FeaturePython)
  Dunit = g/cm3
  Dvalue = 2.27
  Group = -> [Na_element016,O_element090]
  conduct = 2
  density = 1
  expand = 3
  formula = G4_SODIUM_MONOXIDE
  name = G4_SODIUM_MONOXIDE
  specific = 4
FEATURE [App::DocumentObjectGroupPython] Na_element017  label="Na_element : 004"  # scripted group (container) (typed FeaturePython)
  n = 1
  ref = Na_element
FEATURE [App::DocumentObjectGroupPython] N_element040  label="N_element : 018"  # scripted group (container) (typed FeaturePython)
  n = 1
  ref = N_element
FEATURE [App::DocumentObjectGroupPython] O_element091  label="O_element : 051"  # scripted group (container) (typed FeaturePython)
  n = 3
  ref = O_element
FEATURE [App::DocumentObjectGroupPython] G4_SODIUM_NITRATE  # scripted group (container) (typed FeaturePython)
  Dunit = g/cm3
  Dvalue = 2.261
  Group = -> [Na_element017,N_element040,O_element091]
  conduct = 2
  density = 1
  expand = 3
  formula = G4_SODIUM_NITRATE
  name = G4_SODIUM_NITRATE
  specific = 4
FEATURE [App::DocumentObjectGroupPython] C_element105  label="C_element : 059"  # scripted group (container) (typed FeaturePython)
  n = 14
  ref = C_element
FEATURE [App::DocumentObjectGroupPython] H_element096  label="H_element : 053"  # scripted group (container) (typed FeaturePython)
  n = 12
  ref = H_element
FEATURE [App::DocumentObjectGroupPython] G4_STILBENE  # scripted group (container) (typed FeaturePython)
  Dunit = g/cm3
  Dvalue = 0.9707
  Group = -> [C_element105,H_element096]
  conduct = 2
  density = 1
  expand = 3
  formula = G4_STILBENE
  name = G4_STILBENE
  specific = 4
FEATURE [App::DocumentObjectGroupPython] C_element106  label="C_element : 12"  # scripted group (container) (typed FeaturePython)
  n = 12
  ref = C_element
FEATURE [App::DocumentObjectGroupPython] H_element097  label="H_element : 22"  # scripted group (container) (typed FeaturePython)
  n = 22
  ref = H_element
FEATURE [App::DocumentObjectGroupPython] O_element092  label="O_element : 11"  # scripted group (container) (typed FeaturePython)
  n = 11
  ref = O_element
FEATURE [App::DocumentObjectGroupPython] G4_SUCROSE  # scripted group (container) (typed FeaturePython)
  Dunit = g/cm3
  Dvalue = 1.5805
  Group = -> [C_element106,H_element097,O_element092]
  conduct = 2
  density = 1
  expand = 3
  formula = G4_SUCROSE
  name = G4_SUCROSE
  specific = 4
FEATURE [App::DocumentObjectGroupPython] C_element107  label="C_element : 18"  # scripted group (container) (typed FeaturePython)
  n = 18
  ref = C_element
FEATURE [App::DocumentObjectGroupPython] H_element098  label="H_element : 054"  # scripted group (container) (typed FeaturePython)
  n = 14
  ref = H_element
FEATURE [App::DocumentObjectGroupPython] G4_TERPHENYL  # scripted group (container) (typed FeaturePython)
  Dunit = g/cm3
  Dvalue = 1.24
  Group = -> [C_element107,H_element098]
  conduct = 2
  density = 1
  expand = 3
  formula = G4_TERPHENYL
  name = G4_TERPHENYL
  specific = 4
FEATURE [App::DocumentObjectGroupPython] H_element099  label="H_element : 0.146"  # scripted group (container) (typed FeaturePython)
  n = 0.106
FEATURE [App::DocumentObjectGroupPython] C_element108  label="C_element : 0.883"  # scripted group (container) (typed FeaturePython)
  n = 0.099
FEATURE [App::DocumentObjectGroupPython] N_element041  label="N_element : 0.020"  # scripted group (container) (typed FeaturePython)
  n = 0.02
FEATURE [App::DocumentObjectGroupPython] O_element093  label="O_element : 0.766"  # scripted group (container) (typed FeaturePython)
  n = 0.766
FEATURE [App::DocumentObjectGroupPython] Na_element018  label="Na_element : 0.101"  # scripted group (container) (typed FeaturePython)
  n = 0.002
FEATURE [App::DocumentObjectGroupPython] P_element010  label="P_element : 0.108"  # scripted group (container) (typed FeaturePython)
  n = 0.001
FEATURE [App::DocumentObjectGroupPython] S_element021  label="S_element : 0.022"  # scripted group (container) (typed FeaturePython)
  n = 0.002
FEATURE [App::DocumentObjectGroupPython] Cl_element024  label="Cl_element : 0.002"  # scripted group (container) (typed FeaturePython)
  n = 0.002
FEATURE [App::DocumentObjectGroupPython] K_element011  label="K_element : 0.017"  # scripted group (container) (typed FeaturePython)
  n = 0.002
FEATURE [App::DocumentObjectGroupPython] G4_TESTIS_ICRP  # scripted group (container) (typed FeaturePython)
  Dunit = g/cm3
  Dvalue = 1.04
  Group = -> [H_element099,C_element108,N_element041,O_element093,Na_element018,P_element010,S_element021,Cl_element024,K_element011]
  conduct = 2
  density = 1
  expand = 3
  formula = G4_TESTIS_ICRP
  name = G4_TESTIS_ICRP
  specific = 4
FEATURE [App::DocumentObjectGroupPython] C_element109  label="C_element : 060"  # scripted group (container) (typed FeaturePython)
  n = 2
  ref = C_element
FEATURE [App::DocumentObjectGroupPython] Cl_element025  label="Cl_element : 012"  # scripted group (container) (typed FeaturePython)
  n = 4
  ref = Cl_element
FEATURE [App::DocumentObjectGroupPython] G4_TETRACHLOROETHYLENE  # scripted group (container) (typed FeaturePython)
  Dunit = g/cm3
  Dvalue = 1.625
  Group = -> [C_element109,Cl_element025]
  conduct = 2
  density = 1
  expand = 3
  formula = G4_TETRACHLOROETHYLENE
  name = G4_TETRACHLOROETHYLENE
  specific = 4
FEATURE [App::DocumentObjectGroupPython] Tl_element001  label="Tl_element : 1"  # scripted group (container) (typed FeaturePython)
  n = 1
  ref = Tl_element
FEATURE [App::DocumentObjectGroupPython] Cl_element026  label="Cl_element : 013"  # scripted group (container) (typed FeaturePython)
  n = 1
  ref = Cl_element
FEATURE [App::DocumentObjectGroupPython] G4_THALLIUM_CHLORIDE  # scripted group (container) (typed FeaturePython)
  Dunit = g/cm3
  Dvalue = 7.004
  Group = -> [Tl_element001,Cl_element026]
  conduct = 2
  density = 1
  expand = 3
  formula = G4_THALLIUM_CHLORIDE
  name = G4_THALLIUM_CHLORIDE
  specific = 4
FEATURE [App::DocumentObjectGroupPython] H_element100  label="H_element : 0.147"  # scripted group (container) (typed FeaturePython)
  n = 0.105
FEATURE [App::DocumentObjectGroupPython] C_element110  label="C_element : 0.256"  # scripted group (container) (typed FeaturePython)
  n = 0.256
FEATURE [App::DocumentObjectGroupPython] N_element042  label="N_element : 0.760"  # scripted group (container) (typed FeaturePython)
  n = 0.027
FEATURE [App::DocumentObjectGroupPython] O_element094  label="O_element : 0.602"  # scripted group (container) (typed FeaturePython)
  n = 0.602
FEATURE [App::DocumentObjectGroupPython] Na_element019  label="Na_element : 0.102"  # scripted group (container) (typed FeaturePython)
  n = 0.001
FEATURE [App::DocumentObjectGroupPython] P_element011  label="P_element : 0.109"  # scripted group (container) (typed FeaturePython)
  n = 0.002
FEATURE [App::DocumentObjectGroupPython] S_element022  label="S_element : 0.023"  # scripted group (container) (typed FeaturePython)
  n = 0.003
FEATURE [App::DocumentObjectGroupPython] Cl_element027  label="Cl_element : 0.591"  # scripted group (container) (typed FeaturePython)
  n = 0.002
FEATURE [App::DocumentObjectGroupPython] K_element012  label="K_element : 0.018"  # scripted group (container) (typed FeaturePython)
  n = 0.002
FEATURE [App::DocumentObjectGroupPython] G4_TISSUE_SOFT_ICRP  # scripted group (container) (typed FeaturePython)
  Dunit = g/cm3
  Dvalue = 1.03
  Group = -> [H_element100,C_element110,N_element042,O_element094,Na_element019,P_element011,S_element022,Cl_element027,K_element012]
  conduct = 2
  density = 1
  expand = 3
  formula = G4_TISSUE_SOFT_ICRP
  name = G4_TISSUE_SOFT_ICRP
  specific = 4
FEATURE [App::DocumentObjectGroupPython] H_element101  label="H_element : 0.148"  # scripted group (container) (typed FeaturePython)
  n = 0.101
FEATURE [App::DocumentObjectGroupPython] C_element111  label="C_element : 0.111"  # scripted group (container) (typed FeaturePython)
  n = 0.111
FEATURE [App::DocumentObjectGroupPython] N_element043  label="N_element : 0.026"  # scripted group (container) (typed FeaturePython)
  n = 0.026
FEATURE [App::DocumentObjectGroupPython] O_element095  label="O_element : 0.762"  # scripted group (container) (typed FeaturePython)
  n = 0.762
FEATURE [App::DocumentObjectGroupPython] G4_TISSUE_SOFT_ICRU_4  label="G4_TISSUE_SOFT_ICRU-4"  # scripted group (container) (typed FeaturePython)
  Dunit = g/cm3
  Dvalue = 1
  Group = -> [H_element101,C_element111,N_element043,O_element095]
  conduct = 2
  density = 1
  expand = 3
  formula = G4_TISSUE_SOFT_ICRU-4
  name = G4_TISSUE_SOFT_ICRU-4
  specific = 4
FEATURE [App::DocumentObjectGroupPython] H_element102  label="H_element : 0.149"  # scripted group (container) (typed FeaturePython)
  n = 0.101869
FEATURE [App::DocumentObjectGroupPython] C_element112  label="C_element : 0.456"  # scripted group (container) (typed FeaturePython)
  n = 0.456179
FEATURE [App::DocumentObjectGroupPython] N_element044  label="N_element : 0.761"  # scripted group (container) (typed FeaturePython)
  n = 0.035172
FEATURE [App::DocumentObjectGroupPython] O_element096  label="O_element : 0.407"  # scripted group (container) (typed FeaturePython)
  n = 0.40678
FEATURE [App::DocumentObjectGroupPython] G4_TISSUE_METHANE  label="G4_TISSUE-METHANE"  # scripted group (container) (typed FeaturePython)
  Dunit = g/cm3
  Dvalue = 0.00106409
  Group = -> [H_element102,C_element112,N_element044,O_element096]
  conduct = 2
  density = 1
  expand = 3
  formula = G4_TISSUE-METHANE
  name = G4_TISSUE-METHANE
  specific = 4
FEATURE [App::DocumentObjectGroupPython] H_element103  label="H_element : 0.103"  # scripted group (container) (typed FeaturePython)
  n = 0.102672
FEATURE [App::DocumentObjectGroupPython] C_element113  label="C_element : 0.569"  # scripted group (container) (typed FeaturePython)
  n = 0.56894
FEATURE [App::DocumentObjectGroupPython] N_element045  label="N_element : 0.762"  # scripted group (container) (typed FeaturePython)
  n = 0.035022
FEATURE [App::DocumentObjectGroupPython] O_element097  label="O_element : 0.293"  # scripted group (container) (typed FeaturePython)
  n = 0.293366
FEATURE [App::DocumentObjectGroupPython] G4_TISSUE_PROPANE  label="G4_TISSUE-PROPANE"  # scripted group (container) (typed FeaturePython)
  Dunit = g/cm3
  Dvalue = 0.00182628
  Group = -> [H_element103,C_element113,N_element045,O_element097]
  conduct = 2
  density = 1
  expand = 3
  formula = G4_TISSUE-PROPANE
  name = G4_TISSUE-PROPANE
  specific = 4
FEATURE [App::DocumentObjectGroupPython] Ti_element003  label="Ti_element : 1"  # scripted group (container) (typed FeaturePython)
  n = 1
  ref = Ti_element
FEATURE [App::DocumentObjectGroupPython] O_element098  label="O_element : 052"  # scripted group (container) (typed FeaturePython)
  n = 2
  ref = O_element
FEATURE [App::DocumentObjectGroupPython] G4_TITANIUM_DIOXIDE  # scripted group (container) (typed FeaturePython)
  Dunit = g/cm3
  Dvalue = 4.26
  Group = -> [Ti_element003,O_element098]
  conduct = 2
  density = 1
  expand = 3
  formula = G4_TITANIUM_DIOXIDE
  name = G4_TITANIUM_DIOXIDE
  specific = 4
FEATURE [App::DocumentObjectGroupPython] C_element114  label="C_element : 061"  # scripted group (container) (typed FeaturePython)
  n = 7
  ref = C_element
FEATURE [App::DocumentObjectGroupPython] H_element104  label="H_element : 055"  # scripted group (container) (typed FeaturePython)
  n = 8
  ref = H_element
FEATURE [App::DocumentObjectGroupPython] G4_TOLUENE  # scripted group (container) (typed FeaturePython)
  Dunit = g/cm3
  Dvalue = 0.8669
  Group = -> [C_element114,H_element104]
  conduct = 2
  density = 1
  expand = 3
  formula = G4_TOLUENE
  name = G4_TOLUENE
  specific = 4
FEATURE [App::DocumentObjectGroupPython] C_element115  label="C_element : 062"  # scripted group (container) (typed FeaturePython)
  n = 2
  ref = C_element
FEATURE [App::DocumentObjectGroupPython] H_element105  label="H_element : 056"  # scripted group (container) (typed FeaturePython)
  n = 1
  ref = H_element
FEATURE [App::DocumentObjectGroupPython] Cl_element028  label="Cl_element : 014"  # scripted group (container) (typed FeaturePython)
  n = 3
  ref = Cl_element
FEATURE [App::DocumentObjectGroupPython] G4_TRICHLOROETHYLENE  # scripted group (container) (typed FeaturePython)
  Dunit = g/cm3
  Dvalue = 1.46
  Group = -> [C_element115,H_element105,Cl_element028]
  conduct = 2
  density = 1
  expand = 3
  formula = G4_TRICHLOROETHYLENE
  name = G4_TRICHLOROETHYLENE
  specific = 4
FEATURE [App::DocumentObjectGroupPython] C_element116  label="C_element : 063"  # scripted group (container) (typed FeaturePython)
  n = 6
  ref = C_element
FEATURE [App::DocumentObjectGroupPython] H_element106  label="H_element : 15"  # scripted group (container) (typed FeaturePython)
  n = 15
  ref = H_element
FEATURE [App::DocumentObjectGroupPython] O_element099  label="O_element : 053"  # scripted group (container) (typed FeaturePython)
  n = 4
  ref = O_element
FEATURE [App::DocumentObjectGroupPython] P_element012  label="P_element : 1"  # scripted group (container) (typed FeaturePython)
  n = 1
  ref = P_element
FEATURE [App::DocumentObjectGroupPython] G4_TRIETHYL_PHOSPHATE  # scripted group (container) (typed FeaturePython)
  Dunit = g/cm3
  Dvalue = 1.07
  Group = -> [C_element116,H_element106,O_element099,P_element012]
  conduct = 2
  density = 1
  expand = 3
  formula = G4_TRIETHYL_PHOSPHATE
  name = G4_TRIETHYL_PHOSPHATE
  specific = 4
FEATURE [App::DocumentObjectGroupPython] W_element003  label="W_element : 003"  # scripted group (container) (typed FeaturePython)
  n = 1
  ref = W_element
FEATURE [App::DocumentObjectGroupPython] F_element017  label="F_element : 6"  # scripted group (container) (typed FeaturePython)
  n = 6
  ref = F_element
FEATURE [App::DocumentObjectGroupPython] G4_TUNGSTEN_HEXAFLUORIDE  # scripted group (container) (typed FeaturePython)
  Dunit = g/cm3
  Dvalue = 2.4
  Group = -> [W_element003,F_element017]
  conduct = 2
  density = 1
  expand = 3
  formula = G4_TUNGSTEN_HEXAFLUORIDE
  name = G4_TUNGSTEN_HEXAFLUORIDE
  specific = 4
FEATURE [App::DocumentObjectGroupPython] U_element001  label="U_element : 1"  # scripted group (container) (typed FeaturePython)
  n = 1
  ref = U_element
FEATURE [App::DocumentObjectGroupPython] C_element117  label="C_element : 064"  # scripted group (container) (typed FeaturePython)
  n = 2
  ref = C_element
FEATURE [App::DocumentObjectGroupPython] G4_URANIUM_DICARBIDE  # scripted group (container) (typed FeaturePython)
  Dunit = g/cm3
  Dvalue = 11.28
  Group = -> [U_element001,C_element117]
  conduct = 2
  density = 1
  expand = 3
  formula = G4_URANIUM_DICARBIDE
  name = G4_URANIUM_DICARBIDE
  specific = 4
FEATURE [App::DocumentObjectGroupPython] U_element002  label="U_element : 002"  # scripted group (container) (typed FeaturePython)
  n = 1
  ref = U_element
FEATURE [App::DocumentObjectGroupPython] C_element118  label="C_element : 065"  # scripted group (container) (typed FeaturePython)
  n = 1
  ref = C_element
FEATURE [App::DocumentObjectGroupPython] G4_URANIUM_MONOCARBIDE  # scripted group (container) (typed FeaturePython)
  Dunit = g/cm3
  Dvalue = 13.63
  Group = -> [U_element002,C_element118]
  conduct = 2
  density = 1
  expand = 3
  formula = G4_URANIUM_MONOCARBIDE
  name = G4_URANIUM_MONOCARBIDE
  specific = 4
FEATURE [App::DocumentObjectGroupPython] U_element003  label="U_element : 003"  # scripted group (container) (typed FeaturePython)
  n = 1
  ref = U_element
FEATURE [App::DocumentObjectGroupPython] O_element100  label="O_element : 054"  # scripted group (container) (typed FeaturePython)
  n = 2
  ref = O_element
FEATURE [App::DocumentObjectGroupPython] G4_URANIUM_OXIDE  # scripted group (container) (typed FeaturePython)
  Dunit = g/cm3
  Dvalue = 10.96
  Group = -> [U_element003,O_element100]
  conduct = 2
  density = 1
  expand = 3
  formula = G4_URANIUM_OXIDE
  name = G4_URANIUM_OXIDE
  specific = 4
FEATURE [App::DocumentObjectGroupPython] C_element119  label="C_element : 066"  # scripted group (container) (typed FeaturePython)
  n = 1
  ref = C_element
FEATURE [App::DocumentObjectGroupPython] H_element107  label="H_element : 057"  # scripted group (container) (typed FeaturePython)
  n = 4
  ref = H_element
FEATURE [App::DocumentObjectGroupPython] N_element046  label="N_element : 019"  # scripted group (container) (typed FeaturePython)
  n = 2
  ref = N_element
FEATURE [App::DocumentObjectGroupPython] O_element101  label="O_element : 055"  # scripted group (container) (typed FeaturePython)
  n = 1
  ref = O_element
FEATURE [App::DocumentObjectGroupPython] G4_UREA  # scripted group (container) (typed FeaturePython)
  Dunit = g/cm3
  Dvalue = 1.323
  Group = -> [C_element119,H_element107,N_element046,O_element101]
  conduct = 2
  density = 1
  expand = 3
  formula = G4_UREA
  name = G4_UREA
  specific = 4
FEATURE [App::DocumentObjectGroupPython] C_element120  label="C_element : 067"  # scripted group (container) (typed FeaturePython)
  n = 5
  ref = C_element
FEATURE [App::DocumentObjectGroupPython] H_element108  label="H_element : 058"  # scripted group (container) (typed FeaturePython)
  n = 11
  ref = H_element
FEATURE [App::DocumentObjectGroupPython] N_element047  label="N_element : 020"  # scripted group (container) (typed FeaturePython)
  n = 1
  ref = N_element
FEATURE [App::DocumentObjectGroupPython] O_element102  label="O_element : 056"  # scripted group (container) (typed FeaturePython)
  n = 2
  ref = O_element
FEATURE [App::DocumentObjectGroupPython] G4_VALINE  # scripted group (container) (typed FeaturePython)
  Dunit = g/cm3
  Dvalue = 1.23
  Group = -> [C_element120,H_element108,N_element047,O_element102]
  conduct = 2
  density = 1
  expand = 3
  formula = G4_VALINE
  name = G4_VALINE
  specific = 4
FEATURE [App::DocumentObjectGroupPython] H_element109  label="H_element : 0.009"  # scripted group (container) (typed FeaturePython)
  n = 0.009417
FEATURE [App::DocumentObjectGroupPython] C_element121  label="C_element : 0.281"  # scripted group (container) (typed FeaturePython)
  n = 0.280555
FEATURE [App::DocumentObjectGroupPython] F_element018  label="F_element : 0.710"  # scripted group (container) (typed FeaturePython)
  n = 0.710028
FEATURE [App::DocumentObjectGroupPython] G4_VITON  # scripted group (container) (typed FeaturePython)
  Dunit = g/cm3
  Dvalue = 1.8
  Group = -> [H_element109,C_element121,F_element018]
  conduct = 2
  density = 1
  expand = 3
  formula = G4_VITON
  name = G4_VITON
  specific = 4
FEATURE [App::DocumentObjectGroupPython] H_element110  label="H_element : 059"  # scripted group (container) (typed FeaturePython)
  n = 2
  ref = H_element
FEATURE [App::DocumentObjectGroupPython] O_element103  label="O_element : 057"  # scripted group (container) (typed FeaturePython)
  n = 1
  ref = O_element
FEATURE [App::DocumentObjectGroupPython] G4_WATER  # scripted group (container) (typed FeaturePython)
  Dunit = g/cm3
  Dvalue = 1
  Group = -> [H_element110,O_element103]
  conduct = 2
  density = 1
  expand = 3
  formula = G4_WATER
  name = G4_WATER
  specific = 4
FEATURE [App::DocumentObjectGroupPython] H_element111  label="H_element : 060"  # scripted group (container) (typed FeaturePython)
  n = 2
  ref = H_element
FEATURE [App::DocumentObjectGroupPython] O_element104  label="O_element : 058"  # scripted group (container) (typed FeaturePython)
  n = 1
  ref = O_element
FEATURE [App::DocumentObjectGroupPython] G4_WATER_VAPOR  # scripted group (container) (typed FeaturePython)
  Dunit = g/cm3
  Dvalue = 0.000756182
  Group = -> [H_element111,O_element104]
  conduct = 2
  density = 1
  expand = 3
  formula = G4_WATER_VAPOR
  name = G4_WATER_VAPOR
  specific = 4
FEATURE [App::DocumentObjectGroupPython] C_element122  label="C_element : 068"  # scripted group (container) (typed FeaturePython)
  n = 8
  ref = C_element
FEATURE [App::DocumentObjectGroupPython] H_element112  label="H_element : 061"  # scripted group (container) (typed FeaturePython)
  n = 10
  ref = H_element
FEATURE [App::DocumentObjectGroupPython] G4_XYLENE  # scripted group (container) (typed FeaturePython)
  Dunit = g/cm3
  Dvalue = 0.87
  Group = -> [C_element122,H_element112]
  conduct = 2
  density = 1
  expand = 3
  formula = G4_XYLENE
  name = G4_XYLENE
  specific = 4
FEATURE [App::DocumentObjectGroupPython] C_element123  label="C_element : 069"  # scripted group (container) (typed FeaturePython)
  n = 1
  ref = C_element
FEATURE [App::DocumentObjectGroupPython] G4_GRAPHITE  # scripted group (container) (typed FeaturePython)
  Dunit = g/cm3
  Dvalue = 2.21
  Group = -> [C_element123]
  conduct = 2
  density = 1
  expand = 3
  formula = G4_GRAPHITE
  name = G4_GRAPHITE
  specific = 4
FEATURE [App::DocumentObjectGroupPython] NIST  # scripted group (container) (typed FeaturePython)
  Group = -> [G4_A_150_TISSUE,G4_ACETONE,G4_ACETYLENE,G4_ADENINE,G4_ADIPOSE_TISSUE_ICRP,G4_AIR,G4_ALANINE,G4_ALUMINUM_OXIDE,G4_AMBER,G4_AMMONIA,G4_ANILINE,G4_ANTHRACENE,G4_B_100_BONE,G4_BAKELITE,G4_BARIUM_FLUORIDE,G4_BARIUM_SULFATE,G4_BENZENE,G4_BERYLLIUM_OXIDE,G4_BGO,G4_BLOOD_ICRP,G4_BONE_COMPACT_ICRU,G4_BONE_CORTICAL_ICRP,G4_BORON_CARBIDE,G4_BORON_OXIDE,G4_BRAIN_ICRP,G4_BUTANE,G4_N_BUTYL_ALCOHOL,G4_C_552,+152 more]
FEATURE [App::DocumentObjectGroupPython] H_element113  label="H_element : 062"  # scripted group (container) (typed FeaturePython)
  n = 1
  ref = H_element
FEATURE [App::DocumentObjectGroupPython] G4_H  # scripted group (container) (typed FeaturePython)
  Dunit = g/cm3
  Dvalue = 8.3748e-05
  Group = -> [H_element113]
  conduct = 2
  density = 1
  expand = 3
  formula = H
  name = G4_H
  specific = 4
FEATURE [App::DocumentObjectGroupPython] He_element001  label="He_element : 1"  # scripted group (container) (typed FeaturePython)
  n = 1
  ref = He_element
FEATURE [App::DocumentObjectGroupPython] G4_He  # scripted group (container) (typed FeaturePython)
  Dunit = g/cm3
  Dvalue = 0.000166322
  Group = -> [He_element001]
  conduct = 2
  density = 1
  expand = 3
  formula = He
  name = G4_He
  specific = 4
FEATURE [App::DocumentObjectGroupPython] Li_element008  label="Li_element : 008"  # scripted group (container) (typed FeaturePython)
  n = 1
  ref = Li_element
FEATURE [App::DocumentObjectGroupPython] G4_Li  # scripted group (container) (typed FeaturePython)
  Dunit = g/cm3
  Dvalue = 0.534
  Group = -> [Li_element008]
  conduct = 2
  density = 1
  expand = 3
  formula = Li
  name = G4_Li
  specific = 4
FEATURE [App::DocumentObjectGroupPython] Be_element002  label="Be_element : 002"  # scripted group (container) (typed FeaturePython)
  n = 1
  ref = Be_element
FEATURE [App::DocumentObjectGroupPython] G4_Be  # scripted group (container) (typed FeaturePython)
  Dunit = g/cm3
  Dvalue = 1.848
  Group = -> [Be_element002]
  conduct = 2
  density = 1
  expand = 3
  formula = Be
  name = G4_Be
  specific = 4
FEATURE [App::DocumentObjectGroupPython] B_element007  label="B_element : 007"  # scripted group (container) (typed FeaturePython)
  n = 1
  ref = B_element
FEATURE [App::DocumentObjectGroupPython] G4_B  # scripted group (container) (typed FeaturePython)
  Dunit = g/cm3
  Dvalue = 2.37
  Group = -> [B_element007]
  conduct = 2
  density = 1
  expand = 3
  formula = B
  name = G4_B
  specific = 4
FEATURE [App::DocumentObjectGroupPython] C_element124  label="C_element : 070"  # scripted group (container) (typed FeaturePython)
  n = 1
  ref = C_element
FEATURE [App::DocumentObjectGroupPython] G4_C  # scripted group (container) (typed FeaturePython)
  Dunit = g/cm3
  Dvalue = 2
  Group = -> [C_element124]
  conduct = 2
  density = 1
  expand = 3
  formula = C
  name = G4_C
  specific = 4
FEATURE [App::DocumentObjectGroupPython] N_element048  label="N_element : 021"  # scripted group (container) (typed FeaturePython)
  n = 1
  ref = N_element
FEATURE [App::DocumentObjectGroupPython] G4_N  # scripted group (container) (typed FeaturePython)
  Dunit = g/cm3
  Dvalue = 0.0011652
  Group = -> [N_element048]
  conduct = 2
  density = 1
  expand = 3
  formula = N
  name = G4_N
  specific = 4
FEATURE [App::DocumentObjectGroupPython] O_element105  label="O_element : 059"  # scripted group (container) (typed FeaturePython)
  n = 1
  ref = O_element
FEATURE [App::DocumentObjectGroupPython] G4_O  # scripted group (container) (typed FeaturePython)
  Dunit = g/cm3
  Dvalue = 0.00133151
  Group = -> [O_element105]
  conduct = 2
  density = 1
  expand = 3
  formula = O
  name = G4_O
  specific = 4
FEATURE [App::DocumentObjectGroupPython] F_element019  label="F_element : 008"  # scripted group (container) (typed FeaturePython)
  n = 1
  ref = F_element
FEATURE [App::DocumentObjectGroupPython] G4_F  # scripted group (container) (typed FeaturePython)
  Dunit = g/cm3
  Dvalue = 0.00158029
  Group = -> [F_element019]
  conduct = 2
  density = 1
  expand = 3
  formula = F
  name = G4_F
  specific = 4
FEATURE [App::DocumentObjectGroupPython] Ne_element001  label="Ne_element : 1"  # scripted group (container) (typed FeaturePython)
  n = 1
  ref = Ne_element
FEATURE [App::DocumentObjectGroupPython] G4_Ne  # scripted group (container) (typed FeaturePython)
  Dunit = g/cm3
  Dvalue = 0.000838505
  Group = -> [Ne_element001]
  conduct = 2
  density = 1
  expand = 3
  formula = Ne
  name = G4_Ne
  specific = 4
FEATURE [App::DocumentObjectGroupPython] Na_element020  label="Na_element : 005"  # scripted group (container) (typed FeaturePython)
  n = 1
  ref = Na_element
FEATURE [App::DocumentObjectGroupPython] G4_Na  # scripted group (container) (typed FeaturePython)
  Dunit = g/cm3
  Dvalue = 0.971
  Group = -> [Na_element020]
  conduct = 2
  density = 1
  expand = 3
  formula = Na
  name = G4_Na
  specific = 4
FEATURE [App::DocumentObjectGroupPython] Mg_element011  label="Mg_element : 005"  # scripted group (container) (typed FeaturePython)
  n = 1
  ref = Mg_element
FEATURE [App::DocumentObjectGroupPython] G4_Mg  # scripted group (container) (typed FeaturePython)
  Dunit = g/cm3
  Dvalue = 1.74
  Group = -> [Mg_element011]
  conduct = 2
  density = 1
  expand = 3
  formula = Mg
  name = G4_Mg
  specific = 4
FEATURE [App::DocumentObjectGroupPython] Al_element004  label="Al_element : 1"  # scripted group (container) (typed FeaturePython)
  n = 1
  ref = Al_element
FEATURE [App::DocumentObjectGroupPython] G4_Al  # scripted group (container) (typed FeaturePython)
  Dunit = g/cm3
  Dvalue = 2.699
  Group = -> [Al_element004]
  conduct = 2
  density = 1
  expand = 3
  formula = Al
  name = G4_Al
  specific = 4
FEATURE [App::DocumentObjectGroupPython] Si_element007  label="Si_element : 002"  # scripted group (container) (typed FeaturePython)
  n = 1
  ref = Si_element
FEATURE [App::DocumentObjectGroupPython] G4_Si  # scripted group (container) (typed FeaturePython)
  Dunit = g/cm3
  Dvalue = 2.33
  Group = -> [Si_element007]
  conduct = 2
  density = 1
  expand = 3
  formula = Si
  name = G4_Si
  specific = 4
FEATURE [App::DocumentObjectGroupPython] P_element013  label="P_element : 002"  # scripted group (container) (typed FeaturePython)
  n = 1
  ref = P_element
FEATURE [App::DocumentObjectGroupPython] G4_P  # scripted group (container) (typed FeaturePython)
  Dunit = g/cm3
  Dvalue = 2.2
  Group = -> [P_element013]
  conduct = 2
  density = 1
  expand = 3
  formula = P
  name = G4_P
  specific = 4
FEATURE [App::DocumentObjectGroupPython] S_element023  label="S_element : 007"  # scripted group (container) (typed FeaturePython)
  n = 1
  ref = S_element
FEATURE [App::DocumentObjectGroupPython] G4_S  # scripted group (container) (typed FeaturePython)
  Dunit = g/cm3
  Dvalue = 2
  Group = -> [S_element023]
  conduct = 2
  density = 1
  expand = 3
  formula = S
  name = G4_S
  specific = 4
FEATURE [App::DocumentObjectGroupPython] Cl_element029  label="Cl_element : 015"  # scripted group (container) (typed FeaturePython)
  n = 1
  ref = Cl_element
FEATURE [App::DocumentObjectGroupPython] G4_Cl  # scripted group (container) (typed FeaturePython)
  Dunit = g/cm3
  Dvalue = 0.00299473
  Group = -> [Cl_element029]
  conduct = 2
  density = 1
  expand = 3
  formula = Cl
  name = G4_Cl
  specific = 4
FEATURE [App::DocumentObjectGroupPython] Ar_element002  label="Ar_element : 1"  # scripted group (container) (typed FeaturePython)
  n = 1
  ref = Ar_element
FEATURE [App::DocumentObjectGroupPython] G4_Ar  # scripted group (container) (typed FeaturePython)
  Dunit = g/cm3
  Dvalue = 0.00166201
  Group = -> [Ar_element002]
  conduct = 2
  density = 1
  expand = 3
  formula = Ar
  name = G4_Ar
  specific = 4
FEATURE [App::DocumentObjectGroupPython] K_element013  label="K_element : 003"  # scripted group (container) (typed FeaturePython)
  n = 1
  ref = K_element
FEATURE [App::DocumentObjectGroupPython] G4_K  # scripted group (container) (typed FeaturePython)
  Dunit = g/cm3
  Dvalue = 0.862
  Group = -> [K_element013]
  conduct = 2
  density = 1
  expand = 3
  formula = K
  name = G4_K
  specific = 4
FEATURE [App::DocumentObjectGroupPython] Ca_element014  label="Ca_element : 007"  # scripted group (container) (typed FeaturePython)
  n = 1
  ref = Ca_element
FEATURE [App::DocumentObjectGroupPython] G4_Ca  # scripted group (container) (typed FeaturePython)
  Dunit = g/cm3
  Dvalue = 1.55
  Group = -> [Ca_element014]
  conduct = 2
  density = 1
  expand = 3
  formula = Ca
  name = G4_Ca
  specific = 4
FEATURE [App::DocumentObjectGroupPython] Sc_element001  label="Sc_element : 1"  # scripted group (container) (typed FeaturePython)
  n = 1
  ref = Sc_element
FEATURE [App::DocumentObjectGroupPython] G4_Sc  # scripted group (container) (typed FeaturePython)
  Dunit = g/cm3
  Dvalue = 2.989
  Group = -> [Sc_element001]
  conduct = 2
  density = 1
  expand = 3
  formula = Sc
  name = G4_Sc
  specific = 4
FEATURE [App::DocumentObjectGroupPython] Ti_element004  label="Ti_element : 002"  # scripted group (container) (typed FeaturePython)
  n = 1
  ref = Ti_element
FEATURE [App::DocumentObjectGroupPython] G4_Ti  # scripted group (container) (typed FeaturePython)
  Dunit = g/cm3
  Dvalue = 4.54
  Group = -> [Ti_element004]
  conduct = 2
  density = 1
  expand = 3
  formula = Ti
  name = G4_Ti
  specific = 4
FEATURE [App::DocumentObjectGroupPython] V_element001  label="V_element : 1"  # scripted group (container) (typed FeaturePython)
  n = 1
  ref = V_element
FEATURE [App::DocumentObjectGroupPython] G4_V  # scripted group (container) (typed FeaturePython)
  Dunit = g/cm3
  Dvalue = 6.11
  Group = -> [V_element001]
  conduct = 2
  density = 1
  expand = 3
  formula = V
  name = G4_V
  specific = 4
FEATURE [App::DocumentObjectGroupPython] Cr_element001  label="Cr_element : 1"  # scripted group (container) (typed FeaturePython)
  n = 1
  ref = Cr_element
FEATURE [App::DocumentObjectGroupPython] G4_Cr  # scripted group (container) (typed FeaturePython)
  Dunit = g/cm3
  Dvalue = 7.18
  Group = -> [Cr_element001]
  conduct = 2
  density = 1
  expand = 3
  formula = Cr
  name = G4_Cr
  specific = 4
FEATURE [App::DocumentObjectGroupPython] Mn_element001  label="Mn_element : 1"  # scripted group (container) (typed FeaturePython)
  n = 1
  ref = Mn_element
FEATURE [App::DocumentObjectGroupPython] G4_Mn  # scripted group (container) (typed FeaturePython)
  Dunit = g/cm3
  Dvalue = 7.44
  Group = -> [Mn_element001]
  conduct = 2
  density = 1
  expand = 3
  formula = Mn
  name = G4_Mn
  specific = 4
FEATURE [App::DocumentObjectGroupPython] Fe_element007  label="Fe_element : 004"  # scripted group (container) (typed FeaturePython)
  n = 1
  ref = Fe_element
FEATURE [App::DocumentObjectGroupPython] G4_Fe  # scripted group (container) (typed FeaturePython)
  Dunit = g/cm3
  Dvalue = 7.874
  Group = -> [Fe_element007]
  conduct = 2
  density = 1
  expand = 3
  formula = Fe
  name = G4_Fe
  specific = 4
FEATURE [App::DocumentObjectGroupPython] Co_element001  label="Co_element : 1"  # scripted group (container) (typed FeaturePython)
  n = 1
  ref = Co_element
FEATURE [App::DocumentObjectGroupPython] G4_Co  # scripted group (container) (typed FeaturePython)
  Dunit = g/cm3
  Dvalue = 8.9
  Group = -> [Co_element001]
  conduct = 2
  density = 1
  expand = 3
  formula = Co
  name = G4_Co
  specific = 4
FEATURE [App::DocumentObjectGroupPython] Ni_element001  label="Ni_element : 1"  # scripted group (container) (typed FeaturePython)
  n = 1
  ref = Ni_element
FEATURE [App::DocumentObjectGroupPython] G4_Ni  # scripted group (container) (typed FeaturePython)
  Dunit = g/cm3
  Dvalue = 8.902
  Group = -> [Ni_element001]
  conduct = 2
  density = 1
  expand = 3
  formula = Ni
  name = G4_Ni
  specific = 4
FEATURE [App::DocumentObjectGroupPython] Cu_element001  label="Cu_element : 1"  # scripted group (container) (typed FeaturePython)
  n = 1
  ref = Cu_element
FEATURE [App::DocumentObjectGroupPython] G4_Cu  # scripted group (container) (typed FeaturePython)
  Dunit = g/cm3
  Dvalue = 8.96
  Group = -> [Cu_element001]
  conduct = 2
  density = 1
  expand = 3
  formula = Cu
  name = G4_Cu
  specific = 4
FEATURE [App::DocumentObjectGroupPython] Zn_element001  label="Zn_element : 1"  # scripted group (container) (typed FeaturePython)
  n = 1
  ref = Zn_element
FEATURE [App::DocumentObjectGroupPython] G4_Zn  # scripted group (container) (typed FeaturePython)
  Dunit = g/cm3
  Dvalue = 7.133
  Group = -> [Zn_element001]
  conduct = 2
  density = 1
  expand = 3
  formula = Zn
  name = G4_Zn
  specific = 4
FEATURE [App::DocumentObjectGroupPython] Ga_element002  label="Ga_element : 002"  # scripted group (container) (typed FeaturePython)
  n = 1
  ref = Ga_element
FEATURE [App::DocumentObjectGroupPython] G4_Ga  # scripted group (container) (typed FeaturePython)
  Dunit = g/cm3
  Dvalue = 5.904
  Group = -> [Ga_element002]
  conduct = 2
  density = 1
  expand = 3
  formula = Ga
  name = G4_Ga
  specific = 4
FEATURE [App::DocumentObjectGroupPython] Ge_element002  label="Ge_element : 1"  # scripted group (container) (typed FeaturePython)
  n = 1
  ref = Ge_element
FEATURE [App::DocumentObjectGroupPython] G4_Ge  # scripted group (container) (typed FeaturePython)
  Dunit = g/cm3
  Dvalue = 5.323
  Group = -> [Ge_element002]
  conduct = 2
  density = 1
  expand = 3
  formula = Ge
  name = G4_Ge
  specific = 4
FEATURE [App::DocumentObjectGroupPython] As_element003  label="As_element : 002"  # scripted group (container) (typed FeaturePython)
  n = 1
  ref = As_element
FEATURE [App::DocumentObjectGroupPython] G4_As  # scripted group (container) (typed FeaturePython)
  Dunit = g/cm3
  Dvalue = 5.73
  Group = -> [As_element003]
  conduct = 2
  density = 1
  expand = 3
  formula = As
  name = G4_As
  specific = 4
FEATURE [App::DocumentObjectGroupPython] Se_element001  label="Se_element : 1"  # scripted group (container) (typed FeaturePython)
  n = 1
  ref = Se_element
FEATURE [App::DocumentObjectGroupPython] G4_Se  # scripted group (container) (typed FeaturePython)
  Dunit = g/cm3
  Dvalue = 4.5
  Group = -> [Se_element001]
  conduct = 2
  density = 1
  expand = 3
  formula = Se
  name = G4_Se
  specific = 4
FEATURE [App::DocumentObjectGroupPython] Br_element007  label="Br_element : 004"  # scripted group (container) (typed FeaturePython)
  n = 1
  ref = Br_element
FEATURE [App::DocumentObjectGroupPython] G4_Br  # scripted group (container) (typed FeaturePython)
  Dunit = g/cm3
  Dvalue = 0.0070721
  Group = -> [Br_element007]
  conduct = 2
  density = 1
  expand = 3
  formula = Br
  name = G4_Br
  specific = 4
FEATURE [App::DocumentObjectGroupPython] Kr_element001  label="Kr_element : 1"  # scripted group (container) (typed FeaturePython)
  n = 1
  ref = Kr_element
FEATURE [App::DocumentObjectGroupPython] G4_Kr  # scripted group (container) (typed FeaturePython)
  Dunit = g/cm3
  Dvalue = 0.00347832
  Group = -> [Kr_element001]
  conduct = 2
  density = 1
  expand = 3
  formula = Kr
  name = G4_Kr
  specific = 4
FEATURE [App::DocumentObjectGroupPython] Rb_element001  label="Rb_element : 1"  # scripted group (container) (typed FeaturePython)
  n = 1
  ref = Rb_element
FEATURE [App::DocumentObjectGroupPython] G4_Rb  # scripted group (container) (typed FeaturePython)
  Dunit = g/cm3
  Dvalue = 1.532
  Group = -> [Rb_element001]
  conduct = 2
  density = 1
  expand = 3
  formula = Rb
  name = G4_Rb
  specific = 4
FEATURE [App::DocumentObjectGroupPython] Sr_element001  label="Sr_element : 1"  # scripted group (container) (typed FeaturePython)
  n = 1
  ref = Sr_element
FEATURE [App::DocumentObjectGroupPython] G4_Sr  # scripted group (container) (typed FeaturePython)
  Dunit = g/cm3
  Dvalue = 2.54
  Group = -> [Sr_element001]
  conduct = 2
  density = 1
  expand = 3
  formula = Sr
  name = G4_Sr
  specific = 4
FEATURE [App::DocumentObjectGroupPython] Y_element001  label="Y_element : 1"  # scripted group (container) (typed FeaturePython)
  n = 1
  ref = Y_element
FEATURE [App::DocumentObjectGroupPython] G4_Y  # scripted group (container) (typed FeaturePython)
  Dunit = g/cm3
  Dvalue = 4.469
  Group = -> [Y_element001]
  conduct = 2
  density = 1
  expand = 3
  formula = Y
  name = G4_Y
  specific = 4
FEATURE [App::DocumentObjectGroupPython] Zr_element001  label="Zr_element : 1"  # scripted group (container) (typed FeaturePython)
  n = 1
  ref = Zr_element
FEATURE [App::DocumentObjectGroupPython] G4_Zr  # scripted group (container) (typed FeaturePython)
  Dunit = g/cm3
  Dvalue = 6.506
  Group = -> [Zr_element001]
  conduct = 2
  density = 1
  expand = 3
  formula = Zr
  name = G4_Zr
  specific = 4
FEATURE [App::DocumentObjectGroupPython] Nb_element001  label="Nb_element : 1"  # scripted group (container) (typed FeaturePython)
  n = 1
  ref = Nb_element
FEATURE [App::DocumentObjectGroupPython] G4_Nb  # scripted group (container) (typed FeaturePython)
  Dunit = g/cm3
  Dvalue = 8.57
  Group = -> [Nb_element001]
  conduct = 2
  density = 1
  expand = 3
  formula = Nb
  name = G4_Nb
  specific = 4
FEATURE [App::DocumentObjectGroupPython] Mo_element001  label="Mo_element : 1"  # scripted group (container) (typed FeaturePython)
  n = 1
  ref = Mo_element
FEATURE [App::DocumentObjectGroupPython] G4_Mo  # scripted group (container) (typed FeaturePython)
  Dunit = g/cm3
  Dvalue = 10.22
  Group = -> [Mo_element001]
  conduct = 2
  density = 1
  expand = 3
  formula = Mo
  name = G4_Mo
  specific = 4
FEATURE [App::DocumentObjectGroupPython] Tc_element001  label="Tc_element : 1"  # scripted group (container) (typed FeaturePython)
  n = 1
  ref = Tc_element
FEATURE [App::DocumentObjectGroupPython] G4_Tc  # scripted group (container) (typed FeaturePython)
  Dunit = g/cm3
  Dvalue = 11.5
  Group = -> [Tc_element001]
  conduct = 2
  density = 1
  expand = 3
  formula = Tc
  name = G4_Tc
  specific = 4
FEATURE [App::DocumentObjectGroupPython] Ru_element001  label="Ru_element : 1"  # scripted group (container) (typed FeaturePython)
  n = 1
  ref = Ru_element
FEATURE [App::DocumentObjectGroupPython] G4_Ru  # scripted group (container) (typed FeaturePython)
  Dunit = g/cm3
  Dvalue = 12.41
  Group = -> [Ru_element001]
  conduct = 2
  density = 1
  expand = 3
  formula = Ru
  name = G4_Ru
  specific = 4
FEATURE [App::DocumentObjectGroupPython] Rh_element001  label="Rh_element : 1"  # scripted group (container) (typed FeaturePython)
  n = 1
  ref = Rh_element
FEATURE [App::DocumentObjectGroupPython] G4_Rh  # scripted group (container) (typed FeaturePython)
  Dunit = g/cm3
  Dvalue = 12.41
  Group = -> [Rh_element001]
  conduct = 2
  density = 1
  expand = 3
  formula = Rh
  name = G4_Rh
  specific = 4
FEATURE [App::DocumentObjectGroupPython] Pd_element001  label="Pd_element : 1"  # scripted group (container) (typed FeaturePython)
  n = 1
  ref = Pd_element
FEATURE [App::DocumentObjectGroupPython] G4_Pd  # scripted group (container) (typed FeaturePython)
  Dunit = g/cm3
  Dvalue = 12.02
  Group = -> [Pd_element001]
  conduct = 2
  density = 1
  expand = 3
  formula = Pd
  name = G4_Pd
  specific = 4
FEATURE [App::DocumentObjectGroupPython] Ag_element006  label="Ag_element : 004"  # scripted group (container) (typed FeaturePython)
  n = 1
  ref = Ag_element
FEATURE [App::DocumentObjectGroupPython] G4_Ag  # scripted group (container) (typed FeaturePython)
  Dunit = g/cm3
  Dvalue = 10.5
  Group = -> [Ag_element006]
  conduct = 2
  density = 1
  expand = 3
  formula = Ag
  name = G4_Ag
  specific = 4
FEATURE [App::DocumentObjectGroupPython] Cd_element003  label="Cd_element : 003"  # scripted group (container) (typed FeaturePython)
  n = 1
  ref = Cd_element
FEATURE [App::DocumentObjectGroupPython] G4_Cd  # scripted group (container) (typed FeaturePython)
  Dunit = g/cm3
  Dvalue = 8.65
  Group = -> [Cd_element003]
  conduct = 2
  density = 1
  expand = 3
  formula = Cd
  name = G4_Cd
  specific = 4
FEATURE [App::DocumentObjectGroupPython] In_element001  label="In_element : 1"  # scripted group (container) (typed FeaturePython)
  n = 1
  ref = In_element
FEATURE [App::DocumentObjectGroupPython] G4_In  # scripted group (container) (typed FeaturePython)
  Dunit = g/cm3
  Dvalue = 7.31
  Group = -> [In_element001]
  conduct = 2
  density = 1
  expand = 3
  formula = In
  name = G4_In
  specific = 4
FEATURE [App::DocumentObjectGroupPython] Sn_element001  label="Sn_element : 1"  # scripted group (container) (typed FeaturePython)
  n = 1
  ref = Sn_element
FEATURE [App::DocumentObjectGroupPython] G4_Sn  # scripted group (container) (typed FeaturePython)
  Dunit = g/cm3
  Dvalue = 7.31
  Group = -> [Sn_element001]
  conduct = 2
  density = 1
  expand = 3
  formula = Sn
  name = G4_Sn
  specific = 4
FEATURE [App::DocumentObjectGroupPython] Sb_element001  label="Sb_element : 1"  # scripted group (container) (typed FeaturePython)
  n = 1
  ref = Sb_element
FEATURE [App::DocumentObjectGroupPython] G4_Sb  # scripted group (container) (typed FeaturePython)
  Dunit = g/cm3
  Dvalue = 6.691
  Group = -> [Sb_element001]
  conduct = 2
  density = 1
  expand = 3
  formula = Sb
  name = G4_Sb
  specific = 4
FEATURE [App::DocumentObjectGroupPython] Te_element002  label="Te_element : 002"  # scripted group (container) (typed FeaturePython)
  n = 1
  ref = Te_element
FEATURE [App::DocumentObjectGroupPython] G4_Te  # scripted group (container) (typed FeaturePython)
  Dunit = g/cm3
  Dvalue = 6.24
  Group = -> [Te_element002]
  conduct = 2
  density = 1
  expand = 3
  formula = Te
  name = G4_Te
  specific = 4
FEATURE [App::DocumentObjectGroupPython] I_element010  label="I_element : 006"  # scripted group (container) (typed FeaturePython)
  n = 1
  ref = I_element
FEATURE [App::DocumentObjectGroupPython] G4_I  # scripted group (container) (typed FeaturePython)
  Dunit = g/cm3
  Dvalue = 4.93
  Group = -> [I_element010]
  conduct = 2
  density = 1
  expand = 3
  formula = I
  name = G4_I
  specific = 4
FEATURE [App::DocumentObjectGroupPython] Xe_element001  label="Xe_element : 1"  # scripted group (container) (typed FeaturePython)
  n = 1
  ref = Xe_element
FEATURE [App::DocumentObjectGroupPython] G4_Xe  # scripted group (container) (typed FeaturePython)
  Dunit = g/cm3
  Dvalue = 0.00548536
  Group = -> [Xe_element001]
  conduct = 2
  density = 1
  expand = 3
  formula = Xe
  name = G4_Xe
  specific = 4
FEATURE [App::DocumentObjectGroupPython] Cs_element003  label="Cs_element : 003"  # scripted group (container) (typed FeaturePython)
  n = 1
  ref = Cs_element
FEATURE [App::DocumentObjectGroupPython] G4_Cs  # scripted group (container) (typed FeaturePython)
  Dunit = g/cm3
  Dvalue = 1.873
  Group = -> [Cs_element003]
  conduct = 2
  density = 1
  expand = 3
  formula = Cs
  name = G4_Cs
  specific = 4
FEATURE [App::DocumentObjectGroupPython] Ba_element003  label="Ba_element : 003"  # scripted group (container) (typed FeaturePython)
  n = 1
  ref = Ba_element
FEATURE [App::DocumentObjectGroupPython] G4_Ba  # scripted group (container) (typed FeaturePython)
  Dunit = g/cm3
  Dvalue = 3.5
  Group = -> [Ba_element003]
  conduct = 2
  density = 1
  expand = 3
  formula = Ba
  name = G4_Ba
  specific = 4
FEATURE [App::DocumentObjectGroupPython] La_element003  label="La_element : 003"  # scripted group (container) (typed FeaturePython)
  n = 1
  ref = La_element
FEATURE [App::DocumentObjectGroupPython] G4_La  # scripted group (container) (typed FeaturePython)
  Dunit = g/cm3
  Dvalue = 6.154
  Group = -> [La_element003]
  conduct = 2
  density = 1
  expand = 3
  formula = La
  name = G4_La
  specific = 4
FEATURE [App::DocumentObjectGroupPython] Ce_element002  label="Ce_element : 1"  # scripted group (container) (typed FeaturePython)
  n = 1
  ref = Ce_element
FEATURE [App::DocumentObjectGroupPython] G4_Ce  # scripted group (container) (typed FeaturePython)
  Dunit = g/cm3
  Dvalue = 6.657
  Group = -> [Ce_element002]
  conduct = 2
  density = 1
  expand = 3
  formula = Ce
  name = G4_Ce
  specific = 4
FEATURE [App::DocumentObjectGroupPython] Pr_element001  label="Pr_element : 1"  # scripted group (container) (typed FeaturePython)
  n = 1
  ref = Pr_element
FEATURE [App::DocumentObjectGroupPython] G4_Pr  # scripted group (container) (typed FeaturePython)
  Dunit = g/cm3
  Dvalue = 6.71
  Group = -> [Pr_element001]
  conduct = 2
  density = 1
  expand = 3
  formula = Pr
  name = G4_Pr
  specific = 4
FEATURE [App::DocumentObjectGroupPython] Nd_element001  label="Nd_element : 1"  # scripted group (container) (typed FeaturePython)
  n = 1
  ref = Nd_element
FEATURE [App::DocumentObjectGroupPython] G4_Nd  # scripted group (container) (typed FeaturePython)
  Dunit = g/cm3
  Dvalue = 6.9
  Group = -> [Nd_element001]
  conduct = 2
  density = 1
  expand = 3
  formula = Nd
  name = G4_Nd
  specific = 4
FEATURE [App::DocumentObjectGroupPython] Pm_element001  label="Pm_element : 1"  # scripted group (container) (typed FeaturePython)
  n = 1
  ref = Pm_element
FEATURE [App::DocumentObjectGroupPython] G4_Pm  # scripted group (container) (typed FeaturePython)
  Dunit = g/cm3
  Dvalue = 7.22
  Group = -> [Pm_element001]
  conduct = 2
  density = 1
  expand = 3
  formula = Pm
  name = G4_Pm
  specific = 4
FEATURE [App::DocumentObjectGroupPython] Sm_element001  label="Sm_element : 1"  # scripted group (container) (typed FeaturePython)
  n = 1
  ref = Sm_element
FEATURE [App::DocumentObjectGroupPython] G4_Sm  # scripted group (container) (typed FeaturePython)
  Dunit = g/cm3
  Dvalue = 7.46
  Group = -> [Sm_element001]
  conduct = 2
  density = 1
  expand = 3
  formula = Sm
  name = G4_Sm
  specific = 4
FEATURE [App::DocumentObjectGroupPython] Eu_element001  label="Eu_element : 1"  # scripted group (container) (typed FeaturePython)
  n = 1
  ref = Eu_element
FEATURE [App::DocumentObjectGroupPython] G4_Eu  # scripted group (container) (typed FeaturePython)
  Dunit = g/cm3
  Dvalue = 5.243
  Group = -> [Eu_element001]
  conduct = 2
  density = 1
  expand = 3
  formula = Eu
  name = G4_Eu
  specific = 4
FEATURE [App::DocumentObjectGroupPython] Gd_element002  label="Gd_element : 1"  # scripted group (container) (typed FeaturePython)
  n = 1
  ref = Gd_element
FEATURE [App::DocumentObjectGroupPython] G4_Gd  # scripted group (container) (typed FeaturePython)
  Dunit = g/cm3
  Dvalue = 7.9004
  Group = -> [Gd_element002]
  conduct = 2
  density = 1
  expand = 3
  formula = Gd
  name = G4_Gd
  specific = 4
FEATURE [App::DocumentObjectGroupPython] Tb_element001  label="Tb_element : 1"  # scripted group (container) (typed FeaturePython)
  n = 1
  ref = Tb_element
FEATURE [App::DocumentObjectGroupPython] G4_Tb  # scripted group (container) (typed FeaturePython)
  Dunit = g/cm3
  Dvalue = 8.229
  Group = -> [Tb_element001]
  conduct = 2
  density = 1
  expand = 3
  formula = Tb
  name = G4_Tb
  specific = 4
FEATURE [App::DocumentObjectGroupPython] Dy_element001  label="Dy_element : 1"  # scripted group (container) (typed FeaturePython)
  n = 1
  ref = Dy_element
FEATURE [App::DocumentObjectGroupPython] G4_Dy  # scripted group (container) (typed FeaturePython)
  Dunit = g/cm3
  Dvalue = 8.55
  Group = -> [Dy_element001]
  conduct = 2
  density = 1
  expand = 3
  formula = Dy
  name = G4_Dy
  specific = 4
FEATURE [App::DocumentObjectGroupPython] Ho_element001  label="Ho_element : 1"  # scripted group (container) (typed FeaturePython)
  n = 1
  ref = Ho_element
FEATURE [App::DocumentObjectGroupPython] G4_Ho  # scripted group (container) (typed FeaturePython)
  Dunit = g/cm3
  Dvalue = 8.795
  Group = -> [Ho_element001]
  conduct = 2
  density = 1
  expand = 3
  formula = Ho
  name = G4_Ho
  specific = 4
FEATURE [App::DocumentObjectGroupPython] Er_element001  label="Er_element : 1"  # scripted group (container) (typed FeaturePython)
  n = 1
  ref = Er_element
FEATURE [App::DocumentObjectGroupPython] G4_Er  # scripted group (container) (typed FeaturePython)
  Dunit = g/cm3
  Dvalue = 9.066
  Group = -> [Er_element001]
  conduct = 2
  density = 1
  expand = 3
  formula = Er
  name = G4_Er
  specific = 4
FEATURE [App::DocumentObjectGroupPython] Tm_element001  label="Tm_element : 1"  # scripted group (container) (typed FeaturePython)
  n = 1
  ref = Tm_element
FEATURE [App::DocumentObjectGroupPython] G4_Tm  # scripted group (container) (typed FeaturePython)
  Dunit = g/cm3
  Dvalue = 9.321
  Group = -> [Tm_element001]
  conduct = 2
  density = 1
  expand = 3
  formula = Tm
  name = G4_Tm
  specific = 4
FEATURE [App::DocumentObjectGroupPython] Yb_element001  label="Yb_element : 1"  # scripted group (container) (typed FeaturePython)
  n = 1
  ref = Yb_element
FEATURE [App::DocumentObjectGroupPython] G4_Yb  # scripted group (container) (typed FeaturePython)
  Dunit = g/cm3
  Dvalue = 6.73
  Group = -> [Yb_element001]
  conduct = 2
  density = 1
  expand = 3
  formula = Yb
  name = G4_Yb
  specific = 4
FEATURE [App::DocumentObjectGroupPython] Lu_element001  label="Lu_element : 1"  # scripted group (container) (typed FeaturePython)
  n = 1
  ref = Lu_element
FEATURE [App::DocumentObjectGroupPython] G4_Lu  # scripted group (container) (typed FeaturePython)
  Dunit = g/cm3
  Dvalue = 9.84
  Group = -> [Lu_element001]
  conduct = 2
  density = 1
  expand = 3
  formula = Lu
  name = G4_Lu
  specific = 4
FEATURE [App::DocumentObjectGroupPython] Hf_element001  label="Hf_element : 1"  # scripted group (container) (typed FeaturePython)
  n = 1
  ref = Hf_element
FEATURE [App::DocumentObjectGroupPython] G4_Hf  # scripted group (container) (typed FeaturePython)
  Dunit = g/cm3
  Dvalue = 13.31
  Group = -> [Hf_element001]
  conduct = 2
  density = 1
  expand = 3
  formula = Hf
  name = G4_Hf
  specific = 4
FEATURE [App::DocumentObjectGroupPython] Ta_element001  label="Ta_element : 1"  # scripted group (container) (typed FeaturePython)
  n = 1
  ref = Ta_element
FEATURE [App::DocumentObjectGroupPython] G4_Ta  # scripted group (container) (typed FeaturePython)
  Dunit = g/cm3
  Dvalue = 16.654
  Group = -> [Ta_element001]
  conduct = 2
  density = 1
  expand = 3
  formula = Ta
  name = G4_Ta
  specific = 4
FEATURE [App::DocumentObjectGroupPython] W_element004  label="W_element : 004"  # scripted group (container) (typed FeaturePython)
  n = 1
  ref = W_element
FEATURE [App::DocumentObjectGroupPython] G4_W  # scripted group (container) (typed FeaturePython)
  Dunit = g/cm3
  Dvalue = 19.3
  Group = -> [W_element004]
  conduct = 2
  density = 1
  expand = 3
  formula = W
  name = G4_W
  specific = 4
FEATURE [App::DocumentObjectGroupPython] Re_element001  label="Re_element : 1"  # scripted group (container) (typed FeaturePython)
  n = 1
  ref = Re_element
FEATURE [App::DocumentObjectGroupPython] G4_Re  # scripted group (container) (typed FeaturePython)
  Dunit = g/cm3
  Dvalue = 21.02
  Group = -> [Re_element001]
  conduct = 2
  density = 1
  expand = 3
  formula = Re
  name = G4_Re
  specific = 4
FEATURE [App::DocumentObjectGroupPython] Os_element001  label="Os_element : 1"  # scripted group (container) (typed FeaturePython)
  n = 1
  ref = Os_element
FEATURE [App::DocumentObjectGroupPython] G4_Os  # scripted group (container) (typed FeaturePython)
  Dunit = g/cm3
  Dvalue = 22.57
  Group = -> [Os_element001]
  conduct = 2
  density = 1
  expand = 3
  formula = Os
  name = G4_Os
  specific = 4
FEATURE [App::DocumentObjectGroupPython] Ir_element001  label="Ir_element : 1"  # scripted group (container) (typed FeaturePython)
  n = 1
  ref = Ir_element
FEATURE [App::DocumentObjectGroupPython] G4_Ir  # scripted group (container) (typed FeaturePython)
  Dunit = g/cm3
  Dvalue = 22.42
  Group = -> [Ir_element001]
  conduct = 2
  density = 1
  expand = 3
  formula = Ir
  name = G4_Ir
  specific = 4
FEATURE [App::DocumentObjectGroupPython] Pt_element001  label="Pt_element : 1"  # scripted group (container) (typed FeaturePython)
  n = 1
  ref = Pt_element
FEATURE [App::DocumentObjectGroupPython] G4_Pt  # scripted group (container) (typed FeaturePython)
  Dunit = g/cm3
  Dvalue = 21.45
  Group = -> [Pt_element001]
  conduct = 2
  density = 1
  expand = 3
  formula = Pt
  name = G4_Pt
  specific = 4
FEATURE [App::DocumentObjectGroupPython] Au_element001  label="Au_element : 1"  # scripted group (container) (typed FeaturePython)
  n = 1
  ref = Au_element
FEATURE [App::DocumentObjectGroupPython] G4_Au  # scripted group (container) (typed FeaturePython)
  Dunit = g/cm3
  Dvalue = 19.32
  Group = -> [Au_element001]
  conduct = 2
  density = 1
  expand = 3
  formula = Au
  name = G4_Au
  specific = 4
FEATURE [App::DocumentObjectGroupPython] Hg_element002  label="Hg_element : 002"  # scripted group (container) (typed FeaturePython)
  n = 1
  ref = Hg_element
FEATURE [App::DocumentObjectGroupPython] G4_Hg  # scripted group (container) (typed FeaturePython)
  Dunit = g/cm3
  Dvalue = 13.546
  Group = -> [Hg_element002]
  conduct = 2
  density = 1
  expand = 3
  formula = Hg
  name = G4_Hg
  specific = 4
FEATURE [App::DocumentObjectGroupPython] Tl_element002  label="Tl_element : 002"  # scripted group (container) (typed FeaturePython)
  n = 1
  ref = Tl_element
FEATURE [App::DocumentObjectGroupPython] G4_Tl  # scripted group (container) (typed FeaturePython)
  Dunit = g/cm3
  Dvalue = 11.72
  Group = -> [Tl_element002]
  conduct = 2
  density = 1
  expand = 3
  formula = Tl
  name = G4_Tl
  specific = 4
FEATURE [App::DocumentObjectGroupPython] Pb_element003  label="Pb_element : 1"  # scripted group (container) (typed FeaturePython)
  n = 1
  ref = Pb_element
FEATURE [App::DocumentObjectGroupPython] G4_Pb  # scripted group (container) (typed FeaturePython)
  Dunit = g/cm3
  Dvalue = 11.35
  Group = -> [Pb_element003]
  conduct = 2
  density = 1
  expand = 3
  formula = Pb
  name = G4_Pb
  specific = 4
FEATURE [App::DocumentObjectGroupPython] Bi_element002  label="Bi_element : 1"  # scripted group (container) (typed FeaturePython)
  n = 1
  ref = Bi_element
FEATURE [App::DocumentObjectGroupPython] G4_Bi  # scripted group (container) (typed FeaturePython)
  Dunit = g/cm3
  Dvalue = 9.747
  Group = -> [Bi_element002]
  conduct = 2
  density = 1
  expand = 3
  formula = Bi
  name = G4_Bi
  specific = 4
FEATURE [App::DocumentObjectGroupPython] Po_element001  label="Po_element : 1"  # scripted group (container) (typed FeaturePython)
  n = 1
  ref = Po_element
FEATURE [App::DocumentObjectGroupPython] G4_Po  # scripted group (container) (typed FeaturePython)
  Dunit = g/cm3
  Dvalue = 9.32
  Group = -> [Po_element001]
  conduct = 2
  density = 1
  expand = 3
  formula = Po
  name = G4_Po
  specific = 4
FEATURE [App::DocumentObjectGroupPython] At_element001  label="At_element : 1"  # scripted group (container) (typed FeaturePython)
  n = 1
  ref = At_element
FEATURE [App::DocumentObjectGroupPython] G4_At  # scripted group (container) (typed FeaturePython)
  Dunit = g/cm3
  Dvalue = 9.32
  Group = -> [At_element001]
  conduct = 2
  density = 1
  expand = 3
  formula = At
  name = G4_At
  specific = 4
FEATURE [App::DocumentObjectGroupPython] Rn_element001  label="Rn_element : 1"  # scripted group (container) (typed FeaturePython)
  n = 1
  ref = Rn_element
FEATURE [App::DocumentObjectGroupPython] G4_Rn  # scripted group (container) (typed FeaturePython)
  Dunit = g/cm3
  Dvalue = 0.00900662
  Group = -> [Rn_element001]
  conduct = 2
  density = 1
  expand = 3
  formula = Rn
  name = G4_Rn
  specific = 4
FEATURE [App::DocumentObjectGroupPython] Fr_element001  label="Fr_element : 1"  # scripted group (container) (typed FeaturePython)
  n = 1
  ref = Fr_element
FEATURE [App::DocumentObjectGroupPython] G4_Fr  # scripted group (container) (typed FeaturePython)
  Dunit = g/cm3
  Dvalue = 1
  Group = -> [Fr_element001]
  conduct = 2
  density = 1
  expand = 3
  formula = Fr
  name = G4_Fr
  specific = 4
FEATURE [App::DocumentObjectGroupPython] Ra_element001  label="Ra_element : 1"  # scripted group (container) (typed FeaturePython)
  n = 1
  ref = Ra_element
FEATURE [App::DocumentObjectGroupPython] G4_Ra  # scripted group (container) (typed FeaturePython)
  Dunit = g/cm3
  Dvalue = 5
  Group = -> [Ra_element001]
  conduct = 2
  density = 1
  expand = 3
  formula = Ra
  name = G4_Ra
  specific = 4
FEATURE [App::DocumentObjectGroupPython] Ac_element001  label="Ac_element : 1"  # scripted group (container) (typed FeaturePython)
  n = 1
  ref = Ac_element
FEATURE [App::DocumentObjectGroupPython] G4_Ac  # scripted group (container) (typed FeaturePython)
  Dunit = g/cm3
  Dvalue = 10.07
  Group = -> [Ac_element001]
  conduct = 2
  density = 1
  expand = 3
  formula = Ac
  name = G4_Ac
  specific = 4
FEATURE [App::DocumentObjectGroupPython] Th_element001  label="Th_element : 1"  # scripted group (container) (typed FeaturePython)
  n = 1
  ref = Th_element
FEATURE [App::DocumentObjectGroupPython] G4_Th  # scripted group (container) (typed FeaturePython)
  Dunit = g/cm3
  Dvalue = 11.72
  Group = -> [Th_element001]
  conduct = 2
  density = 1
  expand = 3
  formula = Th
  name = G4_Th
  specific = 4
FEATURE [App::DocumentObjectGroupPython] Pa_element001  label="Pa_element : 1"  # scripted group (container) (typed FeaturePython)
  n = 1
  ref = Pa_element
FEATURE [App::DocumentObjectGroupPython] G4_Pa  # scripted group (container) (typed FeaturePython)
  Dunit = g/cm3
  Dvalue = 15.37
  Group = -> [Pa_element001]
  conduct = 2
  density = 1
  expand = 3
  formula = Pa
  name = G4_Pa
  specific = 4
FEATURE [App::DocumentObjectGroupPython] U_element004  label="U_element : 004"  # scripted group (container) (typed FeaturePython)
  n = 1
  ref = U_element
FEATURE [App::DocumentObjectGroupPython] G4_U  # scripted group (container) (typed FeaturePython)
  Dunit = g/cm3
  Dvalue = 18.95
  Group = -> [U_element004]
  conduct = 2
  density = 1
  expand = 3
  formula = U
  name = G4_U
  specific = 4
FEATURE [App::DocumentObjectGroupPython] Np_element001  label="Np_element : 1"  # scripted group (container) (typed FeaturePython)
  n = 1
  ref = Np_element
FEATURE [App::DocumentObjectGroupPython] G4_Np  # scripted group (container) (typed FeaturePython)
  Dunit = g/cm3
  Dvalue = 20.25
  Group = -> [Np_element001]
  conduct = 2
  density = 1
  expand = 3
  formula = Np
  name = G4_Np
  specific = 4
FEATURE [App::DocumentObjectGroupPython] Pu_element002  label="Pu_element : 002"  # scripted group (container) (typed FeaturePython)
  n = 1
  ref = Pu_element
FEATURE [App::DocumentObjectGroupPython] G4_Pu  # scripted group (container) (typed FeaturePython)
  Dunit = g/cm3
  Dvalue = 19.84
  Group = -> [Pu_element002]
  conduct = 2
  density = 1
  expand = 3
  formula = Pu
  name = G4_Pu
  specific = 4
FEATURE [App::DocumentObjectGroupPython] Am_element001  label="Am_element : 1"  # scripted group (container) (typed FeaturePython)
  n = 1
  ref = Am_element
FEATURE [App::DocumentObjectGroupPython] G4_Am  # scripted group (container) (typed FeaturePython)
  Dunit = g/cm3
  Dvalue = 13.67
  Group = -> [Am_element001]
  conduct = 2
  density = 1
  expand = 3
  formula = Am
  name = G4_Am
  specific = 4
FEATURE [App::DocumentObjectGroupPython] Cm_element001  label="Cm_element : 1"  # scripted group (container) (typed FeaturePython)
  n = 1
  ref = Cm_element
FEATURE [App::DocumentObjectGroupPython] G4_Cm  # scripted group (container) (typed FeaturePython)
  Dunit = g/cm3
  Dvalue = 13.51
  Group = -> [Cm_element001]
  conduct = 2
  density = 1
  expand = 3
  formula = Cm
  name = G4_Cm
  specific = 4
FEATURE [App::DocumentObjectGroupPython] Bk_element001  label="Bk_element : 1"  # scripted group (container) (typed FeaturePython)
  n = 1
  ref = Bk_element
FEATURE [App::DocumentObjectGroupPython] G4_Bk  # scripted group (container) (typed FeaturePython)
  Dunit = g/cm3
  Dvalue = 14
  Group = -> [Bk_element001]
  conduct = 2
  density = 1
  expand = 3
  formula = Bk
  name = G4_Bk
  specific = 4
FEATURE [App::DocumentObjectGroupPython] Cf_element001  label="Cf_element : 1"  # scripted group (container) (typed FeaturePython)
  n = 1
  ref = Cf_element
FEATURE [App::DocumentObjectGroupPython] G4_Cf  # scripted group (container) (typed FeaturePython)
  Dunit = g/cm3
  Dvalue = 10
  Group = -> [Cf_element001]
  conduct = 2
  density = 1
  expand = 3
  formula = Cf
  name = G4_Cf
  specific = 4
FEATURE [App::DocumentObjectGroupPython] Element  # scripted group (container) (typed FeaturePython)
  Group = -> [G4_H,G4_He,G4_Li,G4_Be,G4_B,G4_C,G4_N,G4_O,G4_F,G4_Ne,G4_Na,G4_Mg,G4_Al,G4_Si,G4_P,G4_S,G4_Cl,G4_Ar,G4_K,G4_Ca,G4_Sc,G4_Ti,G4_V,G4_Cr,G4_Mn,G4_Fe,G4_Co,G4_Ni,G4_Cu,G4_Zn,G4_Ga,G4_Ge,G4_As,G4_Se,G4_Br,G4_Kr,G4_Rb,G4_Sr,G4_Y,G4_Zr,G4_Nb,G4_Mo,G4_Tc,G4_Ru,G4_Rh,G4_Pd,G4_Ag,G4_Cd,G4_In,G4_Sn,G4_Sb,G4_Te,G4_I,G4_Xe,G4_Cs,G4_Ba,G4_La,G4_Ce,G4_Pr,G4_Nd,G4_Pm,G4_Sm,G4_Eu,G4_Gd,G4_Tb,G4_Dy,G4_Ho,G4_Er,+30 more]
FEATURE [App::DocumentObjectGroupPython] H_element114  label="H_element : 063"  # scripted group (container) (typed FeaturePython)
  n = 2
  ref = H_element
FEATURE [App::DocumentObjectGroupPython] G4_lH2  # scripted group (container) (typed FeaturePython)
  Dunit = g/cm3
  Dvalue = 0.0708
  Group = -> [H_element114]
  conduct = 2
  density = 1
  expand = 3
  formula = G4_lH2
  name = G4_lH2
  specific = 4
FEATURE [App::DocumentObjectGroupPython] N_element049  label="N_element : 022"  # scripted group (container) (typed FeaturePython)
  n = 2
  ref = N_element
FEATURE [App::DocumentObjectGroupPython] G4_lN2  # scripted group (container) (typed FeaturePython)
  Dunit = g/cm3
  Dvalue = 0.807
  Group = -> [N_element049]
  conduct = 2
  density = 1
  expand = 3
  formula = G4_lN2
  name = G4_lN2
  specific = 4
FEATURE [App::DocumentObjectGroupPython] O_element106  label="O_element : 060"  # scripted group (container) (typed FeaturePython)
  n = 2
  ref = O_element
FEATURE [App::DocumentObjectGroupPython] G4_lO2  # scripted group (container) (typed FeaturePython)
  Dunit = g/cm3
  Dvalue = 1.141
  Group = -> [O_element106]
  conduct = 2
  density = 1
  expand = 3
  formula = G4_lO2
  name = G4_lO2
  specific = 4
FEATURE [App::DocumentObjectGroupPython] Ar  label="Ar : 1"  # scripted group (container) (typed FeaturePython)
  n = 1
  ref = Ar
FEATURE [App::DocumentObjectGroupPython] G4_lAr  # scripted group (container) (typed FeaturePython)
  Dunit = g/cm3
  Dvalue = 1.396
  Group = -> [Ar]
  conduct = 2
  density = 1
  expand = 3
  formula = G4_lAr
  name = G4_lAr
  specific = 4
FEATURE [App::DocumentObjectGroupPython] Br  label="Br : 1"  # scripted group (container) (typed FeaturePython)
  n = 1
  ref = Br
FEATURE [App::DocumentObjectGroupPython] G4_lBr  # scripted group (container) (typed FeaturePython)
  Dunit = g/cm3
  Dvalue = 3.1028
  Group = -> [Br]
  conduct = 2
  density = 1
  expand = 3
  formula = G4_lBr
  name = G4_lBr
  specific = 4
FEATURE [App::DocumentObjectGroupPython] Kr  label="Kr : 1"  # scripted group (container) (typed FeaturePython)
  n = 1
  ref = Kr
FEATURE [App::DocumentObjectGroupPython] G4_lKr  # scripted group (container) (typed FeaturePython)
  Dunit = g/cm3
  Dvalue = 2.418
  Group = -> [Kr]
  conduct = 2
  density = 1
  expand = 3
  formula = G4_lKr
  name = G4_lKr
  specific = 4
FEATURE [App::DocumentObjectGroupPython] Xe  label="Xe : 1"  # scripted group (container) (typed FeaturePython)
  n = 1
  ref = Xe
FEATURE [App::DocumentObjectGroupPython] G4_lXe  # scripted group (container) (typed FeaturePython)
  Dunit = g/cm3
  Dvalue = 2.953
  Group = -> [Xe]
  conduct = 2
  density = 1
  expand = 3
  formula = G4_lXe
  name = G4_lXe
  specific = 4
FEATURE [App::DocumentObjectGroupPython] O_element107  label="O_element : 061"  # scripted group (container) (typed FeaturePython)
  n = 4
  ref = O_element
FEATURE [App::DocumentObjectGroupPython] Pb_element004  label="Pb_element : 002"  # scripted group (container) (typed FeaturePython)
  n = 1
  ref = Pb_element
FEATURE [App::DocumentObjectGroupPython] W_element005  label="W_element : 005"  # scripted group (container) (typed FeaturePython)
  n = 1
  ref = W_element
FEATURE [App::DocumentObjectGroupPython] G4_PbWO4  # scripted group (container) (typed FeaturePython)
  Dunit = g/cm3
  Dvalue = 8.28
  Group = -> [O_element107,Pb_element004,W_element005]
  conduct = 2
  density = 1
  expand = 3
  formula = G4_PbWO4
  name = G4_PbWO4
  specific = 4
FEATURE [App::DocumentObjectGroupPython] alactic  label="alactic : 1"  # scripted group (container) (typed FeaturePython)
  n = 1
  ref = alactic
FEATURE [App::DocumentObjectGroupPython] G4_Galactic  # scripted group (container) (typed FeaturePython)
  Dunit = g/cm3
  Dvalue = 0
  Group = -> [alactic]
  conduct = 2
  density = 1
  expand = 3
  formula = G4_Galactic
  name = G4_Galactic
  specific = 4
FEATURE [App::DocumentObjectGroupPython] RAPHITE_POROUS  label="RAPHITE_POROUS : 1"  # scripted group (container) (typed FeaturePython)
  n = 1
  ref = RAPHITE_POROUS
FEATURE [App::DocumentObjectGroupPython] G4_GRAPHITE_POROUS  # scripted group (container) (typed FeaturePython)
  Dunit = g/cm3
  Dvalue = 1.7
  Group = -> [RAPHITE_POROUS]
  conduct = 2
  density = 1
  expand = 3
  formula = G4_GRAPHITE_POROUS
  name = G4_GRAPHITE_POROUS
  specific = 4
FEATURE [App::DocumentObjectGroupPython] H_element115  label="H_element : 0.150"  # scripted group (container) (typed FeaturePython)
  n = 0.080538
FEATURE [App::DocumentObjectGroupPython] C_element125  label="C_element : 0.600"  # scripted group (container) (typed FeaturePython)
  n = 0.599848
FEATURE [App::DocumentObjectGroupPython] O_element108  label="O_element : 0.320"  # scripted group (container) (typed FeaturePython)
  n = 0.319614
FEATURE [App::DocumentObjectGroupPython] G4_LUCITE  # scripted group (container) (typed FeaturePython)
  Dunit = g/cm3
  Dvalue = 1.19
  Group = -> [H_element115,C_element125,O_element108]
  conduct = 2
  density = 1
  expand = 3
  formula = G4_LUCITE
  name = G4_LUCITE
  specific = 4
FEATURE [App::DocumentObjectGroupPython] Cu_element002  label="Cu_element : 62"  # scripted group (container) (typed FeaturePython)
  n = 62
  ref = Cu_element
FEATURE [App::DocumentObjectGroupPython] Zn_element002  label="Zn_element : 35"  # scripted group (container) (typed FeaturePython)
  n = 35
  ref = Zn_element
FEATURE [App::DocumentObjectGroupPython] Pb_element005  label="Pb_element : 3"  # scripted group (container) (typed FeaturePython)
  n = 3
  ref = Pb_element
FEATURE [App::DocumentObjectGroupPython] G4_BRASS  # scripted group (container) (typed FeaturePython)
  Dunit = g/cm3
  Dvalue = 8.52
  Group = -> [Cu_element002,Zn_element002,Pb_element005]
  conduct = 2
  density = 1
  expand = 3
  formula = G4_BRASS
  name = G4_BRASS
  specific = 4
FEATURE [App::DocumentObjectGroupPython] Cu_element003  label="Cu_element : 89"  # scripted group (container) (typed FeaturePython)
  n = 89
  ref = Cu_element
FEATURE [App::DocumentObjectGroupPython] Zn_element003  label="Zn_element : 9"  # scripted group (container) (typed FeaturePython)
  n = 9
  ref = Zn_element
FEATURE [App::DocumentObjectGroupPython] Pb_element006  label="Pb_element : 2"  # scripted group (container) (typed FeaturePython)
  n = 2
  ref = Pb_element
FEATURE [App::DocumentObjectGroupPython] G4_BRONZE  # scripted group (container) (typed FeaturePython)
  Dunit = g/cm3
  Dvalue = 8.82
  Group = -> [Cu_element003,Zn_element003,Pb_element006]
  conduct = 2
  density = 1
  expand = 3
  formula = G4_BRONZE
  name = G4_BRONZE
  specific = 4
FEATURE [App::DocumentObjectGroupPython] Fe_element008  label="Fe_element : 74"  # scripted group (container) (typed FeaturePython)
  n = 74
  ref = Fe_element
FEATURE [App::DocumentObjectGroupPython] Cr_element002  label="Cr_element : 18"  # scripted group (container) (typed FeaturePython)
  n = 18
  ref = Cr_element
FEATURE [App::DocumentObjectGroupPython] Ni_element002  label="Ni_element : 8"  # scripted group (container) (typed FeaturePython)
  n = 8
  ref = Ni_element
FEATURE [App::DocumentObjectGroupPython] G4_STAINLESS_STEEL  label="G4_STAINLESS-STEEL"  # scripted group (container) (typed FeaturePython)
  Dunit = g/cm3
  Dvalue = 8
  Group = -> [Fe_element008,Cr_element002,Ni_element002]
  conduct = 2
  density = 1
  expand = 3
  formula = G4_STAINLESS-STEEL
  name = G4_STAINLESS-STEEL
  specific = 4
FEATURE [App::DocumentObjectGroupPython] H_element116  label="H_element : 064"  # scripted group (container) (typed FeaturePython)
  n = 18
  ref = H_element
FEATURE [App::DocumentObjectGroupPython] C_element126  label="C_element : 071"  # scripted group (container) (typed FeaturePython)
  n = 12
  ref = C_element
FEATURE [App::DocumentObjectGroupPython] O_element109  label="O_element : 062"  # scripted group (container) (typed FeaturePython)
  n = 7
  ref = O_element
FEATURE [App::DocumentObjectGroupPython] G4_CR39  # scripted group (container) (typed FeaturePython)
  Dunit = g/cm3
  Dvalue = 1.32
  Group = -> [H_element116,C_element126,O_element109]
  conduct = 2
  density = 1
  expand = 3
  formula = G4_CR39
  name = G4_CR39
  specific = 4
FEATURE [App::DocumentObjectGroupPython] H_element117  label="H_element : 38"  # scripted group (container) (typed FeaturePython)
  n = 38
  ref = H_element
FEATURE [App::DocumentObjectGroupPython] C_element127  label="C_element : 072"  # scripted group (container) (typed FeaturePython)
  n = 18
  ref = C_element
FEATURE [App::DocumentObjectGroupPython] O_element110  label="O_element : 063"  # scripted group (container) (typed FeaturePython)
  n = 1
  ref = O_element
FEATURE [App::DocumentObjectGroupPython] G4_OCTADECANOL  # scripted group (container) (typed FeaturePython)
  Dunit = g/cm3
  Dvalue = 0.812
  Group = -> [H_element117,C_element127,O_element110]
  conduct = 2
  density = 1
  expand = 3
  formula = G4_OCTADECANOL
  name = G4_OCTADECANOL
  specific = 4
FEATURE [App::DocumentObjectGroupPython] HEP  # scripted group (container) (typed FeaturePython)
  Group = -> [G4_lH2,G4_lN2,G4_lO2,G4_lAr,G4_lBr,G4_lKr,G4_lXe,G4_PbWO4,G4_Galactic,G4_GRAPHITE_POROUS,G4_LUCITE,G4_BRASS,G4_BRONZE,G4_STAINLESS_STEEL,G4_CR39,G4_OCTADECANOL]
FEATURE [App::DocumentObjectGroupPython] C_element128  label="C_element : 073"  # scripted group (container) (typed FeaturePython)
  n = 14
  ref = C_element
FEATURE [App::DocumentObjectGroupPython] H_element118  label="H_element : 065"  # scripted group (container) (typed FeaturePython)
  n = 10
  ref = H_element
FEATURE [App::DocumentObjectGroupPython] O_element111  label="O_element : 064"  # scripted group (container) (typed FeaturePython)
  n = 2
  ref = O_element
FEATURE [App::DocumentObjectGroupPython] N_element050  label="N_element : 023"  # scripted group (container) (typed FeaturePython)
  n = 2
  ref = N_element
FEATURE [App::DocumentObjectGroupPython] G4_KEVLAR  # scripted group (container) (typed FeaturePython)
  Dunit = g/cm3
  Dvalue = 1.44
  Group = -> [C_element128,H_element118,O_element111,N_element050]
  conduct = 2
  density = 1
  expand = 3
  formula = G4_KEVLAR
  name = G4_KEVLAR
  specific = 4
FEATURE [App::DocumentObjectGroupPython] C_element129  label="C_element : 074"  # scripted group (container) (typed FeaturePython)
  n = 10
  ref = C_element
FEATURE [App::DocumentObjectGroupPython] H_element119  label="H_element : 066"  # scripted group (container) (typed FeaturePython)
  n = 8
  ref = H_element
FEATURE [App::DocumentObjectGroupPython] O_element112  label="O_element : 065"  # scripted group (container) (typed FeaturePython)
  n = 4
  ref = O_element
FEATURE [App::DocumentObjectGroupPython] G4_DACRON  # scripted group (container) (typed FeaturePython)
  Dunit = g/cm3
  Dvalue = 1.4
  Group = -> [C_element129,H_element119,O_element112]
  conduct = 2
  density = 1
  expand = 3
  formula = G4_DACRON
  name = G4_DACRON
  specific = 4
FEATURE [App::DocumentObjectGroupPython] C_element130  label="C_element : 075"  # scripted group (container) (typed FeaturePython)
  n = 4
  ref = C_element
FEATURE [App::DocumentObjectGroupPython] H_element120  label="H_element : 067"  # scripted group (container) (typed FeaturePython)
  n = 5
  ref = H_element
FEATURE [App::DocumentObjectGroupPython] Cl_element030  label="Cl_element : 016"  # scripted group (container) (typed FeaturePython)
  n = 1
  ref = Cl_element
FEATURE [App::DocumentObjectGroupPython] G4_NEOPRENE  # scripted group (container) (typed FeaturePython)
  Dunit = g/cm3
  Dvalue = 1.23
  Group = -> [C_element130,H_element120,Cl_element030]
  conduct = 2
  density = 1
  expand = 3
  formula = G4_NEOPRENE
  name = G4_NEOPRENE
  specific = 4
FEATURE [App::DocumentObjectGroupPython] Space  # scripted group (container) (typed FeaturePython)
  Group = -> [G4_KEVLAR,G4_DACRON,G4_NEOPRENE]
FEATURE [App::DocumentObjectGroupPython] H_element121  label="H_element : 068"  # scripted group (container) (typed FeaturePython)
  n = 5
  ref = H_element
FEATURE [App::DocumentObjectGroupPython] C_element131  label="C_element : 076"  # scripted group (container) (typed FeaturePython)
  n = 4
  ref = C_element
FEATURE [App::DocumentObjectGroupPython] N_element051  label="N_element : 3"  # scripted group (container) (typed FeaturePython)
  n = 3
  ref = N_element
FEATURE [App::DocumentObjectGroupPython] O_element113  label="O_element : 066"  # scripted group (container) (typed FeaturePython)
  n = 1
  ref = O_element
FEATURE [App::DocumentObjectGroupPython] G4_CYTOSINE  # scripted group (container) (typed FeaturePython)
  Dunit = g/cm3
  Dvalue = 1.55
  Group = -> [H_element121,C_element131,N_element051,O_element113]
  conduct = 2
  density = 1
  expand = 3
  formula = G4_CYTOSINE
  name = G4_CYTOSINE
  specific = 4
FEATURE [App::DocumentObjectGroupPython] H_element122  label="H_element : 069"  # scripted group (container) (typed FeaturePython)
  n = 6
  ref = H_element
FEATURE [App::DocumentObjectGroupPython] C_element132  label="C_element : 077"  # scripted group (container) (typed FeaturePython)
  n = 5
  ref = C_element
FEATURE [App::DocumentObjectGroupPython] N_element052  label="N_element : 024"  # scripted group (container) (typed FeaturePython)
  n = 2
  ref = N_element
FEATURE [App::DocumentObjectGroupPython] O_element114  label="O_element : 067"  # scripted group (container) (typed FeaturePython)
  n = 2
  ref = O_element
FEATURE [App::DocumentObjectGroupPython] G4_THYMINE  # scripted group (container) (typed FeaturePython)
  Dunit = g/cm3
  Dvalue = 1.23
  Group = -> [H_element122,C_element132,N_element052,O_element114]
  conduct = 2
  density = 1
  expand = 3
  formula = G4_THYMINE
  name = G4_THYMINE
  specific = 4
FEATURE [App::DocumentObjectGroupPython] H_element123  label="H_element : 070"  # scripted group (container) (typed FeaturePython)
  n = 4
  ref = H_element
FEATURE [App::DocumentObjectGroupPython] C_element133  label="C_element : 078"  # scripted group (container) (typed FeaturePython)
  n = 4
  ref = C_element
FEATURE [App::DocumentObjectGroupPython] N_element053  label="N_element : 025"  # scripted group (container) (typed FeaturePython)
  n = 2
  ref = N_element
FEATURE [App::DocumentObjectGroupPython] O_element115  label="O_element : 068"  # scripted group (container) (typed FeaturePython)
  n = 2
  ref = O_element
FEATURE [App::DocumentObjectGroupPython] G4_URACIL  # scripted group (container) (typed FeaturePython)
  Dunit = g/cm3
  Dvalue = 1.32
  Group = -> [H_element123,C_element133,N_element053,O_element115]
  conduct = 2
  density = 1
  expand = 3
  formula = G4_URACIL
  name = G4_URACIL
  specific = 4
FEATURE [App::DocumentObjectGroupPython] H_element124  label="H_element : 071"  # scripted group (container) (typed FeaturePython)
  n = 4
  ref = H_element
FEATURE [App::DocumentObjectGroupPython] C_element134  label="C_element : 079"  # scripted group (container) (typed FeaturePython)
  n = 5
  ref = C_element
FEATURE [App::DocumentObjectGroupPython] N_element054  label="N_element : 026"  # scripted group (container) (typed FeaturePython)
  n = 5
  ref = N_element
FEATURE [App::DocumentObjectGroupPython] G4_DNA_ADENINE  # scripted group (container) (typed FeaturePython)
  Dunit = g/cm3
  Dvalue = 1
  Group = -> [H_element124,C_element134,N_element054]
  conduct = 2
  density = 1
  expand = 3
  formula = G4_DNA_ADENINE
  name = G4_DNA_ADENINE
  specific = 4
FEATURE [App::DocumentObjectGroupPython] H_element125  label="H_element : 072"  # scripted group (container) (typed FeaturePython)
  n = 4
  ref = H_element
FEATURE [App::DocumentObjectGroupPython] C_element135  label="C_element : 080"  # scripted group (container) (typed FeaturePython)
  n = 5
  ref = C_element
FEATURE [App::DocumentObjectGroupPython] N_element055  label="N_element : 027"  # scripted group (container) (typed FeaturePython)
  n = 5
  ref = N_element
FEATURE [App::DocumentObjectGroupPython] O_element116  label="O_element : 069"  # scripted group (container) (typed FeaturePython)
  n = 1
  ref = O_element
FEATURE [App::DocumentObjectGroupPython] G4_DNA_GUANINE  # scripted group (container) (typed FeaturePython)
  Dunit = g/cm3
  Dvalue = 1
  Group = -> [H_element125,C_element135,N_element055,O_element116]
  conduct = 2
  density = 1
  expand = 3
  formula = G4_DNA_GUANINE
  name = G4_DNA_GUANINE
  specific = 4
FEATURE [App::DocumentObjectGroupPython] H_element126  label="H_element : 073"  # scripted group (container) (typed FeaturePython)
  n = 4
  ref = H_element
FEATURE [App::DocumentObjectGroupPython] C_element136  label="C_element : 081"  # scripted group (container) (typed FeaturePython)
  n = 4
  ref = C_element
FEATURE [App::DocumentObjectGroupPython] N_element056  label="N_element : 028"  # scripted group (container) (typed FeaturePython)
  n = 3
  ref = N_element
FEATURE [App::DocumentObjectGroupPython] O_element117  label="O_element : 070"  # scripted group (container) (typed FeaturePython)
  n = 1
  ref = O_element
FEATURE [App::DocumentObjectGroupPython] G4_DNA_CYTOSINE  # scripted group (container) (typed FeaturePython)
  Dunit = g/cm3
  Dvalue = 1
  Group = -> [H_element126,C_element136,N_element056,O_element117]
  conduct = 2
  density = 1
  expand = 3
  formula = G4_DNA_CYTOSINE
  name = G4_DNA_CYTOSINE
  specific = 4
FEATURE [App::DocumentObjectGroupPython] H_element127  label="H_element : 074"  # scripted group (container) (typed FeaturePython)
  n = 5
  ref = H_element
FEATURE [App::DocumentObjectGroupPython] C_element137  label="C_element : 082"  # scripted group (container) (typed FeaturePython)
  n = 5
  ref = C_element
FEATURE [App::DocumentObjectGroupPython] N_element057  label="N_element : 029"  # scripted group (container) (typed FeaturePython)
  n = 2
  ref = N_element
FEATURE [App::DocumentObjectGroupPython] O_element118  label="O_element : 071"  # scripted group (container) (typed FeaturePython)
  n = 2
  ref = O_element
FEATURE [App::DocumentObjectGroupPython] G4_DNA_THYMINE  # scripted group (container) (typed FeaturePython)
  Dunit = g/cm3
  Dvalue = 1
  Group = -> [H_element127,C_element137,N_element057,O_element118]
  conduct = 2
  density = 1
  expand = 3
  formula = G4_DNA_THYMINE
  name = G4_DNA_THYMINE
  specific = 4
FEATURE [App::DocumentObjectGroupPython] H_element128  label="H_element : 075"  # scripted group (container) (typed FeaturePython)
  n = 3
  ref = H_element
FEATURE [App::DocumentObjectGroupPython] C_element138  label="C_element : 083"  # scripted group (container) (typed FeaturePython)
  n = 4
  ref = C_element
FEATURE [App::DocumentObjectGroupPython] N_element058  label="N_element : 030"  # scripted group (container) (typed FeaturePython)
  n = 2
  ref = N_element
FEATURE [App::DocumentObjectGroupPython] O_element119  label="O_element : 072"  # scripted group (container) (typed FeaturePython)
  n = 2
  ref = O_element
FEATURE [App::DocumentObjectGroupPython] G4_DNA_URACIL  # scripted group (container) (typed FeaturePython)
  Dunit = g/cm3
  Dvalue = 1
  Group = -> [H_element128,C_element138,N_element058,O_element119]
  conduct = 2
  density = 1
  expand = 3
  formula = G4_DNA_URACIL
  name = G4_DNA_URACIL
  specific = 4
FEATURE [App::DocumentObjectGroupPython] H_element129  label="H_element : 076"  # scripted group (container) (typed FeaturePython)
  n = 10
  ref = H_element
FEATURE [App::DocumentObjectGroupPython] C_element139  label="C_element : 084"  # scripted group (container) (typed FeaturePython)
  n = 10
  ref = C_element
FEATURE [App::DocumentObjectGroupPython] N_element059  label="N_element : 031"  # scripted group (container) (typed FeaturePython)
  n = 5
  ref = N_element
FEATURE [App::DocumentObjectGroupPython] O_element120  label="O_element : 073"  # scripted group (container) (typed FeaturePython)
  n = 4
  ref = O_element
FEATURE [App::DocumentObjectGroupPython] G4_DNA_ADENOSINE  # scripted group (container) (typed FeaturePython)
  Dunit = g/cm3
  Dvalue = 1
  Group = -> [H_element129,C_element139,N_element059,O_element120]
  conduct = 2
  density = 1
  expand = 3
  formula = G4_DNA_ADENOSINE
  name = G4_DNA_ADENOSINE
  specific = 4
FEATURE [App::DocumentObjectGroupPython] H_element130  label="H_element : 077"  # scripted group (container) (typed FeaturePython)
  n = 10
  ref = H_element
FEATURE [App::DocumentObjectGroupPython] C_element140  label="C_element : 085"  # scripted group (container) (typed FeaturePython)
  n = 10
  ref = C_element
FEATURE [App::DocumentObjectGroupPython] N_element060  label="N_element : 032"  # scripted group (container) (typed FeaturePython)
  n = 5
  ref = N_element
FEATURE [App::DocumentObjectGroupPython] O_element121  label="O_element : 074"  # scripted group (container) (typed FeaturePython)
  n = 5
  ref = O_element
FEATURE [App::DocumentObjectGroupPython] G4_DNA_GUANOSINE  # scripted group (container) (typed FeaturePython)
  Dunit = g/cm3
  Dvalue = 1
  Group = -> [H_element130,C_element140,N_element060,O_element121]
  conduct = 2
  density = 1
  expand = 3
  formula = G4_DNA_GUANOSINE
  name = G4_DNA_GUANOSINE
  specific = 4
FEATURE [App::DocumentObjectGroupPython] H_element131  label="H_element : 078"  # scripted group (container) (typed FeaturePython)
  n = 10
  ref = H_element
FEATURE [App::DocumentObjectGroupPython] C_element141  label="C_element : 086"  # scripted group (container) (typed FeaturePython)
  n = 9
  ref = C_element
FEATURE [App::DocumentObjectGroupPython] N_element061  label="N_element : 033"  # scripted group (container) (typed FeaturePython)
  n = 3
  ref = N_element
FEATURE [App::DocumentObjectGroupPython] O_element122  label="O_element : 075"  # scripted group (container) (typed FeaturePython)
  n = 5
  ref = O_element
FEATURE [App::DocumentObjectGroupPython] G4_DNA_CYTIDINE  # scripted group (container) (typed FeaturePython)
  Dunit = g/cm3
  Dvalue = 1
  Group = -> [H_element131,C_element141,N_element061,O_element122]
  conduct = 2
  density = 1
  expand = 3
  formula = G4_DNA_CYTIDINE
  name = G4_DNA_CYTIDINE
  specific = 4
FEATURE [App::DocumentObjectGroupPython] H_element132  label="H_element : 079"  # scripted group (container) (typed FeaturePython)
  n = 9
  ref = H_element
FEATURE [App::DocumentObjectGroupPython] C_element142  label="C_element : 087"  # scripted group (container) (typed FeaturePython)
  n = 9
  ref = C_element
FEATURE [App::DocumentObjectGroupPython] N_element062  label="N_element : 034"  # scripted group (container) (typed FeaturePython)
  n = 2
  ref = N_element
FEATURE [App::DocumentObjectGroupPython] O_element123  label="O_element : 076"  # scripted group (container) (typed FeaturePython)
  n = 6
  ref = O_element
FEATURE [App::DocumentObjectGroupPython] G4_DNA_URIDINE  # scripted group (container) (typed FeaturePython)
  Dunit = g/cm3
  Dvalue = 1
  Group = -> [H_element132,C_element142,N_element062,O_element123]
  conduct = 2
  density = 1
  expand = 3
  formula = G4_DNA_URIDINE
  name = G4_DNA_URIDINE
  specific = 4
FEATURE [App::DocumentObjectGroupPython] H_element133  label="H_element : 080"  # scripted group (container) (typed FeaturePython)
  n = 11
  ref = H_element
FEATURE [App::DocumentObjectGroupPython] C_element143  label="C_element : 088"  # scripted group (container) (typed FeaturePython)
  n = 10
  ref = C_element
FEATURE [App::DocumentObjectGroupPython] N_element063  label="N_element : 035"  # scripted group (container) (typed FeaturePython)
  n = 2
  ref = N_element
FEATURE [App::DocumentObjectGroupPython] O_element124  label="O_element : 077"  # scripted group (container) (typed FeaturePython)
  n = 6
  ref = O_element
FEATURE [App::DocumentObjectGroupPython] G4_DNA_METHYLURIDINE  # scripted group (container) (typed FeaturePython)
  Dunit = g/cm3
  Dvalue = 1
  Group = -> [H_element133,C_element143,N_element063,O_element124]
  conduct = 2
  density = 1
  expand = 3
  formula = G4_DNA_METHYLURIDINE
  name = G4_DNA_METHYLURIDINE
  specific = 4
FEATURE [App::DocumentObjectGroupPython] P_element014  label="P_element : 003"  # scripted group (container) (typed FeaturePython)
  n = 1
  ref = P_element
FEATURE [App::DocumentObjectGroupPython] O_element125  label="O_element : 078"  # scripted group (container) (typed FeaturePython)
  n = 3
  ref = O_element
FEATURE [App::DocumentObjectGroupPython] G4_DNA_MONOPHOSPHATE  # scripted group (container) (typed FeaturePython)
  Dunit = g/cm3
  Dvalue = 1
  Group = -> [P_element014,O_element125]
  conduct = 2
  density = 1
  expand = 3
  formula = G4_DNA_MONOPHOSPHATE
  name = G4_DNA_MONOPHOSPHATE
  specific = 4
FEATURE [App::DocumentObjectGroupPython] H_element134  label="H_element : 081"  # scripted group (container) (typed FeaturePython)
  n = 10
  ref = H_element
FEATURE [App::DocumentObjectGroupPython] C_element144  label="C_element : 089"  # scripted group (container) (typed FeaturePython)
  n = 10
  ref = C_element
FEATURE [App::DocumentObjectGroupPython] N_element064  label="N_element : 036"  # scripted group (container) (typed FeaturePython)
  n = 5
  ref = N_element
FEATURE [App::DocumentObjectGroupPython] O_element126  label="O_element : 079"  # scripted group (container) (typed FeaturePython)
  n = 7
  ref = O_element
FEATURE [App::DocumentObjectGroupPython] P_element015  label="P_element : 004"  # scripted group (container) (typed FeaturePython)
  n = 1
  ref = P_element
FEATURE [App::DocumentObjectGroupPython] G4_DNA_A  # scripted group (container) (typed FeaturePython)
  Dunit = g/cm3
  Dvalue = 1
  Group = -> [H_element134,C_element144,N_element064,O_element126,P_element015]
  conduct = 2
  density = 1
  expand = 3
  formula = G4_DNA_A
  name = G4_DNA_A
  specific = 4
FEATURE [App::DocumentObjectGroupPython] H_element135  label="H_element : 082"  # scripted group (container) (typed FeaturePython)
  n = 10
  ref = H_element
FEATURE [App::DocumentObjectGroupPython] C_element145  label="C_element : 090"  # scripted group (container) (typed FeaturePython)
  n = 10
  ref = C_element
FEATURE [App::DocumentObjectGroupPython] N_element065  label="N_element : 037"  # scripted group (container) (typed FeaturePython)
  n = 5
  ref = N_element
FEATURE [App::DocumentObjectGroupPython] O_element127  label="O_element : 8"  # scripted group (container) (typed FeaturePython)
  n = 8
  ref = O_element
FEATURE [App::DocumentObjectGroupPython] P_element016  label="P_element : 005"  # scripted group (container) (typed FeaturePython)
  n = 1
  ref = P_element
FEATURE [App::DocumentObjectGroupPython] G4_DNA_G  # scripted group (container) (typed FeaturePython)
  Dunit = g/cm3
  Dvalue = 1
  Group = -> [H_element135,C_element145,N_element065,O_element127,P_element016]
  conduct = 2
  density = 1
  expand = 3
  formula = G4_DNA_G
  name = G4_DNA_G
  specific = 4
FEATURE [App::DocumentObjectGroupPython] H_element136  label="H_element : 083"  # scripted group (container) (typed FeaturePython)
  n = 10
  ref = H_element
FEATURE [App::DocumentObjectGroupPython] C_element146  label="C_element : 091"  # scripted group (container) (typed FeaturePython)
  n = 9
  ref = C_element
FEATURE [App::DocumentObjectGroupPython] N_element066  label="N_element : 038"  # scripted group (container) (typed FeaturePython)
  n = 3
  ref = N_element
FEATURE [App::DocumentObjectGroupPython] O_element128  label="O_element : 080"  # scripted group (container) (typed FeaturePython)
  n = 8
  ref = O_element
FEATURE [App::DocumentObjectGroupPython] P_element017  label="P_element : 006"  # scripted group (container) (typed FeaturePython)
  n = 1
  ref = P_element
FEATURE [App::DocumentObjectGroupPython] G4_DNA_C  # scripted group (container) (typed FeaturePython)
  Dunit = g/cm3
  Dvalue = 1
  Group = -> [H_element136,C_element146,N_element066,O_element128,P_element017]
  conduct = 2
  density = 1
  expand = 3
  formula = G4_DNA_C
  name = G4_DNA_C
  specific = 4
FEATURE [App::DocumentObjectGroupPython] H_element137  label="H_element : 084"  # scripted group (container) (typed FeaturePython)
  n = 9
  ref = H_element
FEATURE [App::DocumentObjectGroupPython] C_element147  label="C_element : 092"  # scripted group (container) (typed FeaturePython)
  n = 9
  ref = C_element
FEATURE [App::DocumentObjectGroupPython] N_element067  label="N_element : 039"  # scripted group (container) (typed FeaturePython)
  n = 2
  ref = N_element
FEATURE [App::DocumentObjectGroupPython] O_element129  label="O_element : 9"  # scripted group (container) (typed FeaturePython)
  n = 9
  ref = O_element
FEATURE [App::DocumentObjectGroupPython] P_element018  label="P_element : 007"  # scripted group (container) (typed FeaturePython)
  n = 1
  ref = P_element
FEATURE [App::DocumentObjectGroupPython] G4_DNA_U  # scripted group (container) (typed FeaturePython)
  Dunit = g/cm3
  Dvalue = 1
  Group = -> [H_element137,C_element147,N_element067,O_element129,P_element018]
  conduct = 2
  density = 1
  expand = 3
  formula = G4_DNA_U
  name = G4_DNA_U
  specific = 4
FEATURE [App::DocumentObjectGroupPython] H_element138  label="H_element : 085"  # scripted group (container) (typed FeaturePython)
  n = 11
  ref = H_element
FEATURE [App::DocumentObjectGroupPython] C_element148  label="C_element : 093"  # scripted group (container) (typed FeaturePython)
  n = 10
  ref = C_element
FEATURE [App::DocumentObjectGroupPython] N_element068  label="N_element : 040"  # scripted group (container) (typed FeaturePython)
  n = 2
  ref = N_element
FEATURE [App::DocumentObjectGroupPython] O_element130  label="O_element : 081"  # scripted group (container) (typed FeaturePython)
  n = 9
  ref = O_element
FEATURE [App::DocumentObjectGroupPython] P_element019  label="P_element : 008"  # scripted group (container) (typed FeaturePython)
  n = 1
  ref = P_element
FEATURE [App::DocumentObjectGroupPython] G4_DNA_MU  # scripted group (container) (typed FeaturePython)
  Dunit = g/cm3
  Dvalue = 1
  Group = -> [H_element138,C_element148,N_element068,O_element130,P_element019]
  conduct = 2
  density = 1
  expand = 3
  formula = G4_DNA_MU
  name = G4_DNA_MU
  specific = 4
FEATURE [App::DocumentObjectGroupPython] BioChemical  # scripted group (container) (typed FeaturePython)
  Group = -> [G4_CYTOSINE,G4_THYMINE,G4_URACIL,G4_DNA_ADENINE,G4_DNA_GUANINE,G4_DNA_CYTOSINE,G4_DNA_THYMINE,G4_DNA_URACIL,G4_DNA_ADENOSINE,G4_DNA_GUANOSINE,G4_DNA_CYTIDINE,G4_DNA_URIDINE,G4_DNA_METHYLURIDINE,G4_DNA_MONOPHOSPHATE,G4_DNA_A,G4_DNA_G,G4_DNA_C,G4_DNA_U,G4_DNA_MU]
FEATURE [App::DocumentObjectGroupPython] G4Materials  # scripted group (container) (typed FeaturePython)
  Group = -> [NIST,Element,HEP,Space,BioChemical]
  version = 1
FEATURE [App::DocumentObjectGroupPython] Geant4  # scripted group (container) (typed FeaturePython)
  Group = -> [G4Isotopes,G4Elements,G4Materials]
FEATURE [App::DocumentObjectGroupPython] Materials  # scripted group (container) (typed FeaturePython)
  Group = -> [Geant4]
FEATURE [Part::FeaturePython] GDMLBox_WorldBox  # WARN: FeaturePython — macro-defined, semantics opaque (R4)
  lunit = 2
  material = 5
  x = 100
  y = 100
  z = 100
FEATURE [Sketcher::SketchObject] Sketch
  FullyConstrained = false
  sketch-geometry (15):
    g0-g5: Circle x6 (B-spline internal-alignment scaffolding for g6; pole/knot coordinates omitted)
    g6: BSplineCurve PolesCount=7 KnotsCount=5 Degree=3 IsPeriodic=0
    g7-g10: GeomPoint x4 (B-spline internal-alignment scaffolding for g6; pole/knot coordinates omitted)
    g11: LineSegment StartX=-4.39557 StartY=8.39124 StartZ=0 EndX=-5.2662 EndY=10.5884 EndZ=0
    g12: LineSegment StartX=-5.2662 StartY=10.5884 StartZ=0 EndX=-7.82152 EndY=9.89481 EndZ=0
    g13: LineSegment StartX=-7.82152 StartY=9.89481 StartZ=0 EndX=-9.50073 EndY=7.63152 EndZ=0
    g14: ArcOfCircle CenterX=-7.8377 CenterY=5.34547 CenterZ=0 NormalX=0 NormalY=0 NormalZ=1 AngleXU=0 Radius=2.82696 StartAngle=4.84147 EndAngle=8.48291
  constraints (9):
    c: Weight(g0) = 1
    c: Equal(g0, g1-g5) x5
    c: InternalAlignment(g0-g5 -> g6) x6
    c: InternalAlignment(g7-g10 -> g6) x4
    c: Coincident(g11,g6)
    c: Coincident(g11,g12)
    c: Coincident(g12,g13)
    c: Coincident(g14,g13)
    c: Coincident(g14,g6)
FEATURE [Part::Extrusion] Extrude
  Base = -> Sketch
  Dir = (0,0,1)
  DirMode = 2
  FaceMakerClass = Part::FaceMakerBullseye
  LengthFwd = 10
  LengthRev = 0
  Placement = pos=(13,12,0) rot=(0,0,1;0rad)
  Solid = true
  Symmetric = false
  material = 1
FEATURE [Part::Mirroring] Part__Mirroring  label="mirror1"
  Base = (0,0,0)
  Normal = (1,0,0)
  Source = -> Extrude
  material = 261
FEATURE [Part::Mirroring] Part__Mirroring002  label="mirror2"
  Base = (0,0,0)
  Normal = (0,1,0)
  Source = -> Part__Mirroring
  material = 5
FEATURE [App::Part] Part
  Group = -> [Sketch,Extrude,Part__Mirroring,Part__Mirroring002]
  Origin = -> Origin001
FEATURE [App::Part] worldVOL
  Group = -> [GDMLBox_WorldBox,Part]
  Origin = -> Origin
